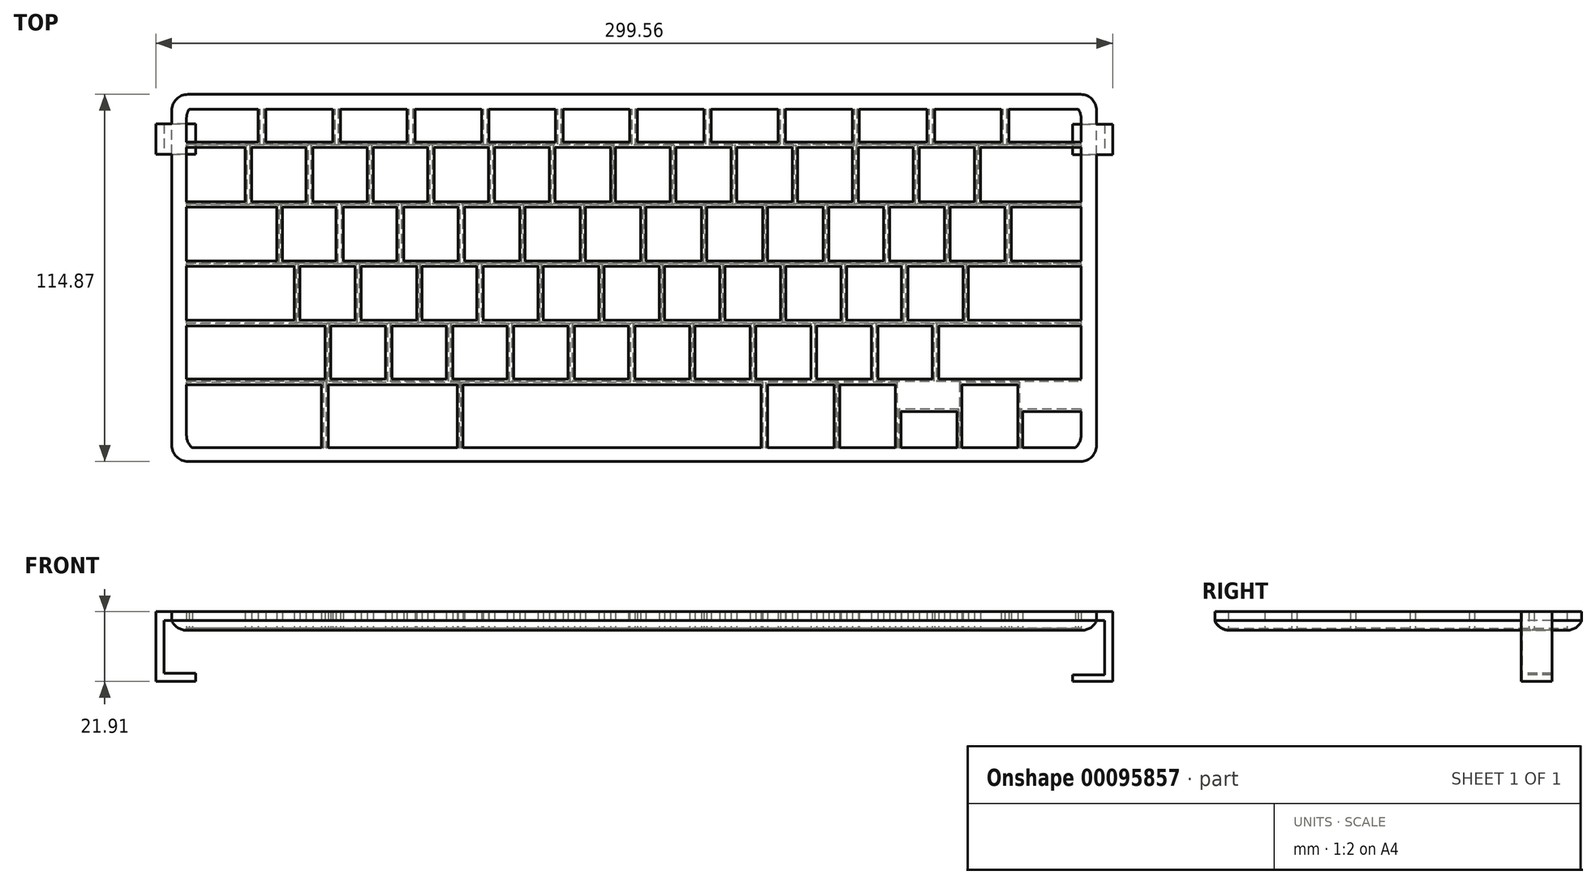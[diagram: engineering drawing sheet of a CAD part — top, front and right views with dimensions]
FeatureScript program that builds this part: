
annotation { "Feature Type Name" : "Feature", "Feature Type Description" : "" }
export const myFeature = defineFeature(function(context is Context, id is Id, definition is map)
    precondition{}
    {
        {
            var Q0;
            Q0=qCreatedBy(makeId("Top.planeOp"),FACE);
            var sketch = newSketch(context, id + "F0", { "sketchPlane" : qUnion([Q0])});
            skLineSegment(sketch, "E0", {"start": v(-1288.18, -372.7) * mm, "end": v(-998.62, -372.7) * mm});
            skSolve(sketch);
        }
        {
            var Q0;
            Q0=qCreatedBy(makeId("Top.planeOp"),FACE);
            var sketch = newSketch(context, id + "F1", { "sketchPlane" : qUnion([Q0])});
            skLineSegment(sketch, "E1.0", {"start": v(-1283.18, -372.7) * mm, "end": v(-1003.62, -372.7) * mm});
            skLineSegment(sketch, "E2", {"start": v(-1288.18, -367.7) * mm, "end": v(-1288.18, -262.82) * mm});
            skLineSegment(sketch, "E3", {"start": v(-998.62, -367.7) * mm, "end": v(-998.62, -262.82) * mm});
            skLineSegment(sketch, "E4", {"start": v(-1283.18, -257.82) * mm, "end": v(-1003.62, -257.82) * mm});
            skLineSegment(sketch, "E5.bottom", {"start": v(-1278.58, -260.22) * mm, "end": v(-1008.5, -260.22) * mm});
            skLineSegment(sketch, "E5.left", {"start": v(-1283.58, -265.22) * mm, "end": v(-1283.58, -272.7) * mm});
            skLineSegment(sketch, "E5.right", {"start": v(-1003.5, -265.22) * mm, "end": v(-1003.5, -272.7) * mm});
            skLineSegment(sketch, "E6.bottom", {"start": v(-1283.58, -272.7) * mm, "end": v(-1261.2, -272.7) * mm});
            skLineSegment(sketch, "E6.top", {"start": v(-1283.58, -274.39) * mm, "end": v(-1265.23, -274.39) * mm});
            skLineSegment(sketch, "E7.bottom", {"start": v(-1003.5, -291.4) * mm, "end": v(-1035.02, -291.4) * mm});
            skLineSegment(sketch, "E7.top", {"start": v(-1003.5, -293.02) * mm, "end": v(-1025.33, -293.02) * mm});
            skLineSegment(sketch, "E8.bottom", {"start": v(-1283.58, -309.96) * mm, "end": v(-1255.31, -309.96) * mm});
            skLineSegment(sketch, "E8.top", {"start": v(-1283.58, -311.57) * mm, "end": v(-1249.8, -311.57) * mm});
            skLineSegment(sketch, "E9.bottom", {"start": v(-1003.5, -328.56) * mm, "end": v(-1038.78, -328.56) * mm});
            skLineSegment(sketch, "E9.top", {"start": v(-1003.5, -330.23) * mm, "end": v(-1048.09, -330.23) * mm});
            skLineSegment(sketch, "E10.bottom", {"start": v(-1283.58, -346.92) * mm, "end": v(-1240.17, -346.92) * mm});
            skLineSegment(sketch, "E10.top", {"start": v(-1283.58, -348.68) * mm, "end": v(-1241.32, -348.68) * mm});
            skLineSegment(sketch, "E11.left", {"start": v(-1023.3, -348.68) * mm, "end": v(-1023.3, -368.4) * mm});
            skLineSegment(sketch, "E11.right", {"start": v(-1021.81, -357.03) * mm, "end": v(-1021.81, -368.4) * mm});
            skLineSegment(sketch, "E12.left", {"start": v(-1040.83, -368.4) * mm, "end": v(-1040.83, -348.68) * mm});
            skLineSegment(sketch, "E12.right", {"start": v(-1042.36, -368.4) * mm, "end": v(-1042.36, -357.03) * mm});
            skLineSegment(sketch, "E13.left", {"start": v(-1059.9, -368.4) * mm, "end": v(-1059.9, -357.03) * mm});
            skLineSegment(sketch, "E13.right", {"start": v(-1061.66, -368.4) * mm, "end": v(-1061.66, -348.68) * mm});
            skLineSegment(sketch, "E14.left", {"start": v(-1079.03, -368.4) * mm, "end": v(-1079.03, -348.68) * mm});
            skLineSegment(sketch, "E14.right", {"start": v(-1080.8, -368.4) * mm, "end": v(-1080.8, -348.68) * mm});
            skLineSegment(sketch, "E15.top", {"start": v(-1282.73, -262.43) * mm, "end": v(-1261.2, -262.43) * mm});
            skLineSegment(sketch, "E16.top", {"start": v(-1021.81, -357.03) * mm, "end": v(-1003.5, -357.03) * mm});
            skLineSegment(sketch, "E17.top", {"start": v(-1059.9, -357.03) * mm, "end": v(-1042.36, -357.03) * mm});
            skLineSegment(sketch, "E18.left", {"start": v(-1241.32, -348.68) * mm, "end": v(-1241.32, -368.4) * mm});
            skLineSegment(sketch, "E18.right", {"start": v(-1239.21, -348.68) * mm, "end": v(-1239.21, -368.4) * mm});
            skLineSegment(sketch, "E19.left", {"start": v(-1198.75, -348.68) * mm, "end": v(-1198.75, -368.4) * mm});
            skLineSegment(sketch, "E19.right", {"start": v(-1197.07, -348.68) * mm, "end": v(-1197.07, -368.4) * mm});
            skLineSegment(sketch, "E20.left", {"start": v(-1103.7, -348.68) * mm, "end": v(-1103.7, -368.4) * mm});
            skLineSegment(sketch, "E20.right", {"start": v(-1101.6, -348.68) * mm, "end": v(-1101.6, -368.4) * mm});
            skLineSegment(sketch, "E21.left", {"start": v(-1240.17, -330.23) * mm, "end": v(-1240.17, -346.92) * mm});
            skLineSegment(sketch, "E21.right", {"start": v(-1238.38, -330.23) * mm, "end": v(-1238.38, -346.92) * mm});
            skLineSegment(sketch, "E22.left", {"start": v(-1221.22, -330.23) * mm, "end": v(-1221.22, -346.92) * mm});
            skLineSegment(sketch, "E22.right", {"start": v(-1219.2, -330.23) * mm, "end": v(-1219.2, -346.92) * mm});
            skLineSegment(sketch, "E23.left", {"start": v(-1202.19, -330.23) * mm, "end": v(-1202.19, -346.92) * mm});
            skLineSegment(sketch, "E23.right", {"start": v(-1200.22, -330.23) * mm, "end": v(-1200.22, -346.92) * mm});
            skLineSegment(sketch, "E24.left", {"start": v(-1183.14, -330.23) * mm, "end": v(-1183.14, -346.92) * mm});
            skLineSegment(sketch, "E24.right", {"start": v(-1181.13, -330.23) * mm, "end": v(-1181.13, -346.92) * mm});
            skLineSegment(sketch, "E25.left", {"start": v(-1164.12, -330.23) * mm, "end": v(-1164.12, -346.92) * mm});
            skLineSegment(sketch, "E25.right", {"start": v(-1162.15, -330.23) * mm, "end": v(-1162.15, -346.92) * mm});
            skLineSegment(sketch, "E26.left", {"start": v(-1145.17, -330.23) * mm, "end": v(-1145.17, -346.92) * mm});
            skLineSegment(sketch, "E26.right", {"start": v(-1143.13, -330.23) * mm, "end": v(-1143.13, -346.92) * mm});
            skLineSegment(sketch, "E27.left", {"start": v(-1126.04, -330.23) * mm, "end": v(-1126.04, -346.92) * mm});
            skLineSegment(sketch, "E27.right", {"start": v(-1124.36, -330.23) * mm, "end": v(-1124.36, -346.92) * mm});
            skLineSegment(sketch, "E28.left", {"start": v(-1107.12, -330.23) * mm, "end": v(-1107.12, -346.92) * mm});
            skLineSegment(sketch, "E28.right", {"start": v(-1105.3, -330.23) * mm, "end": v(-1105.3, -346.92) * mm});
            skLineSegment(sketch, "E29.left", {"start": v(-1088.03, -330.23) * mm, "end": v(-1088.03, -346.92) * mm});
            skLineSegment(sketch, "E29.right", {"start": v(-1086.26, -330.23) * mm, "end": v(-1086.26, -346.92) * mm});
            skLineSegment(sketch, "E30.left", {"start": v(-1069.15, -330.23) * mm, "end": v(-1069.15, -346.92) * mm});
            skLineSegment(sketch, "E30.right", {"start": v(-1067.09, -330.23) * mm, "end": v(-1067.09, -346.92) * mm});
            skLineSegment(sketch, "E31.left", {"start": v(-1050.1, -330.23) * mm, "end": v(-1050.1, -346.92) * mm});
            skLineSegment(sketch, "E31.right", {"start": v(-1048.09, -330.23) * mm, "end": v(-1048.09, -346.92) * mm});
            skLineSegment(sketch, "E32.left", {"start": v(-1249.8, -311.57) * mm, "end": v(-1249.8, -328.56) * mm});
            skLineSegment(sketch, "E32.right", {"start": v(-1248.02, -311.57) * mm, "end": v(-1248.02, -328.56) * mm});
            skLineSegment(sketch, "E33.left", {"start": v(-1230.78, -311.57) * mm, "end": v(-1230.78, -328.56) * mm});
            skLineSegment(sketch, "E33.right", {"start": v(-1228.88, -311.57) * mm, "end": v(-1228.88, -328.56) * mm});
            skLineSegment(sketch, "E34.left", {"start": v(-1211.54, -311.57) * mm, "end": v(-1211.54, -328.56) * mm});
            skLineSegment(sketch, "E34.right", {"start": v(-1209.87, -311.57) * mm, "end": v(-1209.87, -328.56) * mm});
            skLineSegment(sketch, "E35.left", {"start": v(-1192.67, -311.57) * mm, "end": v(-1192.67, -328.56) * mm});
            skLineSegment(sketch, "E35.right", {"start": v(-1190.64, -311.57) * mm, "end": v(-1190.64, -328.56) * mm});
            skLineSegment(sketch, "E36.left", {"start": v(-1173.55, -311.57) * mm, "end": v(-1173.55, -328.56) * mm});
            skLineSegment(sketch, "E36.right", {"start": v(-1171.87, -311.57) * mm, "end": v(-1171.87, -328.56) * mm});
            skLineSegment(sketch, "E37.left", {"start": v(-1154.53, -311.57) * mm, "end": v(-1154.53, -328.56) * mm});
            skLineSegment(sketch, "E37.right", {"start": v(-1152.87, -311.57) * mm, "end": v(-1152.87, -328.56) * mm});
            skLineSegment(sketch, "E38.left", {"start": v(-1135.55, -311.57) * mm, "end": v(-1135.55, -328.56) * mm});
            skLineSegment(sketch, "E38.right", {"start": v(-1133.9, -311.57) * mm, "end": v(-1133.9, -328.56) * mm});
            skLineSegment(sketch, "E39.left", {"start": v(-1116.65, -311.57) * mm, "end": v(-1116.65, -328.56) * mm});
            skLineSegment(sketch, "E39.right", {"start": v(-1115, -311.57) * mm, "end": v(-1115, -328.56) * mm});
            skLineSegment(sketch, "E40.left", {"start": v(-1097.53, -311.57) * mm, "end": v(-1097.53, -328.56) * mm});
            skLineSegment(sketch, "E40.right", {"start": v(-1096, -311.57) * mm, "end": v(-1096, -328.56) * mm});
            skLineSegment(sketch, "E41.left", {"start": v(-1078.67, -311.57) * mm, "end": v(-1078.67, -328.56) * mm});
            skLineSegment(sketch, "E41.right", {"start": v(-1076.87, -311.57) * mm, "end": v(-1076.87, -328.56) * mm});
            skLineSegment(sketch, "E42.left", {"start": v(-1059.7, -311.57) * mm, "end": v(-1059.7, -328.56) * mm});
            skLineSegment(sketch, "E42.right", {"start": v(-1057.73, -311.57) * mm, "end": v(-1057.73, -328.56) * mm});
            skLineSegment(sketch, "E43.left", {"start": v(-1040.48, -311.57) * mm, "end": v(-1040.48, -328.56) * mm});
            skLineSegment(sketch, "E43.right", {"start": v(-1038.78, -311.57) * mm, "end": v(-1038.78, -328.56) * mm});
            skLineSegment(sketch, "E44.left", {"start": v(-1027.3, -293.02) * mm, "end": v(-1027.3, -309.96) * mm});
            skLineSegment(sketch, "E44.right", {"start": v(-1025.33, -293.02) * mm, "end": v(-1025.33, -309.96) * mm});
            skLineSegment(sketch, "E45.left", {"start": v(-1046.22, -293.02) * mm, "end": v(-1046.22, -309.96) * mm});
            skLineSegment(sketch, "E45.right", {"start": v(-1044.44, -293.02) * mm, "end": v(-1044.44, -309.96) * mm});
            skLineSegment(sketch, "E46.left", {"start": v(-1065.37, -293.02) * mm, "end": v(-1065.37, -309.96) * mm});
            skLineSegment(sketch, "E46.right", {"start": v(-1063.36, -293.02) * mm, "end": v(-1063.36, -309.96) * mm});
            skLineSegment(sketch, "E47.left", {"start": v(-1084.25, -293.02) * mm, "end": v(-1084.25, -309.96) * mm});
            skLineSegment(sketch, "E47.right", {"start": v(-1082.42, -293.02) * mm, "end": v(-1082.42, -309.96) * mm});
            skLineSegment(sketch, "E48.left", {"start": v(-1103.17, -293.02) * mm, "end": v(-1103.17, -309.96) * mm});
            skLineSegment(sketch, "E48.right", {"start": v(-1101.62, -293.02) * mm, "end": v(-1101.62, -309.96) * mm});
            skLineSegment(sketch, "E49.left", {"start": v(-1122.33, -293.02) * mm, "end": v(-1122.33, -309.96) * mm});
            skLineSegment(sketch, "E49.right", {"start": v(-1120.67, -293.02) * mm, "end": v(-1120.67, -309.96) * mm});
            skLineSegment(sketch, "E50.bottom", {"start": v(-1143.54, -293.02) * mm, "end": v(-1141.36, -293.02) * mm});
            skLineSegment(sketch, "E50.top", {"start": v(-1143.47, -309.96) * mm, "end": v(-1141.36, -309.96) * mm});
            skLineSegment(sketch, "E50.right", {"start": v(-1139.74, -293.02) * mm, "end": v(-1139.74, -309.96) * mm});
            skLineSegment(sketch, "E51.left", {"start": v(-1160.37, -293.02) * mm, "end": v(-1160.37, -309.96) * mm});
            skLineSegment(sketch, "E51.right", {"start": v(-1158.61, -293.02) * mm, "end": v(-1158.61, -309.96) * mm});
            skLineSegment(sketch, "E52.left", {"start": v(-1179.26, -293.02) * mm, "end": v(-1179.26, -309.96) * mm});
            skLineSegment(sketch, "E52.right", {"start": v(-1177.57, -293.02) * mm, "end": v(-1177.57, -309.96) * mm});
            skLineSegment(sketch, "E53.left", {"start": v(-1198.57, -293.02) * mm, "end": v(-1198.57, -309.96) * mm});
            skLineSegment(sketch, "E53.right", {"start": v(-1196.47, -293.02) * mm, "end": v(-1196.47, -309.96) * mm});
            skLineSegment(sketch, "E54.left", {"start": v(-1217.7, -293.02) * mm, "end": v(-1217.7, -309.96) * mm});
            skLineSegment(sketch, "E54.right", {"start": v(-1215.6, -293.02) * mm, "end": v(-1215.6, -309.96) * mm});
            skLineSegment(sketch, "E55.left", {"start": v(-1236.78, -293.02) * mm, "end": v(-1236.78, -309.96) * mm});
            skLineSegment(sketch, "E55.right", {"start": v(-1234.44, -293.02) * mm, "end": v(-1234.44, -309.96) * mm});
            skLineSegment(sketch, "E56.left", {"start": v(-1253.5, -293.02) * mm, "end": v(-1253.5, -309.96) * mm});
            skLineSegment(sketch, "E56.right", {"start": v(-1255.31, -293.02) * mm, "end": v(-1255.31, -309.96) * mm});
            skLineSegment(sketch, "E57.left", {"start": v(-1265.23, -274.39) * mm, "end": v(-1265.23, -291.4) * mm});
            skLineSegment(sketch, "E57.right", {"start": v(-1263.13, -274.39) * mm, "end": v(-1263.13, -291.4) * mm});
            skLineSegment(sketch, "E58.left", {"start": v(-1246.16, -274.39) * mm, "end": v(-1246.16, -291.4) * mm});
            skLineSegment(sketch, "E58.right", {"start": v(-1243.97, -274.39) * mm, "end": v(-1243.97, -291.4) * mm});
            skLineSegment(sketch, "E59.left", {"start": v(-1226.95, -274.39) * mm, "end": v(-1226.95, -291.4) * mm});
            skLineSegment(sketch, "E59.right", {"start": v(-1225.03, -274.39) * mm, "end": v(-1225.03, -291.4) * mm});
            skLineSegment(sketch, "E60.left", {"start": v(-1208.07, -274.39) * mm, "end": v(-1208.07, -291.4) * mm});
            skLineSegment(sketch, "E60.right", {"start": v(-1206, -274.39) * mm, "end": v(-1206, -291.4) * mm});
            skLineSegment(sketch, "E61.left", {"start": v(-1189.03, -274.39) * mm, "end": v(-1189.03, -291.4) * mm});
            skLineSegment(sketch, "E61.right", {"start": v(-1187.09, -274.39) * mm, "end": v(-1187.09, -291.4) * mm});
            skLineSegment(sketch, "E62.left", {"start": v(-1170.02, -274.39) * mm, "end": v(-1170.02, -291.4) * mm});
            skLineSegment(sketch, "E62.right", {"start": v(-1168.2, -274.39) * mm, "end": v(-1168.2, -291.4) * mm});
            skLineSegment(sketch, "E63.left", {"start": v(-1150.85, -274.39) * mm, "end": v(-1150.85, -291.4) * mm});
            skLineSegment(sketch, "E63.right", {"start": v(-1149.3, -274.39) * mm, "end": v(-1149.3, -291.4) * mm});
            skLineSegment(sketch, "E64.left", {"start": v(-1132.1, -274.39) * mm, "end": v(-1132.1, -291.4) * mm});
            skLineSegment(sketch, "E64.right", {"start": v(-1130.32, -274.39) * mm, "end": v(-1130.32, -291.4) * mm});
            skLineSegment(sketch, "E65.left", {"start": v(-1113.1, -274.39) * mm, "end": v(-1113.1, -291.4) * mm});
            skLineSegment(sketch, "E65.right", {"start": v(-1111.29, -274.39) * mm, "end": v(-1111.29, -291.4) * mm});
            skLineSegment(sketch, "E66.left", {"start": v(-1093.95, -274.39) * mm, "end": v(-1093.95, -291.4) * mm});
            skLineSegment(sketch, "E66.right", {"start": v(-1092.22, -274.39) * mm, "end": v(-1092.22, -291.4) * mm});
            skLineSegment(sketch, "E67.left", {"start": v(-1075.1, -274.39) * mm, "end": v(-1075.1, -291.4) * mm});
            skLineSegment(sketch, "E67.right", {"start": v(-1073.22, -274.39) * mm, "end": v(-1073.22, -291.4) * mm});
            skLineSegment(sketch, "E68.left", {"start": v(-1056.04, -274.39) * mm, "end": v(-1056.04, -291.4) * mm});
            skLineSegment(sketch, "E68.right", {"start": v(-1054.15, -274.39) * mm, "end": v(-1054.15, -291.4) * mm});
            skLineSegment(sketch, "E69.left", {"start": v(-1036.83, -274.39) * mm, "end": v(-1036.83, -291.4) * mm});
            skLineSegment(sketch, "E69.right", {"start": v(-1035.02, -274.39) * mm, "end": v(-1035.02, -291.4) * mm});
            skLineSegment(sketch, "E70.left", {"start": v(-1051.72, -262.43) * mm, "end": v(-1051.72, -272.7) * mm});
            skLineSegment(sketch, "E70.right", {"start": v(-1049.35, -262.43) * mm, "end": v(-1049.35, -272.7) * mm});
            skLineSegment(sketch, "E71.left", {"start": v(-1075.08, -262.43) * mm, "end": v(-1075.08, -272.7) * mm});
            skLineSegment(sketch, "E71.right", {"start": v(-1072.96, -262.43) * mm, "end": v(-1072.96, -272.7) * mm});
            skLineSegment(sketch, "E72.left", {"start": v(-1098.33, -262.43) * mm, "end": v(-1098.33, -272.7) * mm});
            skLineSegment(sketch, "E72.right", {"start": v(-1096.04, -262.43) * mm, "end": v(-1096.04, -272.7) * mm});
            skLineSegment(sketch, "E73.left", {"start": v(-1121.6, -262.43) * mm, "end": v(-1121.6, -272.7) * mm});
            skLineSegment(sketch, "E73.right", {"start": v(-1119.29, -262.43) * mm, "end": v(-1119.29, -272.7) * mm});
            skLineSegment(sketch, "E74.left", {"start": v(-1144.78, -262.43) * mm, "end": v(-1144.78, -272.7) * mm});
            skLineSegment(sketch, "E74.right", {"start": v(-1142.44, -262.43) * mm, "end": v(-1142.44, -272.7) * mm});
            skLineSegment(sketch, "E75.left", {"start": v(-1168.04, -262.43) * mm, "end": v(-1168.04, -272.7) * mm});
            skLineSegment(sketch, "E75.right", {"start": v(-1165.67, -262.43) * mm, "end": v(-1165.67, -272.7) * mm});
            skLineSegment(sketch, "E76.left", {"start": v(-1191.2, -262.43) * mm, "end": v(-1191.2, -272.7) * mm});
            skLineSegment(sketch, "E76.right", {"start": v(-1188.87, -262.43) * mm, "end": v(-1188.87, -272.7) * mm});
            skLineSegment(sketch, "E77.left", {"start": v(-1214.59, -262.43) * mm, "end": v(-1214.59, -272.7) * mm});
            skLineSegment(sketch, "E77.right", {"start": v(-1212.05, -262.43) * mm, "end": v(-1212.05, -272.7) * mm});
            skLineSegment(sketch, "E78.left", {"start": v(-1237.77, -262.43) * mm, "end": v(-1237.77, -272.7) * mm});
            skLineSegment(sketch, "E78.right", {"start": v(-1235.41, -262.43) * mm, "end": v(-1235.41, -272.7) * mm});
            skLineSegment(sketch, "E79.left", {"start": v(-1261.2, -262.43) * mm, "end": v(-1261.2, -272.7) * mm});
            skLineSegment(sketch, "E79.right", {"start": v(-1258.8, -262.43) * mm, "end": v(-1258.8, -272.7) * mm});
            skPoint(sketch, "E80.visualSharp", {"position": v(-1003.5, -369.57) * mm});
            skArc(sketch, "E80.filletArc", {"start": v(-1005.3, -368.4) * mm, "mid": v(-1003.97, -366.69) * mm, "end": v(-1003.5, -364.57) * mm});
            skPoint(sketch, "E81.visualSharp", {"position": v(-1003.5, -260.22) * mm});
            skArc(sketch, "E81.filletArc", {"start": v(-1003.5, -265.22) * mm, "mid": v(-1004.97, -261.68) * mm, "end": v(-1008.5, -260.22) * mm});
            skPoint(sketch, "E82.visualSharp", {"position": v(-1283.58, -260.22) * mm});
            skArc(sketch, "E82.filletArc", {"start": v(-1278.58, -260.22) * mm, "mid": v(-1282.11, -261.68) * mm, "end": v(-1283.58, -265.22) * mm});
            skPoint(sketch, "E83.visualSharp", {"position": v(-1283.58, -369.57) * mm});
            skArc(sketch, "E83.filletArc", {"start": v(-1283.58, -364.57) * mm, "mid": v(-1283.1, -366.69) * mm, "end": v(-1281.78, -368.4) * mm});
            skPoint(sketch, "E84.visualSharp", {"position": v(-1288.18, -372.7) * mm});
            skArc(sketch, "E84.filletArc", {"start": v(-1288.18, -367.7) * mm, "mid": v(-1286.72, -371.23) * mm, "end": v(-1283.18, -372.7) * mm});
            skPoint(sketch, "E85.visualSharp", {"position": v(-998.62, -372.7) * mm});
            skArc(sketch, "E85.filletArc", {"start": v(-1003.62, -372.7) * mm, "mid": v(-1000.09, -371.23) * mm, "end": v(-998.62, -367.7) * mm});
            skPoint(sketch, "E86.visualSharp", {"position": v(-998.62, -257.82) * mm});
            skArc(sketch, "E86.filletArc", {"start": v(-998.62, -262.82) * mm, "mid": v(-1000.09, -259.29) * mm, "end": v(-1003.62, -257.82) * mm});
            skPoint(sketch, "E87.visualSharp", {"position": v(-1288.18, -257.82) * mm});
            skArc(sketch, "E87.filletArc", {"start": v(-1283.18, -257.82) * mm, "mid": v(-1286.72, -259.29) * mm, "end": v(-1288.18, -262.82) * mm});
            skLineSegment(sketch, "E88.left", {"start": v(-1028.53, -262.43) * mm, "end": v(-1028.53, -272.7) * mm});
            skLineSegment(sketch, "E88.right", {"start": v(-1026.1, -262.43) * mm, "end": v(-1026.1, -272.7) * mm});
            skLineSegment(sketch, "E89", {"start": v(-1141.36, -293.02) * mm, "end": v(-1141.36, -309.96) * mm});
            skLineSegment(sketch, "E90", {"start": v(-1281.78, -368.4) * mm, "end": v(-1241.32, -368.4) * mm});
            skLineSegment(sketch, "E91.trimOffspring", {"start": v(-1258.8, -272.7) * mm, "end": v(-1237.77, -272.7) * mm});
            skLineSegment(sketch, "E92.trimOffspring", {"start": v(-1235.41, -272.7) * mm, "end": v(-1214.59, -272.7) * mm});
            skLineSegment(sketch, "E93.trimOffspring", {"start": v(-1212.05, -272.7) * mm, "end": v(-1191.2, -272.7) * mm});
            skLineSegment(sketch, "E94.trimOffspring", {"start": v(-1188.87, -272.7) * mm, "end": v(-1168.04, -272.7) * mm});
            skLineSegment(sketch, "E95.trimOffspring", {"start": v(-1258.8, -262.43) * mm, "end": v(-1237.77, -262.43) * mm});
            skLineSegment(sketch, "E96.trimOffspring", {"start": v(-1235.41, -262.43) * mm, "end": v(-1214.59, -262.43) * mm});
            skLineSegment(sketch, "E97.trimOffspring", {"start": v(-1212.05, -262.43) * mm, "end": v(-1191.2, -262.43) * mm});
            skLineSegment(sketch, "E98.trimOffspring", {"start": v(-1188.87, -262.43) * mm, "end": v(-1168.04, -262.43) * mm});
            skLineSegment(sketch, "E99.trimOffspring", {"start": v(-1165.67, -262.43) * mm, "end": v(-1144.78, -262.43) * mm});
            skLineSegment(sketch, "E100.trimOffspring", {"start": v(-1165.67, -272.7) * mm, "end": v(-1144.78, -272.7) * mm});
            skLineSegment(sketch, "E101.trimOffspring", {"start": v(-1142.44, -272.7) * mm, "end": v(-1121.6, -272.7) * mm});
            skLineSegment(sketch, "E102.trimOffspring", {"start": v(-1142.44, -262.43) * mm, "end": v(-1121.6, -262.43) * mm});
            skLineSegment(sketch, "E103.trimOffspring", {"start": v(-1119.29, -262.43) * mm, "end": v(-1098.33, -262.43) * mm});
            skLineSegment(sketch, "E104.trimOffspring", {"start": v(-1119.29, -272.7) * mm, "end": v(-1098.33, -272.7) * mm});
            skLineSegment(sketch, "E105.trimOffspring", {"start": v(-1096.04, -262.43) * mm, "end": v(-1075.08, -262.43) * mm});
            skLineSegment(sketch, "E106.trimOffspring", {"start": v(-1096.04, -272.7) * mm, "end": v(-1075.08, -272.7) * mm});
            skLineSegment(sketch, "E107.trimOffspring", {"start": v(-1072.96, -262.43) * mm, "end": v(-1051.72, -262.43) * mm});
            skLineSegment(sketch, "E108.trimOffspring", {"start": v(-1072.96, -272.7) * mm, "end": v(-1051.72, -272.7) * mm});
            skLineSegment(sketch, "E109.trimOffspring", {"start": v(-1049.35, -262.43) * mm, "end": v(-1028.53, -262.43) * mm});
            skLineSegment(sketch, "E110.trimOffspring", {"start": v(-1049.35, -272.7) * mm, "end": v(-1028.53, -272.7) * mm});
            skLineSegment(sketch, "E111.trimOffspring", {"start": v(-1026.1, -262.43) * mm, "end": v(-1004.35, -262.43) * mm});
            skLineSegment(sketch, "E112.trimOffspring", {"start": v(-1026.1, -272.7) * mm, "end": v(-1003.5, -272.7) * mm});
            skLineSegment(sketch, "E113.trimOffspring", {"start": v(-1283.58, -274.39) * mm, "end": v(-1283.58, -291.4) * mm});
            skLineSegment(sketch, "E114.trimOffspring", {"start": v(-1283.58, -293.02) * mm, "end": v(-1283.58, -309.96) * mm});
            skLineSegment(sketch, "E115.trimOffspring", {"start": v(-1283.58, -311.57) * mm, "end": v(-1283.58, -328.56) * mm});
            skLineSegment(sketch, "E116.trimOffspring", {"start": v(-1283.58, -330.23) * mm, "end": v(-1283.58, -346.92) * mm});
            skLineSegment(sketch, "E117.trimOffspring", {"start": v(-1283.58, -348.68) * mm, "end": v(-1283.58, -364.57) * mm});
            skLineSegment(sketch, "E118.trimOffspring", {"start": v(-1003.5, -274.39) * mm, "end": v(-1003.5, -291.4) * mm});
            skLineSegment(sketch, "E119.trimOffspring", {"start": v(-1003.5, -293.02) * mm, "end": v(-1003.5, -309.96) * mm});
            skLineSegment(sketch, "E120.trimOffspring", {"start": v(-1003.5, -311.57) * mm, "end": v(-1003.5, -328.56) * mm});
            skLineSegment(sketch, "E121.trimOffspring", {"start": v(-1003.5, -330.23) * mm, "end": v(-1003.5, -346.92) * mm});
            skLineSegment(sketch, "E122.trimOffspring", {"start": v(-1003.5, -357.03) * mm, "end": v(-1003.5, -364.57) * mm});
            skLineSegment(sketch, "E123.trimOffspring", {"start": v(-1059.9, -368.4) * mm, "end": v(-1042.36, -368.4) * mm});
            skLineSegment(sketch, "E124.trimOffspring", {"start": v(-1040.83, -368.4) * mm, "end": v(-1023.3, -368.4) * mm});
            skLineSegment(sketch, "E125.trimOffspring", {"start": v(-1021.81, -368.4) * mm, "end": v(-1005.3, -368.4) * mm});
            skLineSegment(sketch, "E126.trimOffspring", {"start": v(-1040.83, -348.68) * mm, "end": v(-1023.3, -348.68) * mm});
            skLineSegment(sketch, "E127.trimOffspring", {"start": v(-1079.03, -368.4) * mm, "end": v(-1061.66, -368.4) * mm});
            skLineSegment(sketch, "E128.trimOffspring", {"start": v(-1101.6, -368.4) * mm, "end": v(-1080.8, -368.4) * mm});
            skLineSegment(sketch, "E129.trimOffspring", {"start": v(-1079.03, -348.68) * mm, "end": v(-1061.66, -348.68) * mm});
            skLineSegment(sketch, "E130.trimOffspring", {"start": v(-1101.6, -348.68) * mm, "end": v(-1080.8, -348.68) * mm});
            skLineSegment(sketch, "E131.trimOffspring", {"start": v(-1197.07, -368.4) * mm, "end": v(-1103.7, -368.4) * mm});
            skLineSegment(sketch, "E132.trimOffspring", {"start": v(-1239.21, -368.4) * mm, "end": v(-1198.75, -368.4) * mm});
            skLineSegment(sketch, "E133.trimOffspring", {"start": v(-1239.21, -348.68) * mm, "end": v(-1198.75, -348.68) * mm});
            skLineSegment(sketch, "E134.trimOffspring", {"start": v(-1197.07, -348.68) * mm, "end": v(-1103.7, -348.68) * mm});
            skLineSegment(sketch, "E135.trimOffspring", {"start": v(-1238.38, -346.92) * mm, "end": v(-1221.22, -346.92) * mm});
            skLineSegment(sketch, "E136.trimOffspring", {"start": v(-1219.2, -346.92) * mm, "end": v(-1202.19, -346.92) * mm});
            skLineSegment(sketch, "E137.trimOffspring", {"start": v(-1221.22, -330.23) * mm, "end": v(-1238.38, -330.23) * mm});
            skLineSegment(sketch, "E138.trimOffspring", {"start": v(-1211.54, -328.56) * mm, "end": v(-1228.88, -328.56) * mm});
            skLineSegment(sketch, "E139.trimOffspring", {"start": v(-1230.78, -328.56) * mm, "end": v(-1248.02, -328.56) * mm});
            skLineSegment(sketch, "E140.trimOffspring", {"start": v(-1249.8, -328.56) * mm, "end": v(-1283.58, -328.56) * mm});
            skLineSegment(sketch, "E141.trimOffspring", {"start": v(-1240.17, -330.23) * mm, "end": v(-1283.58, -330.23) * mm});
            skLineSegment(sketch, "E142.trimOffspring", {"start": v(-1192.67, -328.56) * mm, "end": v(-1209.87, -328.56) * mm});
            skLineSegment(sketch, "E143.trimOffspring", {"start": v(-1183.14, -330.23) * mm, "end": v(-1200.22, -330.23) * mm});
            skLineSegment(sketch, "E144.trimOffspring", {"start": v(-1164.12, -330.23) * mm, "end": v(-1181.13, -330.23) * mm});
            skLineSegment(sketch, "E145.trimOffspring", {"start": v(-1154.53, -328.56) * mm, "end": v(-1171.87, -328.56) * mm});
            skLineSegment(sketch, "E146.trimOffspring", {"start": v(-1145.17, -330.23) * mm, "end": v(-1162.15, -330.23) * mm});
            skLineSegment(sketch, "E147.trimOffspring", {"start": v(-1135.55, -328.56) * mm, "end": v(-1152.87, -328.56) * mm});
            skLineSegment(sketch, "E148.trimOffspring", {"start": v(-1116.65, -328.56) * mm, "end": v(-1133.9, -328.56) * mm});
            skLineSegment(sketch, "E149.trimOffspring", {"start": v(-1124.36, -346.92) * mm, "end": v(-1107.12, -346.92) * mm});
            skLineSegment(sketch, "E150.trimOffspring", {"start": v(-1143.13, -346.92) * mm, "end": v(-1126.04, -346.92) * mm});
            skLineSegment(sketch, "E151.trimOffspring", {"start": v(-1162.15, -346.92) * mm, "end": v(-1145.17, -346.92) * mm});
            skLineSegment(sketch, "E152.trimOffspring", {"start": v(-1181.13, -346.92) * mm, "end": v(-1164.12, -346.92) * mm});
            skLineSegment(sketch, "E153.trimOffspring", {"start": v(-1173.55, -328.56) * mm, "end": v(-1190.64, -328.56) * mm});
            skLineSegment(sketch, "E154.trimOffspring", {"start": v(-1126.04, -330.23) * mm, "end": v(-1143.13, -330.23) * mm});
            skLineSegment(sketch, "E155.trimOffspring", {"start": v(-1107.12, -330.23) * mm, "end": v(-1124.36, -330.23) * mm});
            skLineSegment(sketch, "E156.trimOffspring", {"start": v(-1105.3, -346.92) * mm, "end": v(-1088.03, -346.92) * mm});
            skLineSegment(sketch, "E157.trimOffspring", {"start": v(-1097.53, -328.56) * mm, "end": v(-1115, -328.56) * mm});
            skLineSegment(sketch, "E158.trimOffspring", {"start": v(-1088.03, -330.23) * mm, "end": v(-1105.3, -330.23) * mm});
            skLineSegment(sketch, "E159.trimOffspring", {"start": v(-1078.67, -328.56) * mm, "end": v(-1096, -328.56) * mm});
            skLineSegment(sketch, "E160.trimOffspring", {"start": v(-1059.7, -328.56) * mm, "end": v(-1076.87, -328.56) * mm});
            skLineSegment(sketch, "E161.trimOffspring", {"start": v(-1050.1, -330.23) * mm, "end": v(-1067.09, -330.23) * mm});
            skLineSegment(sketch, "E162.trimOffspring", {"start": v(-1048.09, -346.92) * mm, "end": v(-1003.5, -346.92) * mm});
            skLineSegment(sketch, "E163.trimOffspring", {"start": v(-1040.48, -328.56) * mm, "end": v(-1057.73, -328.56) * mm});
            skLineSegment(sketch, "E164.trimOffspring", {"start": v(-1069.15, -330.23) * mm, "end": v(-1086.26, -330.23) * mm});
            skLineSegment(sketch, "E165.trimOffspring", {"start": v(-1067.09, -346.92) * mm, "end": v(-1050.1, -346.92) * mm});
            skLineSegment(sketch, "E166.trimOffspring", {"start": v(-1086.26, -346.92) * mm, "end": v(-1069.15, -346.92) * mm});
            skLineSegment(sketch, "E167.trimOffspring", {"start": v(-1025.33, -309.96) * mm, "end": v(-1003.5, -309.96) * mm});
            skLineSegment(sketch, "E168.trimOffspring", {"start": v(-1038.78, -311.57) * mm, "end": v(-1003.5, -311.57) * mm});
            skLineSegment(sketch, "E169.trimOffspring", {"start": v(-1044.44, -309.96) * mm, "end": v(-1027.3, -309.96) * mm});
            skLineSegment(sketch, "E170.trimOffspring", {"start": v(-1063.36, -309.96) * mm, "end": v(-1046.22, -309.96) * mm});
            skLineSegment(sketch, "E171.trimOffspring", {"start": v(-1076.87, -311.57) * mm, "end": v(-1059.7, -311.57) * mm});
            skLineSegment(sketch, "E172.trimOffspring", {"start": v(-1082.42, -309.96) * mm, "end": v(-1065.37, -309.96) * mm});
            skLineSegment(sketch, "E173.trimOffspring", {"start": v(-1096, -311.57) * mm, "end": v(-1078.67, -311.57) * mm});
            skLineSegment(sketch, "E174.trimOffspring", {"start": v(-1057.73, -311.57) * mm, "end": v(-1040.48, -311.57) * mm});
            skLineSegment(sketch, "E175.trimOffspring", {"start": v(-1115, -311.57) * mm, "end": v(-1097.53, -311.57) * mm});
            skLineSegment(sketch, "E176.trimOffspring", {"start": v(-1133.9, -311.57) * mm, "end": v(-1116.65, -311.57) * mm});
            skLineSegment(sketch, "E177.trimOffspring", {"start": v(-1152.87, -311.57) * mm, "end": v(-1135.55, -311.57) * mm});
            skLineSegment(sketch, "E178.trimOffspring", {"start": v(-1171.87, -311.57) * mm, "end": v(-1154.53, -311.57) * mm});
            skLineSegment(sketch, "E179.trimOffspring", {"start": v(-1179.26, -293.02) * mm, "end": v(-1196.47, -293.02) * mm});
            skLineSegment(sketch, "E180.trimOffspring", {"start": v(-1170.02, -291.4) * mm, "end": v(-1187.09, -291.4) * mm});
            skLineSegment(sketch, "E181.trimOffspring", {"start": v(-1160.37, -293.02) * mm, "end": v(-1177.57, -293.02) * mm});
            skLineSegment(sketch, "E182.trimOffspring", {"start": v(-1158.61, -309.96) * mm, "end": v(-1141.36, -309.96) * mm});
            skLineSegment(sketch, "E183.trimOffspring", {"start": v(-1139.74, -309.96) * mm, "end": v(-1122.33, -309.96) * mm});
            skLineSegment(sketch, "E184.trimOffspring", {"start": v(-1141.36, -293.02) * mm, "end": v(-1158.61, -293.02) * mm});
            skLineSegment(sketch, "E185.trimOffspring", {"start": v(-1150.85, -291.4) * mm, "end": v(-1168.2, -291.4) * mm});
            skLineSegment(sketch, "E186.trimOffspring", {"start": v(-1132.1, -291.4) * mm, "end": v(-1149.3, -291.4) * mm});
            skLineSegment(sketch, "E187.trimOffspring", {"start": v(-1122.33, -293.02) * mm, "end": v(-1139.74, -293.02) * mm});
            skLineSegment(sketch, "E188.trimOffspring", {"start": v(-1120.67, -309.96) * mm, "end": v(-1103.17, -309.96) * mm});
            skLineSegment(sketch, "E189.trimOffspring", {"start": v(-1103.17, -293.02) * mm, "end": v(-1120.67, -293.02) * mm});
            skLineSegment(sketch, "E190.trimOffspring", {"start": v(-1101.62, -309.96) * mm, "end": v(-1084.25, -309.96) * mm});
            skLineSegment(sketch, "E191.trimOffspring", {"start": v(-1177.57, -309.96) * mm, "end": v(-1160.37, -309.96) * mm});
            skLineSegment(sketch, "E192.trimOffspring", {"start": v(-1113.1, -291.4) * mm, "end": v(-1130.32, -291.4) * mm});
            skLineSegment(sketch, "E193.trimOffspring", {"start": v(-1196.47, -309.96) * mm, "end": v(-1179.26, -309.96) * mm});
            skLineSegment(sketch, "E194.trimOffspring", {"start": v(-1215.6, -309.96) * mm, "end": v(-1198.57, -309.96) * mm});
            skLineSegment(sketch, "E195.trimOffspring", {"start": v(-1253.5, -309.96) * mm, "end": v(-1236.78, -309.96) * mm});
            skLineSegment(sketch, "E196.trimOffspring", {"start": v(-1217.7, -293.02) * mm, "end": v(-1234.44, -293.02) * mm});
            skLineSegment(sketch, "E197.trimOffspring", {"start": v(-1198.57, -293.02) * mm, "end": v(-1215.6, -293.02) * mm});
            skLineSegment(sketch, "E198.trimOffspring", {"start": v(-1189.03, -291.4) * mm, "end": v(-1206, -291.4) * mm});
            skLineSegment(sketch, "E199.trimOffspring", {"start": v(-1226.95, -291.4) * mm, "end": v(-1243.97, -291.4) * mm});
            skLineSegment(sketch, "E200.trimOffspring", {"start": v(-1246.16, -291.4) * mm, "end": v(-1263.13, -291.4) * mm});
            skLineSegment(sketch, "E201.trimOffspring", {"start": v(-1243.97, -274.39) * mm, "end": v(-1226.95, -274.39) * mm});
            skLineSegment(sketch, "E202.trimOffspring", {"start": v(-1225.03, -274.39) * mm, "end": v(-1208.07, -274.39) * mm});
            skLineSegment(sketch, "E203.trimOffspring", {"start": v(-1206, -274.39) * mm, "end": v(-1189.03, -274.39) * mm});
            skLineSegment(sketch, "E204.trimOffspring", {"start": v(-1187.09, -274.39) * mm, "end": v(-1170.02, -274.39) * mm});
            skLineSegment(sketch, "E205.trimOffspring", {"start": v(-1255.31, -293.02) * mm, "end": v(-1283.58, -293.02) * mm});
            skLineSegment(sketch, "E206.trimOffspring", {"start": v(-1234.44, -309.96) * mm, "end": v(-1217.7, -309.96) * mm});
            skLineSegment(sketch, "E207.trimOffspring", {"start": v(-1236.78, -293.02) * mm, "end": v(-1253.5, -293.02) * mm});
            skLineSegment(sketch, "E208.trimOffspring", {"start": v(-1208.07, -291.4) * mm, "end": v(-1225.03, -291.4) * mm});
            skLineSegment(sketch, "E209.trimOffspring", {"start": v(-1190.64, -311.57) * mm, "end": v(-1173.55, -311.57) * mm});
            skLineSegment(sketch, "E210.trimOffspring", {"start": v(-1209.87, -311.57) * mm, "end": v(-1192.67, -311.57) * mm});
            skLineSegment(sketch, "E211.trimOffspring", {"start": v(-1228.88, -311.57) * mm, "end": v(-1211.54, -311.57) * mm});
            skLineSegment(sketch, "E212.trimOffspring", {"start": v(-1248.02, -311.57) * mm, "end": v(-1230.78, -311.57) * mm});
            skLineSegment(sketch, "E213.trimOffspring", {"start": v(-1265.23, -291.4) * mm, "end": v(-1283.58, -291.4) * mm});
            skLineSegment(sketch, "E214.trimOffspring", {"start": v(-1263.13, -274.39) * mm, "end": v(-1246.16, -274.39) * mm});
            skLineSegment(sketch, "E215.trimOffspring", {"start": v(-1168.2, -274.39) * mm, "end": v(-1150.85, -274.39) * mm});
            skLineSegment(sketch, "E216.trimOffspring", {"start": v(-1149.3, -274.39) * mm, "end": v(-1132.1, -274.39) * mm});
            skLineSegment(sketch, "E217.trimOffspring", {"start": v(-1130.32, -274.39) * mm, "end": v(-1113.1, -274.39) * mm});
            skLineSegment(sketch, "E218.trimOffspring", {"start": v(-1111.29, -274.39) * mm, "end": v(-1093.95, -274.39) * mm});
            skLineSegment(sketch, "E219.trimOffspring", {"start": v(-1092.22, -274.39) * mm, "end": v(-1075.1, -274.39) * mm});
            skLineSegment(sketch, "E220.trimOffspring", {"start": v(-1093.95, -291.4) * mm, "end": v(-1111.29, -291.4) * mm});
            skLineSegment(sketch, "E221.trimOffspring", {"start": v(-1084.25, -293.02) * mm, "end": v(-1101.62, -293.02) * mm});
            skLineSegment(sketch, "E222.trimOffspring", {"start": v(-1046.22, -293.02) * mm, "end": v(-1063.36, -293.02) * mm});
            skLineSegment(sketch, "E223.trimOffspring", {"start": v(-1036.83, -291.4) * mm, "end": v(-1054.15, -291.4) * mm});
            skLineSegment(sketch, "E224.trimOffspring", {"start": v(-1027.3, -293.02) * mm, "end": v(-1044.44, -293.02) * mm});
            skLineSegment(sketch, "E225.trimOffspring", {"start": v(-1035.02, -274.39) * mm, "end": v(-1003.5, -274.39) * mm});
            skLineSegment(sketch, "E226.trimOffspring", {"start": v(-1054.15, -274.39) * mm, "end": v(-1036.83, -274.39) * mm});
            skLineSegment(sketch, "E227.trimOffspring", {"start": v(-1073.22, -274.39) * mm, "end": v(-1056.04, -274.39) * mm});
            skLineSegment(sketch, "E228.trimOffspring", {"start": v(-1075.1, -291.4) * mm, "end": v(-1092.22, -291.4) * mm});
            skLineSegment(sketch, "E229.trimOffspring", {"start": v(-1065.37, -293.02) * mm, "end": v(-1082.42, -293.02) * mm});
            skLineSegment(sketch, "E230.trimOffspring", {"start": v(-1202.19, -330.23) * mm, "end": v(-1219.2, -330.23) * mm});
            skLineSegment(sketch, "E231.trimOffspring", {"start": v(-1200.22, -346.92) * mm, "end": v(-1183.14, -346.92) * mm});
            skLineSegment(sketch, "E232.trimOffspring", {"start": v(-1056.04, -291.4) * mm, "end": v(-1073.22, -291.4) * mm});
            skSolve(sketch);
        }
        {
            var Q0;
            Q0=makeQuery(id+"F1.imprint","IMPRINT",FACE,{"disambiguationData":[TD([[makeQuery(id+"F1.imprint","IMPRINT",EDGE,{"derivedFrom":sQuery(id+"F1.wireOp",EDGE,"E1.0")}),1.0]])]});
            extrude(context, id + "F2", {"entities" : qUnion([Q0]), "depth" : 3 * mm});
        }
        {
            var Q0;
            Q0=makeQuery(id+"F2.opExtrude","CAP_EDGE",EDGE,{"disambiguationData":[OSD([sQuery(id+"F1.wireOp",EDGE,"E2")])],"isStart":true});
            var Q1;
            Q1=makeQuery(id+"F2.opExtrude","CAP_EDGE",EDGE,{"disambiguationData":[OSD([sQuery(id+"F1.wireOp",EDGE,"E1.0")])],"isStart":true});
            var Q2;
            Q2=makeQuery(id+"F2.opExtrude","CAP_EDGE",EDGE,{"disambiguationData":[OSD([sQuery(id+"F1.wireOp",EDGE,"E3")])],"isStart":true});
            var Q3;
            Q3=makeQuery(id+"F2.opExtrude","CAP_EDGE",EDGE,{"disambiguationData":[OSD([sQuery(id+"F1.wireOp",EDGE,"E4")])],"isStart":true});
            fillet(context, id + "F3", {"entities" : qUnion([Q0, Q1, Q2, Q3]), "radius" : 5 * mm, "tangentPropagation" : true, "allowEdgeOverflow" : false});
        }
        {
            var Q0;
            Q0=makeQuery(id+"F2.opExtrude","CAP_EDGE",EDGE,{"disambiguationData":[OSD([sQuery(id+"F1.wireOp",EDGE,"E18.right")])],"isStart":true});
            var Q1;
            Q1=makeQuery(id+"F2.opExtrude","CAP_EDGE",EDGE,{"disambiguationData":[OSD([sQuery(id+"F1.wireOp",EDGE,"E18.left")])],"isStart":true});
            var Q2;
            Q2=makeQuery(id+"F2.opExtrude","CAP_EDGE",EDGE,{"disambiguationData":[OSD([sQuery(id+"F1.wireOp",EDGE,"E19.left")])],"isStart":true});
            var Q3;
            Q3=makeQuery(id+"F2.opExtrude","CAP_EDGE",EDGE,{"disambiguationData":[OSD([sQuery(id+"F1.wireOp",EDGE,"E19.right")])],"isStart":true});
            var Q4;
            Q4=makeQuery(id+"F2.opExtrude","CAP_EDGE",EDGE,{"disambiguationData":[OSD([sQuery(id+"F1.wireOp",EDGE,"E20.left")])],"isStart":true});
            var Q5;
            Q5=makeQuery(id+"F2.opExtrude","CAP_EDGE",EDGE,{"disambiguationData":[OSD([sQuery(id+"F1.wireOp",EDGE,"E20.right")])],"isStart":true});
            var Q6;
            Q6=makeQuery(id+"F2.opExtrude","CAP_EDGE",EDGE,{"disambiguationData":[OSD([sQuery(id+"F1.wireOp",EDGE,"E14.right")])],"isStart":true});
            var Q7;
            Q7=makeQuery(id+"F2.opExtrude","CAP_EDGE",EDGE,{"disambiguationData":[OSD([sQuery(id+"F1.wireOp",EDGE,"E14.left")])],"isStart":true});
            var Q8;
            Q8=makeQuery(id+"F2.opExtrude","CAP_EDGE",EDGE,{"disambiguationData":[OSD([sQuery(id+"F1.wireOp",EDGE,"E13.right")])],"isStart":true});
            var Q9;
            Q9=makeQuery(id+"F2.opExtrude","CAP_EDGE",EDGE,{"disambiguationData":[OSD([sQuery(id+"F1.wireOp",EDGE,"E13.left")])],"isStart":true});
            var Q10;
            Q10=makeQuery(id+"F2.opExtrude","CAP_EDGE",EDGE,{"disambiguationData":[OSD([sQuery(id+"F1.wireOp",EDGE,"E12.right")])],"isStart":true});
            var Q11;
            Q11=makeQuery(id+"F2.opExtrude","CAP_EDGE",EDGE,{"disambiguationData":[OSD([sQuery(id+"F1.wireOp",EDGE,"E12.left")])],"isStart":true});
            var Q12;
            Q12=makeQuery(id+"F2.opExtrude","CAP_EDGE",EDGE,{"disambiguationData":[OSD([sQuery(id+"F1.wireOp",EDGE,"E17.top")])],"isStart":true});
            var Q13;
            Q13=makeQuery(id+"F2.opExtrude","CAP_EDGE",EDGE,{"disambiguationData":[OSD([sQuery(id+"F1.wireOp",EDGE,"E11.left")])],"isStart":true});
            var Q14;
            Q14=makeQuery(id+"F2.opExtrude","CAP_EDGE",EDGE,{"disambiguationData":[OSD([sQuery(id+"F1.wireOp",EDGE,"E126.trimOffspring")])],"isStart":true});
            var Q15;
            Q15=makeQuery(id+"F2.opExtrude","CAP_EDGE",EDGE,{"disambiguationData":[OSD([sQuery(id+"F1.wireOp",EDGE,"E16.top")])],"isStart":true});
            var Q16;
            Q16=makeQuery(id+"F2.opExtrude","CAP_EDGE",EDGE,{"disambiguationData":[OSD([sQuery(id+"F1.wireOp",EDGE,"E11.right")])],"isStart":true});
            var Q17;
            Q17=makeQuery(id+"F2.opExtrude","CAP_EDGE",EDGE,{"disambiguationData":[OSD([sQuery(id+"F1.wireOp",EDGE,"E134.trimOffspring")])],"isStart":true});
            var Q18;
            Q18=makeQuery(id+"F2.opExtrude","CAP_EDGE",EDGE,{"disambiguationData":[OSD([sQuery(id+"F1.wireOp",EDGE,"E133.trimOffspring")])],"isStart":true});
            var Q19;
            Q19=makeQuery(id+"F2.opExtrude","CAP_EDGE",EDGE,{"disambiguationData":[OSD([sQuery(id+"F1.wireOp",EDGE,"E10.top")])],"isStart":true});
            chamfer(context, id + "F4", {"entities" : qUnion([Q0, Q1, Q2, Q3, Q4, Q5, Q6, Q7, Q8, Q9, Q10, Q11, Q12, Q13, Q14, Q15, Q16, Q17, Q18, Q19]), "width" : .7 * mm, "tangentPropagation" : true});
        }
        {
            var Q0;
            Q0=makeQuery(id+"F2.opExtrude","CAP_EDGE",EDGE,{"disambiguationData":[OSD([sQuery(id+"F1.wireOp",EDGE,"E10.bottom")])],"isStart":true});
            var Q1;
            Q1=makeQuery(id+"F2.opExtrude","CAP_EDGE",EDGE,{"disambiguationData":[OSD([sQuery(id+"F1.wireOp",EDGE,"E141.trimOffspring")])],"isStart":true});
            var Q2;
            Q2=makeQuery(id+"F2.opExtrude","CAP_EDGE",EDGE,{"disambiguationData":[OSD([sQuery(id+"F1.wireOp",EDGE,"E21.left")])],"isStart":true});
            var Q3;
            Q3=makeQuery(id+"F2.opExtrude","CAP_EDGE",EDGE,{"disambiguationData":[OSD([sQuery(id+"F1.wireOp",EDGE,"E21.right")])],"isStart":true});
            var Q4;
            Q4=makeQuery(id+"F2.opExtrude","CAP_EDGE",EDGE,{"disambiguationData":[OSD([sQuery(id+"F1.wireOp",EDGE,"E135.trimOffspring")])],"isStart":true});
            var Q5;
            Q5=makeQuery(id+"F2.opExtrude","CAP_EDGE",EDGE,{"disambiguationData":[OSD([sQuery(id+"F1.wireOp",EDGE,"E137.trimOffspring")])],"isStart":true});
            var Q6;
            Q6=makeQuery(id+"F2.opExtrude","CAP_EDGE",EDGE,{"disambiguationData":[OSD([sQuery(id+"F1.wireOp",EDGE,"E22.left")])],"isStart":true});
            var Q7;
            Q7=makeQuery(id+"F2.opExtrude","CAP_EDGE",EDGE,{"disambiguationData":[OSD([sQuery(id+"F1.wireOp",EDGE,"E22.right")])],"isStart":true});
            var Q8;
            Q8=makeQuery(id+"F2.opExtrude","CAP_EDGE",EDGE,{"disambiguationData":[OSD([sQuery(id+"F1.wireOp",EDGE,"E136.trimOffspring")])],"isStart":true});
            var Q9;
            Q9=makeQuery(id+"F2.opExtrude","CAP_EDGE",EDGE,{"disambiguationData":[OSD([sQuery(id+"F1.wireOp",EDGE,"E230.trimOffspring")])],"isStart":true});
            var Q10;
            Q10=makeQuery(id+"F2.opExtrude","CAP_EDGE",EDGE,{"disambiguationData":[OSD([sQuery(id+"F1.wireOp",EDGE,"E23.left")])],"isStart":true});
            var Q11;
            Q11=makeQuery(id+"F2.opExtrude","CAP_EDGE",EDGE,{"disambiguationData":[OSD([sQuery(id+"F1.wireOp",EDGE,"E23.right")])],"isStart":true});
            var Q12;
            Q12=makeQuery(id+"F2.opExtrude","CAP_EDGE",EDGE,{"disambiguationData":[OSD([sQuery(id+"F1.wireOp",EDGE,"E231.trimOffspring")])],"isStart":true});
            var Q13;
            Q13=makeQuery(id+"F2.opExtrude","CAP_EDGE",EDGE,{"disambiguationData":[OSD([sQuery(id+"F1.wireOp",EDGE,"E143.trimOffspring")])],"isStart":true});
            var Q14;
            Q14=makeQuery(id+"F2.opExtrude","CAP_EDGE",EDGE,{"disambiguationData":[OSD([sQuery(id+"F1.wireOp",EDGE,"E24.left")])],"isStart":true});
            var Q15;
            Q15=makeQuery(id+"F2.opExtrude","CAP_EDGE",EDGE,{"disambiguationData":[OSD([sQuery(id+"F1.wireOp",EDGE,"E24.right")])],"isStart":true});
            var Q16;
            Q16=makeQuery(id+"F2.opExtrude","CAP_EDGE",EDGE,{"disambiguationData":[OSD([sQuery(id+"F1.wireOp",EDGE,"E152.trimOffspring")])],"isStart":true});
            var Q17;
            Q17=makeQuery(id+"F2.opExtrude","CAP_EDGE",EDGE,{"disambiguationData":[OSD([sQuery(id+"F1.wireOp",EDGE,"E144.trimOffspring")])],"isStart":true});
            var Q18;
            Q18=makeQuery(id+"F2.opExtrude","CAP_EDGE",EDGE,{"disambiguationData":[OSD([sQuery(id+"F1.wireOp",EDGE,"E25.left")])],"isStart":true});
            var Q19;
            Q19=makeQuery(id+"F2.opExtrude","CAP_EDGE",EDGE,{"disambiguationData":[OSD([sQuery(id+"F1.wireOp",EDGE,"E25.right")])],"isStart":true});
            var Q20;
            Q20=makeQuery(id+"F2.opExtrude","CAP_EDGE",EDGE,{"disambiguationData":[OSD([sQuery(id+"F1.wireOp",EDGE,"E151.trimOffspring")])],"isStart":true});
            var Q21;
            Q21=makeQuery(id+"F2.opExtrude","CAP_EDGE",EDGE,{"disambiguationData":[OSD([sQuery(id+"F1.wireOp",EDGE,"E146.trimOffspring")])],"isStart":true});
            var Q22;
            Q22=makeQuery(id+"F2.opExtrude","CAP_EDGE",EDGE,{"disambiguationData":[OSD([sQuery(id+"F1.wireOp",EDGE,"E26.left")])],"isStart":true});
            var Q23;
            Q23=makeQuery(id+"F2.opExtrude","CAP_EDGE",EDGE,{"disambiguationData":[OSD([sQuery(id+"F1.wireOp",EDGE,"E26.right")])],"isStart":true});
            var Q24;
            Q24=makeQuery(id+"F2.opExtrude","CAP_EDGE",EDGE,{"disambiguationData":[OSD([sQuery(id+"F1.wireOp",EDGE,"E150.trimOffspring")])],"isStart":true});
            var Q25;
            Q25=makeQuery(id+"F2.opExtrude","CAP_EDGE",EDGE,{"disambiguationData":[OSD([sQuery(id+"F1.wireOp",EDGE,"E154.trimOffspring")])],"isStart":true});
            var Q26;
            Q26=makeQuery(id+"F2.opExtrude","CAP_EDGE",EDGE,{"disambiguationData":[OSD([sQuery(id+"F1.wireOp",EDGE,"E27.left")])],"isStart":true});
            var Q27;
            Q27=makeQuery(id+"F2.opExtrude","CAP_EDGE",EDGE,{"disambiguationData":[OSD([sQuery(id+"F1.wireOp",EDGE,"E27.right")])],"isStart":true});
            var Q28;
            Q28=makeQuery(id+"F2.opExtrude","CAP_EDGE",EDGE,{"disambiguationData":[OSD([sQuery(id+"F1.wireOp",EDGE,"E149.trimOffspring")])],"isStart":true});
            var Q29;
            Q29=makeQuery(id+"F2.opExtrude","CAP_EDGE",EDGE,{"disambiguationData":[OSD([sQuery(id+"F1.wireOp",EDGE,"E155.trimOffspring")])],"isStart":true});
            var Q30;
            Q30=makeQuery(id+"F2.opExtrude","CAP_EDGE",EDGE,{"disambiguationData":[OSD([sQuery(id+"F1.wireOp",EDGE,"E28.left")])],"isStart":true});
            var Q31;
            Q31=makeQuery(id+"F2.opExtrude","CAP_EDGE",EDGE,{"disambiguationData":[OSD([sQuery(id+"F1.wireOp",EDGE,"E28.right")])],"isStart":true});
            var Q32;
            Q32=makeQuery(id+"F2.opExtrude","CAP_EDGE",EDGE,{"disambiguationData":[OSD([sQuery(id+"F1.wireOp",EDGE,"E156.trimOffspring")])],"isStart":true});
            var Q33;
            Q33=makeQuery(id+"F2.opExtrude","CAP_EDGE",EDGE,{"disambiguationData":[OSD([sQuery(id+"F1.wireOp",EDGE,"E158.trimOffspring")])],"isStart":true});
            var Q34;
            Q34=makeQuery(id+"F2.opExtrude","CAP_EDGE",EDGE,{"disambiguationData":[OSD([sQuery(id+"F1.wireOp",EDGE,"E130.trimOffspring")])],"isStart":true});
            var Q35;
            Q35=makeQuery(id+"F2.opExtrude","CAP_EDGE",EDGE,{"disambiguationData":[OSD([sQuery(id+"F1.wireOp",EDGE,"E129.trimOffspring")])],"isStart":true});
            var Q36;
            Q36=makeQuery(id+"F2.opExtrude","CAP_EDGE",EDGE,{"disambiguationData":[OSD([sQuery(id+"F1.wireOp",EDGE,"E29.right")])],"isStart":true});
            var Q37;
            Q37=makeQuery(id+"F2.opExtrude","CAP_EDGE",EDGE,{"disambiguationData":[OSD([sQuery(id+"F1.wireOp",EDGE,"E166.trimOffspring")])],"isStart":true});
            var Q38;
            Q38=makeQuery(id+"F2.opExtrude","CAP_EDGE",EDGE,{"disambiguationData":[OSD([sQuery(id+"F1.wireOp",EDGE,"E30.left")])],"isStart":true});
            var Q39;
            Q39=makeQuery(id+"F2.opExtrude","CAP_EDGE",EDGE,{"disambiguationData":[OSD([sQuery(id+"F1.wireOp",EDGE,"E164.trimOffspring")])],"isStart":true});
            var Q40;
            Q40=makeQuery(id+"F2.opExtrude","CAP_EDGE",EDGE,{"disambiguationData":[OSD([sQuery(id+"F1.wireOp",EDGE,"E30.right")])],"isStart":true});
            var Q41;
            Q41=makeQuery(id+"F2.opExtrude","CAP_EDGE",EDGE,{"disambiguationData":[OSD([sQuery(id+"F1.wireOp",EDGE,"E165.trimOffspring")])],"isStart":true});
            var Q42;
            Q42=makeQuery(id+"F2.opExtrude","CAP_EDGE",EDGE,{"disambiguationData":[OSD([sQuery(id+"F1.wireOp",EDGE,"E161.trimOffspring")])],"isStart":true});
            var Q43;
            Q43=makeQuery(id+"F2.opExtrude","CAP_EDGE",EDGE,{"disambiguationData":[OSD([sQuery(id+"F1.wireOp",EDGE,"E31.left")])],"isStart":true});
            var Q44;
            Q44=makeQuery(id+"F2.opExtrude","CAP_EDGE",EDGE,{"disambiguationData":[OSD([sQuery(id+"F1.wireOp",EDGE,"E31.right")])],"isStart":true});
            var Q45;
            Q45=makeQuery(id+"F2.opExtrude","CAP_EDGE",EDGE,{"disambiguationData":[OSD([sQuery(id+"F1.wireOp",EDGE,"E162.trimOffspring")])],"isStart":true});
            var Q46;
            Q46=makeQuery(id+"F2.opExtrude","CAP_EDGE",EDGE,{"disambiguationData":[OSD([sQuery(id+"F1.wireOp",EDGE,"E9.top")])],"isStart":true});
            chamfer(context, id + "F5", {"entities" : qUnion([Q0, Q1, Q2, Q3, Q4, Q5, Q6, Q7, Q8, Q9, Q10, Q11, Q12, Q13, Q14, Q15, Q16, Q17, Q18, Q19, Q20, Q21, Q22, Q23, Q24, Q25, Q26, Q27, Q28, Q29, Q30, Q31, Q32, Q33, Q34, Q35, Q36, Q37, Q38, Q39, Q40, Q41, Q42, Q43, Q44, Q45, Q46]), "width" : .7 * mm, "tangentPropagation" : true});
        }
        {
            var Q0;
            Q0=makeQuery(id+"F2.opExtrude","CAP_EDGE",EDGE,{"disambiguationData":[OSD([sQuery(id+"F1.wireOp",EDGE,"E140.trimOffspring")])],"isStart":true});
            var Q1;
            Q1=makeQuery(id+"F2.opExtrude","CAP_EDGE",EDGE,{"disambiguationData":[OSD([sQuery(id+"F1.wireOp",EDGE,"E32.left")])],"isStart":true});
            var Q2;
            Q2=makeQuery(id+"F2.opExtrude","CAP_EDGE",EDGE,{"disambiguationData":[OSD([sQuery(id+"F1.wireOp",EDGE,"E8.top")])],"isStart":true});
            var Q3;
            Q3=makeQuery(id+"F2.opExtrude","CAP_EDGE",EDGE,{"disambiguationData":[OSD([sQuery(id+"F1.wireOp",EDGE,"E32.right")])],"isStart":true});
            var Q4;
            Q4=makeQuery(id+"F2.opExtrude","CAP_EDGE",EDGE,{"disambiguationData":[OSD([sQuery(id+"F1.wireOp",EDGE,"E139.trimOffspring")])],"isStart":true});
            var Q5;
            Q5=makeQuery(id+"F2.opExtrude","CAP_EDGE",EDGE,{"disambiguationData":[OSD([sQuery(id+"F1.wireOp",EDGE,"E212.trimOffspring")])],"isStart":true});
            var Q6;
            Q6=makeQuery(id+"F2.opExtrude","CAP_EDGE",EDGE,{"disambiguationData":[OSD([sQuery(id+"F1.wireOp",EDGE,"E33.left")])],"isStart":true});
            var Q7;
            Q7=makeQuery(id+"F2.opExtrude","CAP_EDGE",EDGE,{"disambiguationData":[OSD([sQuery(id+"F1.wireOp",EDGE,"E33.right")])],"isStart":true});
            var Q8;
            Q8=makeQuery(id+"F2.opExtrude","CAP_EDGE",EDGE,{"disambiguationData":[OSD([sQuery(id+"F1.wireOp",EDGE,"E138.trimOffspring")])],"isStart":true});
            var Q9;
            Q9=makeQuery(id+"F2.opExtrude","CAP_EDGE",EDGE,{"disambiguationData":[OSD([sQuery(id+"F1.wireOp",EDGE,"E211.trimOffspring")])],"isStart":true});
            var Q10;
            Q10=makeQuery(id+"F2.opExtrude","CAP_EDGE",EDGE,{"disambiguationData":[OSD([sQuery(id+"F1.wireOp",EDGE,"E34.left")])],"isStart":true});
            var Q11;
            Q11=makeQuery(id+"F2.opExtrude","CAP_EDGE",EDGE,{"disambiguationData":[OSD([sQuery(id+"F1.wireOp",EDGE,"E34.right")])],"isStart":true});
            var Q12;
            Q12=makeQuery(id+"F2.opExtrude","CAP_EDGE",EDGE,{"disambiguationData":[OSD([sQuery(id+"F1.wireOp",EDGE,"E142.trimOffspring")])],"isStart":true});
            var Q13;
            Q13=makeQuery(id+"F2.opExtrude","CAP_EDGE",EDGE,{"disambiguationData":[OSD([sQuery(id+"F1.wireOp",EDGE,"E210.trimOffspring")])],"isStart":true});
            var Q14;
            Q14=makeQuery(id+"F2.opExtrude","CAP_EDGE",EDGE,{"disambiguationData":[OSD([sQuery(id+"F1.wireOp",EDGE,"E35.left")])],"isStart":true});
            var Q15;
            Q15=makeQuery(id+"F2.opExtrude","CAP_EDGE",EDGE,{"disambiguationData":[OSD([sQuery(id+"F1.wireOp",EDGE,"E35.right")])],"isStart":true});
            var Q16;
            Q16=makeQuery(id+"F2.opExtrude","CAP_EDGE",EDGE,{"disambiguationData":[OSD([sQuery(id+"F1.wireOp",EDGE,"E153.trimOffspring")])],"isStart":true});
            var Q17;
            Q17=makeQuery(id+"F2.opExtrude","CAP_EDGE",EDGE,{"disambiguationData":[OSD([sQuery(id+"F1.wireOp",EDGE,"E209.trimOffspring")])],"isStart":true});
            var Q18;
            Q18=makeQuery(id+"F2.opExtrude","CAP_EDGE",EDGE,{"disambiguationData":[OSD([sQuery(id+"F1.wireOp",EDGE,"E36.left")])],"isStart":true});
            var Q19;
            Q19=makeQuery(id+"F2.opExtrude","CAP_EDGE",EDGE,{"disambiguationData":[OSD([sQuery(id+"F1.wireOp",EDGE,"E36.right")])],"isStart":true});
            var Q20;
            Q20=makeQuery(id+"F2.opExtrude","CAP_EDGE",EDGE,{"disambiguationData":[OSD([sQuery(id+"F1.wireOp",EDGE,"E145.trimOffspring")])],"isStart":true});
            var Q21;
            Q21=makeQuery(id+"F2.opExtrude","CAP_EDGE",EDGE,{"disambiguationData":[OSD([sQuery(id+"F1.wireOp",EDGE,"E178.trimOffspring")])],"isStart":true});
            var Q22;
            Q22=makeQuery(id+"F2.opExtrude","CAP_EDGE",EDGE,{"disambiguationData":[OSD([sQuery(id+"F1.wireOp",EDGE,"E37.left")])],"isStart":true});
            var Q23;
            Q23=makeQuery(id+"F2.opExtrude","CAP_EDGE",EDGE,{"disambiguationData":[OSD([sQuery(id+"F1.wireOp",EDGE,"E37.right")])],"isStart":true});
            var Q24;
            Q24=makeQuery(id+"F2.opExtrude","CAP_EDGE",EDGE,{"disambiguationData":[OSD([sQuery(id+"F1.wireOp",EDGE,"E147.trimOffspring")])],"isStart":true});
            var Q25;
            Q25=makeQuery(id+"F2.opExtrude","CAP_EDGE",EDGE,{"disambiguationData":[OSD([sQuery(id+"F1.wireOp",EDGE,"E177.trimOffspring")])],"isStart":true});
            var Q26;
            Q26=makeQuery(id+"F2.opExtrude","CAP_EDGE",EDGE,{"disambiguationData":[OSD([sQuery(id+"F1.wireOp",EDGE,"E38.left")])],"isStart":true});
            var Q27;
            Q27=makeQuery(id+"F2.opExtrude","CAP_EDGE",EDGE,{"disambiguationData":[OSD([sQuery(id+"F1.wireOp",EDGE,"E38.right")])],"isStart":true});
            var Q28;
            Q28=makeQuery(id+"F2.opExtrude","CAP_EDGE",EDGE,{"disambiguationData":[OSD([sQuery(id+"F1.wireOp",EDGE,"E148.trimOffspring")])],"isStart":true});
            var Q29;
            Q29=makeQuery(id+"F2.opExtrude","CAP_EDGE",EDGE,{"disambiguationData":[OSD([sQuery(id+"F1.wireOp",EDGE,"E176.trimOffspring")])],"isStart":true});
            var Q30;
            Q30=makeQuery(id+"F2.opExtrude","CAP_EDGE",EDGE,{"disambiguationData":[OSD([sQuery(id+"F1.wireOp",EDGE,"E39.left")])],"isStart":true});
            var Q31;
            Q31=makeQuery(id+"F2.opExtrude","CAP_EDGE",EDGE,{"disambiguationData":[OSD([sQuery(id+"F1.wireOp",EDGE,"E39.right")])],"isStart":true});
            var Q32;
            Q32=makeQuery(id+"F2.opExtrude","CAP_EDGE",EDGE,{"disambiguationData":[OSD([sQuery(id+"F1.wireOp",EDGE,"E157.trimOffspring")])],"isStart":true});
            var Q33;
            Q33=makeQuery(id+"F2.opExtrude","CAP_EDGE",EDGE,{"disambiguationData":[OSD([sQuery(id+"F1.wireOp",EDGE,"E40.left")])],"isStart":true});
            var Q34;
            Q34=makeQuery(id+"F2.opExtrude","CAP_EDGE",EDGE,{"disambiguationData":[OSD([sQuery(id+"F1.wireOp",EDGE,"E175.trimOffspring")])],"isStart":true});
            var Q35;
            Q35=makeQuery(id+"F2.opExtrude","CAP_EDGE",EDGE,{"disambiguationData":[OSD([sQuery(id+"F1.wireOp",EDGE,"E40.right")])],"isStart":true});
            var Q36;
            Q36=makeQuery(id+"F2.opExtrude","CAP_EDGE",EDGE,{"disambiguationData":[OSD([sQuery(id+"F1.wireOp",EDGE,"E159.trimOffspring")])],"isStart":true});
            var Q37;
            Q37=makeQuery(id+"F2.opExtrude","CAP_EDGE",EDGE,{"disambiguationData":[OSD([sQuery(id+"F1.wireOp",EDGE,"E41.left")])],"isStart":true});
            var Q38;
            Q38=makeQuery(id+"F2.opExtrude","CAP_EDGE",EDGE,{"disambiguationData":[OSD([sQuery(id+"F1.wireOp",EDGE,"E173.trimOffspring")])],"isStart":true});
            var Q39;
            Q39=makeQuery(id+"F2.opExtrude","CAP_EDGE",EDGE,{"disambiguationData":[OSD([sQuery(id+"F1.wireOp",EDGE,"E41.right")])],"isStart":true});
            var Q40;
            Q40=makeQuery(id+"F2.opExtrude","CAP_EDGE",EDGE,{"disambiguationData":[OSD([sQuery(id+"F1.wireOp",EDGE,"E160.trimOffspring")])],"isStart":true});
            var Q41;
            Q41=makeQuery(id+"F2.opExtrude","CAP_EDGE",EDGE,{"disambiguationData":[OSD([sQuery(id+"F1.wireOp",EDGE,"E42.left")])],"isStart":true});
            var Q42;
            Q42=makeQuery(id+"F2.opExtrude","CAP_EDGE",EDGE,{"disambiguationData":[OSD([sQuery(id+"F1.wireOp",EDGE,"E171.trimOffspring")])],"isStart":true});
            var Q43;
            Q43=makeQuery(id+"F2.opExtrude","CAP_EDGE",EDGE,{"disambiguationData":[OSD([sQuery(id+"F1.wireOp",EDGE,"E42.right")])],"isStart":true});
            var Q44;
            Q44=makeQuery(id+"F2.opExtrude","CAP_EDGE",EDGE,{"disambiguationData":[OSD([sQuery(id+"F1.wireOp",EDGE,"E163.trimOffspring")])],"isStart":true});
            var Q45;
            Q45=makeQuery(id+"F2.opExtrude","CAP_EDGE",EDGE,{"disambiguationData":[OSD([sQuery(id+"F1.wireOp",EDGE,"E43.left")])],"isStart":true});
            var Q46;
            Q46=makeQuery(id+"F2.opExtrude","CAP_EDGE",EDGE,{"disambiguationData":[OSD([sQuery(id+"F1.wireOp",EDGE,"E174.trimOffspring")])],"isStart":true});
            var Q47;
            Q47=makeQuery(id+"F2.opExtrude","CAP_EDGE",EDGE,{"disambiguationData":[OSD([sQuery(id+"F1.wireOp",EDGE,"E43.right")])],"isStart":true});
            var Q48;
            Q48=makeQuery(id+"F2.opExtrude","CAP_EDGE",EDGE,{"disambiguationData":[OSD([sQuery(id+"F1.wireOp",EDGE,"E9.bottom")])],"isStart":true});
            var Q49;
            Q49=makeQuery(id+"F2.opExtrude","CAP_EDGE",EDGE,{"disambiguationData":[OSD([sQuery(id+"F1.wireOp",EDGE,"E168.trimOffspring")])],"isStart":true});
            chamfer(context, id + "F6", {"entities" : qUnion([Q0, Q1, Q2, Q3, Q4, Q5, Q6, Q7, Q8, Q9, Q10, Q11, Q12, Q13, Q14, Q15, Q16, Q17, Q18, Q19, Q20, Q21, Q22, Q23, Q24, Q25, Q26, Q27, Q28, Q29, Q30, Q31, Q32, Q33, Q34, Q35, Q36, Q37, Q38, Q39, Q40, Q41, Q42, Q43, Q44, Q45, Q46, Q47, Q48, Q49]), "width" : .7 * mm, "tangentPropagation" : true});
        }
        {
            var Q0;
            Q0=makeQuery(id+"F2.opExtrude","CAP_EDGE",EDGE,{"disambiguationData":[OSD([sQuery(id+"F1.wireOp",EDGE,"E8.bottom")])],"isStart":true});
            var Q1;
            Q1=makeQuery(id+"F2.opExtrude","CAP_EDGE",EDGE,{"disambiguationData":[OSD([sQuery(id+"F1.wireOp",EDGE,"E205.trimOffspring")])],"isStart":true});
            var Q2;
            Q2=makeQuery(id+"F2.opExtrude","CAP_EDGE",EDGE,{"disambiguationData":[OSD([sQuery(id+"F1.wireOp",EDGE,"E56.right")])],"isStart":true});
            var Q3;
            Q3=makeQuery(id+"F2.opExtrude","CAP_EDGE",EDGE,{"disambiguationData":[OSD([sQuery(id+"F1.wireOp",EDGE,"E56.left")])],"isStart":true});
            var Q4;
            Q4=makeQuery(id+"F2.opExtrude","CAP_EDGE",EDGE,{"disambiguationData":[OSD([sQuery(id+"F1.wireOp",EDGE,"E195.trimOffspring")])],"isStart":true});
            var Q5;
            Q5=makeQuery(id+"F2.opExtrude","CAP_EDGE",EDGE,{"disambiguationData":[OSD([sQuery(id+"F1.wireOp",EDGE,"E207.trimOffspring")])],"isStart":true});
            var Q6;
            Q6=makeQuery(id+"F2.opExtrude","CAP_EDGE",EDGE,{"disambiguationData":[OSD([sQuery(id+"F1.wireOp",EDGE,"E55.left")])],"isStart":true});
            var Q7;
            Q7=makeQuery(id+"F2.opExtrude","CAP_EDGE",EDGE,{"disambiguationData":[OSD([sQuery(id+"F1.wireOp",EDGE,"E55.right")])],"isStart":true});
            var Q8;
            Q8=makeQuery(id+"F2.opExtrude","CAP_EDGE",EDGE,{"disambiguationData":[OSD([sQuery(id+"F1.wireOp",EDGE,"E206.trimOffspring")])],"isStart":true});
            var Q9;
            Q9=makeQuery(id+"F2.opExtrude","CAP_EDGE",EDGE,{"disambiguationData":[OSD([sQuery(id+"F1.wireOp",EDGE,"E54.left")])],"isStart":true});
            var Q10;
            Q10=makeQuery(id+"F2.opExtrude","CAP_EDGE",EDGE,{"disambiguationData":[OSD([sQuery(id+"F1.wireOp",EDGE,"E196.trimOffspring")])],"isStart":true});
            var Q11;
            Q11=makeQuery(id+"F2.opExtrude","CAP_EDGE",EDGE,{"disambiguationData":[OSD([sQuery(id+"F1.wireOp",EDGE,"E54.right")])],"isStart":true});
            var Q12;
            Q12=makeQuery(id+"F2.opExtrude","CAP_EDGE",EDGE,{"disambiguationData":[OSD([sQuery(id+"F1.wireOp",EDGE,"E194.trimOffspring")])],"isStart":true});
            var Q13;
            Q13=makeQuery(id+"F2.opExtrude","CAP_EDGE",EDGE,{"disambiguationData":[OSD([sQuery(id+"F1.wireOp",EDGE,"E53.left")])],"isStart":true});
            var Q14;
            Q14=makeQuery(id+"F2.opExtrude","CAP_EDGE",EDGE,{"disambiguationData":[OSD([sQuery(id+"F1.wireOp",EDGE,"E197.trimOffspring")])],"isStart":true});
            var Q15;
            Q15=makeQuery(id+"F2.opExtrude","CAP_EDGE",EDGE,{"disambiguationData":[OSD([sQuery(id+"F1.wireOp",EDGE,"E53.right")])],"isStart":true});
            var Q16;
            Q16=makeQuery(id+"F2.opExtrude","CAP_EDGE",EDGE,{"disambiguationData":[OSD([sQuery(id+"F1.wireOp",EDGE,"E193.trimOffspring")])],"isStart":true});
            var Q17;
            Q17=makeQuery(id+"F2.opExtrude","CAP_EDGE",EDGE,{"disambiguationData":[OSD([sQuery(id+"F1.wireOp",EDGE,"E52.left")])],"isStart":true});
            var Q18;
            Q18=makeQuery(id+"F2.opExtrude","CAP_EDGE",EDGE,{"disambiguationData":[OSD([sQuery(id+"F1.wireOp",EDGE,"E179.trimOffspring")])],"isStart":true});
            var Q19;
            Q19=makeQuery(id+"F2.opExtrude","CAP_EDGE",EDGE,{"disambiguationData":[OSD([sQuery(id+"F1.wireOp",EDGE,"E52.right")])],"isStart":true});
            var Q20;
            Q20=makeQuery(id+"F2.opExtrude","CAP_EDGE",EDGE,{"disambiguationData":[OSD([sQuery(id+"F1.wireOp",EDGE,"E191.trimOffspring")])],"isStart":true});
            var Q21;
            Q21=makeQuery(id+"F2.opExtrude","CAP_EDGE",EDGE,{"disambiguationData":[OSD([sQuery(id+"F1.wireOp",EDGE,"E51.left")])],"isStart":true});
            var Q22;
            Q22=makeQuery(id+"F2.opExtrude","CAP_EDGE",EDGE,{"disambiguationData":[OSD([sQuery(id+"F1.wireOp",EDGE,"E181.trimOffspring")])],"isStart":true});
            var Q23;
            Q23=makeQuery(id+"F2.opExtrude","CAP_EDGE",EDGE,{"disambiguationData":[OSD([sQuery(id+"F1.wireOp",EDGE,"E51.right")])],"isStart":true});
            var Q24;
            Q24=makeQuery(id+"F2.opExtrude","CAP_EDGE",EDGE,{"disambiguationData":[OSD([sQuery(id+"F1.wireOp",EDGE,"E182.trimOffspring")])],"isStart":true});
            var Q25;
            Q25=makeQuery(id+"F2.opExtrude","CAP_EDGE",EDGE,{"disambiguationData":[OSD([sQuery(id+"F1.wireOp",EDGE,"E89")])],"isStart":true});
            var Q26;
            Q26=makeQuery(id+"F2.opExtrude","CAP_EDGE",EDGE,{"disambiguationData":[OSD([sQuery(id+"F1.wireOp",EDGE,"E184.trimOffspring")])],"isStart":true});
            var Q27;
            Q27=makeQuery(id+"F2.opExtrude","CAP_EDGE",EDGE,{"disambiguationData":[OSD([sQuery(id+"F1.wireOp",EDGE,"E50.right")])],"isStart":true});
            var Q28;
            Q28=makeQuery(id+"F2.opExtrude","CAP_EDGE",EDGE,{"disambiguationData":[OSD([sQuery(id+"F1.wireOp",EDGE,"E183.trimOffspring")])],"isStart":true});
            var Q29;
            Q29=makeQuery(id+"F2.opExtrude","CAP_EDGE",EDGE,{"disambiguationData":[OSD([sQuery(id+"F1.wireOp",EDGE,"E49.left")])],"isStart":true});
            var Q30;
            Q30=makeQuery(id+"F2.opExtrude","CAP_EDGE",EDGE,{"disambiguationData":[OSD([sQuery(id+"F1.wireOp",EDGE,"E187.trimOffspring")])],"isStart":true});
            var Q31;
            Q31=makeQuery(id+"F2.opExtrude","CAP_EDGE",EDGE,{"disambiguationData":[OSD([sQuery(id+"F1.wireOp",EDGE,"E49.right")])],"isStart":true});
            var Q32;
            Q32=makeQuery(id+"F2.opExtrude","CAP_EDGE",EDGE,{"disambiguationData":[OSD([sQuery(id+"F1.wireOp",EDGE,"E188.trimOffspring")])],"isStart":true});
            var Q33;
            Q33=makeQuery(id+"F2.opExtrude","CAP_EDGE",EDGE,{"disambiguationData":[OSD([sQuery(id+"F1.wireOp",EDGE,"E48.left")])],"isStart":true});
            var Q34;
            Q34=makeQuery(id+"F2.opExtrude","CAP_EDGE",EDGE,{"disambiguationData":[OSD([sQuery(id+"F1.wireOp",EDGE,"E189.trimOffspring")])],"isStart":true});
            var Q35;
            Q35=makeQuery(id+"F2.opExtrude","CAP_EDGE",EDGE,{"disambiguationData":[OSD([sQuery(id+"F1.wireOp",EDGE,"E48.right")])],"isStart":true});
            var Q36;
            Q36=makeQuery(id+"F2.opExtrude","CAP_EDGE",EDGE,{"disambiguationData":[OSD([sQuery(id+"F1.wireOp",EDGE,"E190.trimOffspring")])],"isStart":true});
            var Q37;
            Q37=makeQuery(id+"F2.opExtrude","CAP_EDGE",EDGE,{"disambiguationData":[OSD([sQuery(id+"F1.wireOp",EDGE,"E47.left")])],"isStart":true});
            var Q38;
            Q38=makeQuery(id+"F2.opExtrude","CAP_EDGE",EDGE,{"disambiguationData":[OSD([sQuery(id+"F1.wireOp",EDGE,"E221.trimOffspring")])],"isStart":true});
            var Q39;
            Q39=makeQuery(id+"F2.opExtrude","CAP_EDGE",EDGE,{"disambiguationData":[OSD([sQuery(id+"F1.wireOp",EDGE,"E47.right")])],"isStart":true});
            var Q40;
            Q40=makeQuery(id+"F2.opExtrude","CAP_EDGE",EDGE,{"disambiguationData":[OSD([sQuery(id+"F1.wireOp",EDGE,"E172.trimOffspring")])],"isStart":true});
            var Q41;
            Q41=makeQuery(id+"F2.opExtrude","CAP_EDGE",EDGE,{"disambiguationData":[OSD([sQuery(id+"F1.wireOp",EDGE,"E46.left")])],"isStart":true});
            var Q42;
            Q42=makeQuery(id+"F2.opExtrude","CAP_EDGE",EDGE,{"disambiguationData":[OSD([sQuery(id+"F1.wireOp",EDGE,"E229.trimOffspring")])],"isStart":true});
            var Q43;
            Q43=makeQuery(id+"F2.opExtrude","CAP_EDGE",EDGE,{"disambiguationData":[OSD([sQuery(id+"F1.wireOp",EDGE,"E170.trimOffspring")])],"isStart":true});
            var Q44;
            Q44=makeQuery(id+"F2.opExtrude","CAP_EDGE",EDGE,{"disambiguationData":[OSD([sQuery(id+"F1.wireOp",EDGE,"E46.right")])],"isStart":true});
            var Q45;
            Q45=makeQuery(id+"F2.opExtrude","CAP_EDGE",EDGE,{"disambiguationData":[OSD([sQuery(id+"F1.wireOp",EDGE,"E222.trimOffspring")])],"isStart":true});
            var Q46;
            Q46=makeQuery(id+"F2.opExtrude","CAP_EDGE",EDGE,{"disambiguationData":[OSD([sQuery(id+"F1.wireOp",EDGE,"E45.left")])],"isStart":true});
            var Q47;
            Q47=makeQuery(id+"F2.opExtrude","CAP_EDGE",EDGE,{"disambiguationData":[OSD([sQuery(id+"F1.wireOp",EDGE,"E45.right")])],"isStart":true});
            var Q48;
            Q48=makeQuery(id+"F2.opExtrude","CAP_EDGE",EDGE,{"disambiguationData":[OSD([sQuery(id+"F1.wireOp",EDGE,"E169.trimOffspring")])],"isStart":true});
            var Q49;
            Q49=makeQuery(id+"F2.opExtrude","CAP_EDGE",EDGE,{"disambiguationData":[OSD([sQuery(id+"F1.wireOp",EDGE,"E44.left")])],"isStart":true});
            var Q50;
            Q50=makeQuery(id+"F2.opExtrude","CAP_EDGE",EDGE,{"disambiguationData":[OSD([sQuery(id+"F1.wireOp",EDGE,"E224.trimOffspring")])],"isStart":true});
            var Q51;
            Q51=makeQuery(id+"F2.opExtrude","CAP_EDGE",EDGE,{"disambiguationData":[OSD([sQuery(id+"F1.wireOp",EDGE,"E44.right")])],"isStart":true});
            var Q52;
            Q52=makeQuery(id+"F2.opExtrude","CAP_EDGE",EDGE,{"disambiguationData":[OSD([sQuery(id+"F1.wireOp",EDGE,"E167.trimOffspring")])],"isStart":true});
            var Q53;
            Q53=makeQuery(id+"F2.opExtrude","CAP_EDGE",EDGE,{"disambiguationData":[OSD([sQuery(id+"F1.wireOp",EDGE,"E7.top")])],"isStart":true});
            chamfer(context, id + "F7", {"entities" : qUnion([Q0, Q1, Q2, Q3, Q4, Q5, Q6, Q7, Q8, Q9, Q10, Q11, Q12, Q13, Q14, Q15, Q16, Q17, Q18, Q19, Q20, Q21, Q22, Q23, Q24, Q25, Q26, Q27, Q28, Q29, Q30, Q31, Q32, Q33, Q34, Q35, Q36, Q37, Q38, Q39, Q40, Q41, Q42, Q43, Q44, Q45, Q46, Q47, Q48, Q49, Q50, Q51, Q52, Q53]), "width" : .7 * mm, "tangentPropagation" : true});
        }
        {
            var Q0;
            Q0=makeQuery(id+"F2.opExtrude","CAP_EDGE",EDGE,{"disambiguationData":[OSD([sQuery(id+"F1.wireOp",EDGE,"E213.trimOffspring")])],"isStart":true});
            var Q1;
            Q1=makeQuery(id+"F2.opExtrude","CAP_EDGE",EDGE,{"disambiguationData":[OSD([sQuery(id+"F1.wireOp",EDGE,"E57.left")])],"isStart":true});
            var Q2;
            Q2=makeQuery(id+"F2.opExtrude","CAP_EDGE",EDGE,{"disambiguationData":[OSD([sQuery(id+"F1.wireOp",EDGE,"E6.top")])],"isStart":true});
            var Q3;
            Q3=makeQuery(id+"F2.opExtrude","CAP_EDGE",EDGE,{"disambiguationData":[OSD([sQuery(id+"F1.wireOp",EDGE,"E57.right")])],"isStart":true});
            var Q4;
            Q4=makeQuery(id+"F2.opExtrude","CAP_EDGE",EDGE,{"disambiguationData":[OSD([sQuery(id+"F1.wireOp",EDGE,"E200.trimOffspring")])],"isStart":true});
            var Q5;
            Q5=makeQuery(id+"F2.opExtrude","CAP_EDGE",EDGE,{"disambiguationData":[OSD([sQuery(id+"F1.wireOp",EDGE,"E58.left")])],"isStart":true});
            var Q6;
            Q6=makeQuery(id+"F2.opExtrude","CAP_EDGE",EDGE,{"disambiguationData":[OSD([sQuery(id+"F1.wireOp",EDGE,"E58.right")])],"isStart":true});
            var Q7;
            Q7=makeQuery(id+"F2.opExtrude","CAP_EDGE",EDGE,{"disambiguationData":[OSD([sQuery(id+"F1.wireOp",EDGE,"E199.trimOffspring")])],"isStart":true});
            var Q8;
            Q8=makeQuery(id+"F2.opExtrude","CAP_EDGE",EDGE,{"disambiguationData":[OSD([sQuery(id+"F1.wireOp",EDGE,"E59.left")])],"isStart":true});
            var Q9;
            Q9=makeQuery(id+"F2.opExtrude","CAP_EDGE",EDGE,{"disambiguationData":[OSD([sQuery(id+"F1.wireOp",EDGE,"E201.trimOffspring")])],"isStart":true});
            var Q10;
            Q10=makeQuery(id+"F2.opExtrude","CAP_EDGE",EDGE,{"disambiguationData":[OSD([sQuery(id+"F1.wireOp",EDGE,"E59.right")])],"isStart":true});
            var Q11;
            Q11=makeQuery(id+"F2.opExtrude","CAP_EDGE",EDGE,{"disambiguationData":[OSD([sQuery(id+"F1.wireOp",EDGE,"E214.trimOffspring")])],"isStart":true});
            var Q12;
            Q12=makeQuery(id+"F2.opExtrude","CAP_EDGE",EDGE,{"disambiguationData":[OSD([sQuery(id+"F1.wireOp",EDGE,"E208.trimOffspring")])],"isStart":true});
            var Q13;
            Q13=makeQuery(id+"F2.opExtrude","CAP_EDGE",EDGE,{"disambiguationData":[OSD([sQuery(id+"F1.wireOp",EDGE,"E60.left")])],"isStart":true});
            var Q14;
            Q14=makeQuery(id+"F2.opExtrude","CAP_EDGE",EDGE,{"disambiguationData":[OSD([sQuery(id+"F1.wireOp",EDGE,"E202.trimOffspring")])],"isStart":true});
            var Q15;
            Q15=makeQuery(id+"F2.opExtrude","CAP_EDGE",EDGE,{"disambiguationData":[OSD([sQuery(id+"F1.wireOp",EDGE,"E60.right")])],"isStart":true});
            var Q16;
            Q16=makeQuery(id+"F2.opExtrude","CAP_EDGE",EDGE,{"disambiguationData":[OSD([sQuery(id+"F1.wireOp",EDGE,"E198.trimOffspring")])],"isStart":true});
            var Q17;
            Q17=makeQuery(id+"F2.opExtrude","CAP_EDGE",EDGE,{"disambiguationData":[OSD([sQuery(id+"F1.wireOp",EDGE,"E61.left")])],"isStart":true});
            var Q18;
            Q18=makeQuery(id+"F2.opExtrude","CAP_EDGE",EDGE,{"disambiguationData":[OSD([sQuery(id+"F1.wireOp",EDGE,"E203.trimOffspring")])],"isStart":true});
            var Q19;
            Q19=makeQuery(id+"F2.opExtrude","CAP_EDGE",EDGE,{"disambiguationData":[OSD([sQuery(id+"F1.wireOp",EDGE,"E61.right")])],"isStart":true});
            var Q20;
            Q20=makeQuery(id+"F2.opExtrude","CAP_EDGE",EDGE,{"disambiguationData":[OSD([sQuery(id+"F1.wireOp",EDGE,"E180.trimOffspring")])],"isStart":true});
            var Q21;
            Q21=makeQuery(id+"F2.opExtrude","CAP_EDGE",EDGE,{"disambiguationData":[OSD([sQuery(id+"F1.wireOp",EDGE,"E62.left")])],"isStart":true});
            var Q22;
            Q22=makeQuery(id+"F2.opExtrude","CAP_EDGE",EDGE,{"disambiguationData":[OSD([sQuery(id+"F1.wireOp",EDGE,"E62.right")])],"isStart":true});
            var Q23;
            Q23=makeQuery(id+"F2.opExtrude","CAP_EDGE",EDGE,{"disambiguationData":[OSD([sQuery(id+"F1.wireOp",EDGE,"E185.trimOffspring")])],"isStart":true});
            var Q24;
            Q24=makeQuery(id+"F2.opExtrude","CAP_EDGE",EDGE,{"disambiguationData":[OSD([sQuery(id+"F1.wireOp",EDGE,"E215.trimOffspring")])],"isStart":true});
            var Q25;
            Q25=makeQuery(id+"F2.opExtrude","CAP_EDGE",EDGE,{"disambiguationData":[OSD([sQuery(id+"F1.wireOp",EDGE,"E204.trimOffspring")])],"isStart":true});
            var Q26;
            Q26=makeQuery(id+"F2.opExtrude","CAP_EDGE",EDGE,{"disambiguationData":[OSD([sQuery(id+"F1.wireOp",EDGE,"E63.left")])],"isStart":true});
            var Q27;
            Q27=makeQuery(id+"F2.opExtrude","CAP_EDGE",EDGE,{"disambiguationData":[OSD([sQuery(id+"F1.wireOp",EDGE,"E63.right")])],"isStart":true});
            var Q28;
            Q28=makeQuery(id+"F2.opExtrude","CAP_EDGE",EDGE,{"disambiguationData":[OSD([sQuery(id+"F1.wireOp",EDGE,"E186.trimOffspring")])],"isStart":true});
            var Q29;
            Q29=makeQuery(id+"F2.opExtrude","CAP_EDGE",EDGE,{"disambiguationData":[OSD([sQuery(id+"F1.wireOp",EDGE,"E64.left")])],"isStart":true});
            var Q30;
            Q30=makeQuery(id+"F2.opExtrude","CAP_EDGE",EDGE,{"disambiguationData":[OSD([sQuery(id+"F1.wireOp",EDGE,"E216.trimOffspring")])],"isStart":true});
            var Q31;
            Q31=makeQuery(id+"F2.opExtrude","CAP_EDGE",EDGE,{"disambiguationData":[OSD([sQuery(id+"F1.wireOp",EDGE,"E64.right")])],"isStart":true});
            var Q32;
            Q32=makeQuery(id+"F2.opExtrude","CAP_EDGE",EDGE,{"disambiguationData":[OSD([sQuery(id+"F1.wireOp",EDGE,"E192.trimOffspring")])],"isStart":true});
            var Q33;
            Q33=makeQuery(id+"F2.opExtrude","CAP_EDGE",EDGE,{"disambiguationData":[OSD([sQuery(id+"F1.wireOp",EDGE,"E65.left")])],"isStart":true});
            var Q34;
            Q34=makeQuery(id+"F2.opExtrude","CAP_EDGE",EDGE,{"disambiguationData":[OSD([sQuery(id+"F1.wireOp",EDGE,"E217.trimOffspring")])],"isStart":true});
            var Q35;
            Q35=makeQuery(id+"F2.opExtrude","CAP_EDGE",EDGE,{"disambiguationData":[OSD([sQuery(id+"F1.wireOp",EDGE,"E65.right")])],"isStart":true});
            var Q36;
            Q36=makeQuery(id+"F2.opExtrude","CAP_EDGE",EDGE,{"disambiguationData":[OSD([sQuery(id+"F1.wireOp",EDGE,"E220.trimOffspring")])],"isStart":true});
            var Q37;
            Q37=makeQuery(id+"F2.opExtrude","CAP_EDGE",EDGE,{"disambiguationData":[OSD([sQuery(id+"F1.wireOp",EDGE,"E66.left")])],"isStart":true});
            var Q38;
            Q38=makeQuery(id+"F2.opExtrude","CAP_EDGE",EDGE,{"disambiguationData":[OSD([sQuery(id+"F1.wireOp",EDGE,"E218.trimOffspring")])],"isStart":true});
            var Q39;
            Q39=makeQuery(id+"F2.opExtrude","CAP_EDGE",EDGE,{"disambiguationData":[OSD([sQuery(id+"F1.wireOp",EDGE,"E66.right")])],"isStart":true});
            var Q40;
            Q40=makeQuery(id+"F2.opExtrude","CAP_EDGE",EDGE,{"disambiguationData":[OSD([sQuery(id+"F1.wireOp",EDGE,"E228.trimOffspring")])],"isStart":true});
            var Q41;
            Q41=makeQuery(id+"F2.opExtrude","CAP_EDGE",EDGE,{"disambiguationData":[OSD([sQuery(id+"F1.wireOp",EDGE,"E67.left")])],"isStart":true});
            var Q42;
            Q42=makeQuery(id+"F2.opExtrude","CAP_EDGE",EDGE,{"disambiguationData":[OSD([sQuery(id+"F1.wireOp",EDGE,"E219.trimOffspring")])],"isStart":true});
            var Q43;
            Q43=makeQuery(id+"F2.opExtrude","CAP_EDGE",EDGE,{"disambiguationData":[OSD([sQuery(id+"F1.wireOp",EDGE,"E67.right")])],"isStart":true});
            var Q44;
            Q44=makeQuery(id+"F2.opExtrude","CAP_EDGE",EDGE,{"disambiguationData":[OSD([sQuery(id+"F1.wireOp",EDGE,"E232.trimOffspring")])],"isStart":true});
            var Q45;
            Q45=makeQuery(id+"F2.opExtrude","CAP_EDGE",EDGE,{"disambiguationData":[OSD([sQuery(id+"F1.wireOp",EDGE,"E68.left")])],"isStart":true});
            var Q46;
            Q46=makeQuery(id+"F2.opExtrude","CAP_EDGE",EDGE,{"disambiguationData":[OSD([sQuery(id+"F1.wireOp",EDGE,"E227.trimOffspring")])],"isStart":true});
            chamfer(context, id + "F8", {"entities" : qUnion([Q0, Q1, Q2, Q3, Q4, Q5, Q6, Q7, Q8, Q9, Q10, Q11, Q12, Q13, Q14, Q15, Q16, Q17, Q18, Q19, Q20, Q21, Q22, Q23, Q24, Q25, Q26, Q27, Q28, Q29, Q30, Q31, Q32, Q33, Q34, Q35, Q36, Q37, Q38, Q39, Q40, Q41, Q42, Q43, Q44, Q45, Q46]), "width" : .7 * mm, "tangentPropagation" : true});
        }
        {
            var Q0;
            Q0=makeQuery(id+"F2.opExtrude","CAP_EDGE",EDGE,{"disambiguationData":[OSD([sQuery(id+"F1.wireOp",EDGE,"E68.right")])],"isStart":true});
            var Q1;
            Q1=makeQuery(id+"F2.opExtrude","CAP_EDGE",EDGE,{"disambiguationData":[OSD([sQuery(id+"F1.wireOp",EDGE,"E223.trimOffspring")])],"isStart":true});
            var Q2;
            Q2=makeQuery(id+"F2.opExtrude","CAP_EDGE",EDGE,{"disambiguationData":[OSD([sQuery(id+"F1.wireOp",EDGE,"E69.left")])],"isStart":true});
            var Q3;
            Q3=makeQuery(id+"F2.opExtrude","CAP_EDGE",EDGE,{"disambiguationData":[OSD([sQuery(id+"F1.wireOp",EDGE,"E226.trimOffspring")])],"isStart":true});
            var Q4;
            Q4=makeQuery(id+"F2.opExtrude","CAP_EDGE",EDGE,{"disambiguationData":[OSD([sQuery(id+"F1.wireOp",EDGE,"E69.right")])],"isStart":true});
            var Q5;
            Q5=makeQuery(id+"F2.opExtrude","CAP_EDGE",EDGE,{"disambiguationData":[OSD([sQuery(id+"F1.wireOp",EDGE,"E7.bottom")])],"isStart":true});
            var Q6;
            Q6=makeQuery(id+"F2.opExtrude","CAP_EDGE",EDGE,{"disambiguationData":[OSD([sQuery(id+"F1.wireOp",EDGE,"E225.trimOffspring")])],"isStart":true});
            var Q7;
            Q7=makeQuery(id+"F2.opExtrude","CAP_EDGE",EDGE,{"disambiguationData":[OSD([sQuery(id+"F1.wireOp",EDGE,"E112.trimOffspring")])],"isStart":true});
            var Q8;
            Q8=makeQuery(id+"F2.opExtrude","CAP_EDGE",EDGE,{"disambiguationData":[OSD([sQuery(id+"F1.wireOp",EDGE,"E88.right")])],"isStart":true});
            var Q9;
            Q9=makeQuery(id+"F2.opExtrude","CAP_EDGE",EDGE,{"disambiguationData":[OSD([sQuery(id+"F1.wireOp",EDGE,"E88.left")])],"isStart":true});
            var Q10;
            Q10=makeQuery(id+"F2.opExtrude","CAP_EDGE",EDGE,{"disambiguationData":[OSD([sQuery(id+"F1.wireOp",EDGE,"E110.trimOffspring")])],"isStart":true});
            var Q11;
            Q11=makeQuery(id+"F2.opExtrude","CAP_EDGE",EDGE,{"disambiguationData":[OSD([sQuery(id+"F1.wireOp",EDGE,"E70.right")])],"isStart":true});
            var Q12;
            Q12=makeQuery(id+"F2.opExtrude","CAP_EDGE",EDGE,{"disambiguationData":[OSD([sQuery(id+"F1.wireOp",EDGE,"E70.left")])],"isStart":true});
            var Q13;
            Q13=makeQuery(id+"F2.opExtrude","CAP_EDGE",EDGE,{"disambiguationData":[OSD([sQuery(id+"F1.wireOp",EDGE,"E108.trimOffspring")])],"isStart":true});
            var Q14;
            Q14=makeQuery(id+"F2.opExtrude","CAP_EDGE",EDGE,{"disambiguationData":[OSD([sQuery(id+"F1.wireOp",EDGE,"E71.right")])],"isStart":true});
            var Q15;
            Q15=makeQuery(id+"F2.opExtrude","CAP_EDGE",EDGE,{"disambiguationData":[OSD([sQuery(id+"F1.wireOp",EDGE,"E71.left")])],"isStart":true});
            var Q16;
            Q16=makeQuery(id+"F2.opExtrude","CAP_EDGE",EDGE,{"disambiguationData":[OSD([sQuery(id+"F1.wireOp",EDGE,"E106.trimOffspring")])],"isStart":true});
            var Q17;
            Q17=makeQuery(id+"F2.opExtrude","CAP_EDGE",EDGE,{"disambiguationData":[OSD([sQuery(id+"F1.wireOp",EDGE,"E72.right")])],"isStart":true});
            var Q18;
            Q18=makeQuery(id+"F2.opExtrude","CAP_EDGE",EDGE,{"disambiguationData":[OSD([sQuery(id+"F1.wireOp",EDGE,"E72.left")])],"isStart":true});
            var Q19;
            Q19=makeQuery(id+"F2.opExtrude","CAP_EDGE",EDGE,{"disambiguationData":[OSD([sQuery(id+"F1.wireOp",EDGE,"E104.trimOffspring")])],"isStart":true});
            var Q20;
            Q20=makeQuery(id+"F2.opExtrude","CAP_EDGE",EDGE,{"disambiguationData":[OSD([sQuery(id+"F1.wireOp",EDGE,"E73.right")])],"isStart":true});
            var Q21;
            Q21=makeQuery(id+"F2.opExtrude","CAP_EDGE",EDGE,{"disambiguationData":[OSD([sQuery(id+"F1.wireOp",EDGE,"E73.left")])],"isStart":true});
            var Q22;
            Q22=makeQuery(id+"F2.opExtrude","CAP_EDGE",EDGE,{"disambiguationData":[OSD([sQuery(id+"F1.wireOp",EDGE,"E101.trimOffspring")])],"isStart":true});
            var Q23;
            Q23=makeQuery(id+"F2.opExtrude","CAP_EDGE",EDGE,{"disambiguationData":[OSD([sQuery(id+"F1.wireOp",EDGE,"E74.right")])],"isStart":true});
            var Q24;
            Q24=makeQuery(id+"F2.opExtrude","CAP_EDGE",EDGE,{"disambiguationData":[OSD([sQuery(id+"F1.wireOp",EDGE,"E74.left")])],"isStart":true});
            var Q25;
            Q25=makeQuery(id+"F2.opExtrude","CAP_EDGE",EDGE,{"disambiguationData":[OSD([sQuery(id+"F1.wireOp",EDGE,"E100.trimOffspring")])],"isStart":true});
            var Q26;
            Q26=makeQuery(id+"F2.opExtrude","CAP_EDGE",EDGE,{"disambiguationData":[OSD([sQuery(id+"F1.wireOp",EDGE,"E75.right")])],"isStart":true});
            var Q27;
            Q27=makeQuery(id+"F2.opExtrude","CAP_EDGE",EDGE,{"disambiguationData":[OSD([sQuery(id+"F1.wireOp",EDGE,"E75.left")])],"isStart":true});
            var Q28;
            Q28=makeQuery(id+"F2.opExtrude","CAP_EDGE",EDGE,{"disambiguationData":[OSD([sQuery(id+"F1.wireOp",EDGE,"E94.trimOffspring")])],"isStart":true});
            var Q29;
            Q29=makeQuery(id+"F2.opExtrude","CAP_EDGE",EDGE,{"disambiguationData":[OSD([sQuery(id+"F1.wireOp",EDGE,"E76.right")])],"isStart":true});
            chamfer(context, id + "F9", {"entities" : qUnion([Q0, Q1, Q2, Q3, Q4, Q5, Q6, Q7, Q8, Q9, Q10, Q11, Q12, Q13, Q14, Q15, Q16, Q17, Q18, Q19, Q20, Q21, Q22, Q23, Q24, Q25, Q26, Q27, Q28, Q29]), "width" : .7 * mm, "tangentPropagation" : true});
        }
        {
            var Q0;
            Q0=makeQuery(id+"F2.opExtrude","CAP_EDGE",EDGE,{"disambiguationData":[OSD([sQuery(id+"F1.wireOp",EDGE,"E76.left")])],"isStart":true});
            var Q1;
            Q1=makeQuery(id+"F2.opExtrude","CAP_EDGE",EDGE,{"disambiguationData":[OSD([sQuery(id+"F1.wireOp",EDGE,"E93.trimOffspring")])],"isStart":true});
            var Q2;
            Q2=makeQuery(id+"F2.opExtrude","CAP_EDGE",EDGE,{"disambiguationData":[OSD([sQuery(id+"F1.wireOp",EDGE,"E77.right")])],"isStart":true});
            var Q3;
            Q3=makeQuery(id+"F2.opExtrude","CAP_EDGE",EDGE,{"disambiguationData":[OSD([sQuery(id+"F1.wireOp",EDGE,"E77.left")])],"isStart":true});
            var Q4;
            Q4=makeQuery(id+"F2.opExtrude","CAP_EDGE",EDGE,{"disambiguationData":[OSD([sQuery(id+"F1.wireOp",EDGE,"E92.trimOffspring")])],"isStart":true});
            var Q5;
            Q5=makeQuery(id+"F2.opExtrude","CAP_EDGE",EDGE,{"disambiguationData":[OSD([sQuery(id+"F1.wireOp",EDGE,"E78.right")])],"isStart":true});
            var Q6;
            Q6=makeQuery(id+"F2.opExtrude","CAP_EDGE",EDGE,{"disambiguationData":[OSD([sQuery(id+"F1.wireOp",EDGE,"E78.left")])],"isStart":true});
            var Q7;
            Q7=makeQuery(id+"F2.opExtrude","CAP_EDGE",EDGE,{"disambiguationData":[OSD([sQuery(id+"F1.wireOp",EDGE,"E91.trimOffspring")])],"isStart":true});
            var Q8;
            Q8=makeQuery(id+"F2.opExtrude","CAP_EDGE",EDGE,{"disambiguationData":[OSD([sQuery(id+"F1.wireOp",EDGE,"E79.right")])],"isStart":true});
            var Q9;
            Q9=makeQuery(id+"F2.opExtrude","CAP_EDGE",EDGE,{"disambiguationData":[OSD([sQuery(id+"F1.wireOp",EDGE,"E79.left")])],"isStart":true});
            var Q10;
            Q10=makeQuery(id+"F2.opExtrude","CAP_EDGE",EDGE,{"disambiguationData":[OSD([sQuery(id+"F1.wireOp",EDGE,"E6.bottom")])],"isStart":true});
            chamfer(context, id + "F10", {"entities" : qUnion([Q0, Q1, Q2, Q3, Q4, Q5, Q6, Q7, Q8, Q9, Q10]), "width" : .7 * mm, "tangentPropagation" : true});
        }
        {
            var Q0;
            Q0=qCreatedBy(makeId("Top.planeOp"),FACE);
            var sketch = newSketch(context, id + "F11", { "sketchPlane" : qUnion([Q0])});
            skArc(sketch, "E233.0.0", {"start": v(-1288.18, -367.7) * mm, "mid": v(-1286.72, -371.23) * mm, "end": v(-1283.18, -372.7) * mm});
            skLineSegment(sketch, "E233.0.1", {"start": v(-1283.18, -372.7) * mm, "end": v(-1003.62, -372.7) * mm});
            skArc(sketch, "E233.0.2", {"start": v(-1003.62, -372.7) * mm, "mid": v(-1000.09, -371.23) * mm, "end": v(-998.62, -367.7) * mm});
            skLineSegment(sketch, "E233.0.3", {"start": v(-998.62, -367.7) * mm, "end": v(-998.62, -262.82) * mm});
            skArc(sketch, "E233.0.4", {"start": v(-998.62, -262.82) * mm, "mid": v(-1000.09, -259.29) * mm, "end": v(-1003.62, -257.82) * mm});
            skLineSegment(sketch, "E233.0.5", {"start": v(-1003.62, -257.82) * mm, "end": v(-1283.18, -257.82) * mm});
            skArc(sketch, "E233.0.6", {"start": v(-1283.18, -257.82) * mm, "mid": v(-1286.72, -259.29) * mm, "end": v(-1288.18, -262.82) * mm});
            skLineSegment(sketch, "E233.0.7", {"start": v(-1288.18, -262.82) * mm, "end": v(-1288.18, -367.7) * mm});
            skLineSegment(sketch, "E234", {"start": v(-1285.22, -258.25) * mm, "end": v(-1285.22, -372.26) * mm});
            skLineSegment(sketch, "E235", {"start": v(-1001.67, -258.22) * mm, "end": v(-1001.67, -372.3) * mm});
            skSolve(sketch);
        }
        {
            var Q0;
            {var subQ0=sQuery(id+"F11.wireOp",EDGE,"E233.0.7");Q0=makeQuery(id+"F11.imprint","IMPRINT",FACE,{"disambiguationData":[TD([[makeQuery(id+"F11.imprint","IMPRINT",EDGE,{"derivedFrom":subQ0}),1.0]])]});}
            var Q1;
            {var subQ0=sQuery(id+"F11.wireOp",EDGE,"E233.0.3");Q1=makeQuery(id+"F11.imprint","IMPRINT",FACE,{"disambiguationData":[TD([[makeQuery(id+"F11.imprint","IMPRINT",EDGE,{"derivedFrom":subQ0}),1.0]])]});}
            extrude(context, id + "F12", {"entities" : qUnion([Q0, Q1]), "depth" : 5 * mm});
        }
        {
            var Q0;
            Q0=makeQuery(id+"F12.opExtrude","SWEPT_BODY",BODY,{"disambiguationData":[OSD([sQuery(id+"F11.wireOp",EDGE,"E233.0.0"),sQuery(id+"F11.wireOp",EDGE,"E233.0.6"),sQuery(id+"F11.wireOp",EDGE,"E233.0.7"),sQuery(id+"F11.wireOp",EDGE,"E234")])]});
            var Q1;
            Q1=makeQuery(id+"F12.opExtrude","SWEPT_BODY",BODY,{"disambiguationData":[OSD([sQuery(id+"F11.wireOp",EDGE,"E233.0.2"),sQuery(id+"F11.wireOp",EDGE,"E233.0.3"),sQuery(id+"F11.wireOp",EDGE,"E233.0.4"),sQuery(id+"F11.wireOp",EDGE,"E235")])]});
            deleteBodies(context, id + "F13", {"entities" : qUnion([Q0, Q1])});
        }
        {
            var Q0;
            Q0=makeQuery(id+"F2.opExtrude","CAP_FACE",FACE,{"disambiguationData":[OSD([sQuery(id+"F1.wireOp",EDGE,"E1.0"),sQuery(id+"F1.wireOp",EDGE,"E2"),sQuery(id+"F1.wireOp",EDGE,"E3"),sQuery(id+"F1.wireOp",EDGE,"E4"),sQuery(id+"F1.wireOp",EDGE,"E5.left"),sQuery(id+"F1.wireOp",EDGE,"E5.right"),sQuery(id+"F1.wireOp",EDGE,"E6.bottom"),sQuery(id+"F1.wireOp",EDGE,"E6.top"),sQuery(id+"F1.wireOp",EDGE,"E7.bottom"),sQuery(id+"F1.wireOp",EDGE,"E7.top"),sQuery(id+"F1.wireOp",EDGE,"E8.bottom"),sQuery(id+"F1.wireOp",EDGE,"E8.top"),sQuery(id+"F1.wireOp",EDGE,"E9.bottom"),sQuery(id+"F1.wireOp",EDGE,"E9.top"),sQuery(id+"F1.wireOp",EDGE,"E10.bottom"),sQuery(id+"F1.wireOp",EDGE,"E10.top"),sQuery(id+"F1.wireOp",EDGE,"E11.left"),sQuery(id+"F1.wireOp",EDGE,"E11.right"),sQuery(id+"F1.wireOp",EDGE,"E12.left"),sQuery(id+"F1.wireOp",EDGE,"E12.right"),sQuery(id+"F1.wireOp",EDGE,"E13.left"),sQuery(id+"F1.wireOp",EDGE,"E13.right"),sQuery(id+"F1.wireOp",EDGE,"E14.left"),sQuery(id+"F1.wireOp",EDGE,"E14.right"),sQuery(id+"F1.wireOp",EDGE,"E15.top"),sQuery(id+"F1.wireOp",EDGE,"E16.top"),sQuery(id+"F1.wireOp",EDGE,"E17.top"),sQuery(id+"F1.wireOp",EDGE,"E18.left"),sQuery(id+"F1.wireOp",EDGE,"E18.right"),sQuery(id+"F1.wireOp",EDGE,"E19.left"),sQuery(id+"F1.wireOp",EDGE,"E19.right"),sQuery(id+"F1.wireOp",EDGE,"E20.left"),sQuery(id+"F1.wireOp",EDGE,"E20.right"),sQuery(id+"F1.wireOp",EDGE,"E21.left"),sQuery(id+"F1.wireOp",EDGE,"E21.right"),sQuery(id+"F1.wireOp",EDGE,"E22.left"),sQuery(id+"F1.wireOp",EDGE,"E22.right"),sQuery(id+"F1.wireOp",EDGE,"E23.left"),sQuery(id+"F1.wireOp",EDGE,"E23.right"),sQuery(id+"F1.wireOp",EDGE,"E24.left"),sQuery(id+"F1.wireOp",EDGE,"E24.right"),sQuery(id+"F1.wireOp",EDGE,"E25.left"),sQuery(id+"F1.wireOp",EDGE,"E25.right"),sQuery(id+"F1.wireOp",EDGE,"E26.left"),sQuery(id+"F1.wireOp",EDGE,"E26.right"),sQuery(id+"F1.wireOp",EDGE,"E27.left"),sQuery(id+"F1.wireOp",EDGE,"E27.right"),sQuery(id+"F1.wireOp",EDGE,"E28.left"),sQuery(id+"F1.wireOp",EDGE,"E28.right"),sQuery(id+"F1.wireOp",EDGE,"E29.left"),sQuery(id+"F1.wireOp",EDGE,"E29.right"),sQuery(id+"F1.wireOp",EDGE,"E30.left"),sQuery(id+"F1.wireOp",EDGE,"E30.right"),sQuery(id+"F1.wireOp",EDGE,"E31.left"),sQuery(id+"F1.wireOp",EDGE,"E31.right"),sQuery(id+"F1.wireOp",EDGE,"E32.left"),sQuery(id+"F1.wireOp",EDGE,"E32.right"),sQuery(id+"F1.wireOp",EDGE,"E33.left"),sQuery(id+"F1.wireOp",EDGE,"E33.right"),sQuery(id+"F1.wireOp",EDGE,"E34.left"),sQuery(id+"F1.wireOp",EDGE,"E34.right"),sQuery(id+"F1.wireOp",EDGE,"E35.left"),sQuery(id+"F1.wireOp",EDGE,"E35.right"),sQuery(id+"F1.wireOp",EDGE,"E36.left"),sQuery(id+"F1.wireOp",EDGE,"E36.right"),sQuery(id+"F1.wireOp",EDGE,"E37.left"),sQuery(id+"F1.wireOp",EDGE,"E37.right"),sQuery(id+"F1.wireOp",EDGE,"E38.left"),sQuery(id+"F1.wireOp",EDGE,"E38.right"),sQuery(id+"F1.wireOp",EDGE,"E39.left"),sQuery(id+"F1.wireOp",EDGE,"E39.right"),sQuery(id+"F1.wireOp",EDGE,"E40.left"),sQuery(id+"F1.wireOp",EDGE,"E40.right"),sQuery(id+"F1.wireOp",EDGE,"E41.left"),sQuery(id+"F1.wireOp",EDGE,"E41.right"),sQuery(id+"F1.wireOp",EDGE,"E42.left"),sQuery(id+"F1.wireOp",EDGE,"E42.right"),sQuery(id+"F1.wireOp",EDGE,"E43.left"),sQuery(id+"F1.wireOp",EDGE,"E43.right"),sQuery(id+"F1.wireOp",EDGE,"E44.left"),sQuery(id+"F1.wireOp",EDGE,"E44.right"),sQuery(id+"F1.wireOp",EDGE,"E45.left"),sQuery(id+"F1.wireOp",EDGE,"E45.right"),sQuery(id+"F1.wireOp",EDGE,"E46.left"),sQuery(id+"F1.wireOp",EDGE,"E46.right"),sQuery(id+"F1.wireOp",EDGE,"E47.left"),sQuery(id+"F1.wireOp",EDGE,"E47.right"),sQuery(id+"F1.wireOp",EDGE,"E48.left"),sQuery(id+"F1.wireOp",EDGE,"E48.right"),sQuery(id+"F1.wireOp",EDGE,"E49.left"),sQuery(id+"F1.wireOp",EDGE,"E49.right"),sQuery(id+"F1.wireOp",EDGE,"E50.right"),sQuery(id+"F1.wireOp",EDGE,"E51.left"),sQuery(id+"F1.wireOp",EDGE,"E51.right"),sQuery(id+"F1.wireOp",EDGE,"E52.left"),sQuery(id+"F1.wireOp",EDGE,"E52.right"),sQuery(id+"F1.wireOp",EDGE,"E53.left"),sQuery(id+"F1.wireOp",EDGE,"E53.right"),sQuery(id+"F1.wireOp",EDGE,"E54.left"),sQuery(id+"F1.wireOp",EDGE,"E54.right"),sQuery(id+"F1.wireOp",EDGE,"E55.left"),sQuery(id+"F1.wireOp",EDGE,"E55.right"),sQuery(id+"F1.wireOp",EDGE,"E56.left"),sQuery(id+"F1.wireOp",EDGE,"E56.right"),sQuery(id+"F1.wireOp",EDGE,"E57.left"),sQuery(id+"F1.wireOp",EDGE,"E57.right"),sQuery(id+"F1.wireOp",EDGE,"E58.left"),sQuery(id+"F1.wireOp",EDGE,"E58.right"),sQuery(id+"F1.wireOp",EDGE,"E59.left"),sQuery(id+"F1.wireOp",EDGE,"E59.right"),sQuery(id+"F1.wireOp",EDGE,"E60.left"),sQuery(id+"F1.wireOp",EDGE,"E60.right"),sQuery(id+"F1.wireOp",EDGE,"E61.left"),sQuery(id+"F1.wireOp",EDGE,"E61.right"),sQuery(id+"F1.wireOp",EDGE,"E62.left"),sQuery(id+"F1.wireOp",EDGE,"E62.right"),sQuery(id+"F1.wireOp",EDGE,"E63.left"),sQuery(id+"F1.wireOp",EDGE,"E63.right"),sQuery(id+"F1.wireOp",EDGE,"E64.left"),sQuery(id+"F1.wireOp",EDGE,"E64.right"),sQuery(id+"F1.wireOp",EDGE,"E65.left"),sQuery(id+"F1.wireOp",EDGE,"E65.right"),sQuery(id+"F1.wireOp",EDGE,"E66.left"),sQuery(id+"F1.wireOp",EDGE,"E66.right"),sQuery(id+"F1.wireOp",EDGE,"E67.left"),sQuery(id+"F1.wireOp",EDGE,"E67.right"),sQuery(id+"F1.wireOp",EDGE,"E68.left"),sQuery(id+"F1.wireOp",EDGE,"E68.right"),sQuery(id+"F1.wireOp",EDGE,"E69.left"),sQuery(id+"F1.wireOp",EDGE,"E69.right"),sQuery(id+"F1.wireOp",EDGE,"E70.left"),sQuery(id+"F1.wireOp",EDGE,"E70.right"),sQuery(id+"F1.wireOp",EDGE,"E71.left"),sQuery(id+"F1.wireOp",EDGE,"E71.right"),sQuery(id+"F1.wireOp",EDGE,"E72.left"),sQuery(id+"F1.wireOp",EDGE,"E72.right"),sQuery(id+"F1.wireOp",EDGE,"E73.left"),sQuery(id+"F1.wireOp",EDGE,"E73.right"),sQuery(id+"F1.wireOp",EDGE,"E74.left"),sQuery(id+"F1.wireOp",EDGE,"E74.right"),sQuery(id+"F1.wireOp",EDGE,"E75.left"),sQuery(id+"F1.wireOp",EDGE,"E75.right"),sQuery(id+"F1.wireOp",EDGE,"E76.left"),sQuery(id+"F1.wireOp",EDGE,"E76.right"),sQuery(id+"F1.wireOp",EDGE,"E77.left"),sQuery(id+"F1.wireOp",EDGE,"E77.right"),sQuery(id+"F1.wireOp",EDGE,"E78.left"),sQuery(id+"F1.wireOp",EDGE,"E78.right"),sQuery(id+"F1.wireOp",EDGE,"E79.left"),sQuery(id+"F1.wireOp",EDGE,"E79.right"),sQuery(id+"F1.wireOp",EDGE,"E80.filletArc"),sQuery(id+"F1.wireOp",EDGE,"E81.filletArc"),sQuery(id+"F1.wireOp",EDGE,"E82.filletArc"),sQuery(id+"F1.wireOp",EDGE,"E83.filletArc"),sQuery(id+"F1.wireOp",EDGE,"E84.filletArc"),sQuery(id+"F1.wireOp",EDGE,"E85.filletArc"),sQuery(id+"F1.wireOp",EDGE,"E86.filletArc"),sQuery(id+"F1.wireOp",EDGE,"E87.filletArc"),sQuery(id+"F1.wireOp",EDGE,"E88.left"),sQuery(id+"F1.wireOp",EDGE,"E88.right"),sQuery(id+"F1.wireOp",EDGE,"E89"),sQuery(id+"F1.wireOp",EDGE,"E90"),sQuery(id+"F1.wireOp",EDGE,"E91.trimOffspring"),sQuery(id+"F1.wireOp",EDGE,"E92.trimOffspring"),sQuery(id+"F1.wireOp",EDGE,"E93.trimOffspring"),sQuery(id+"F1.wireOp",EDGE,"E94.trimOffspring"),sQuery(id+"F1.wireOp",EDGE,"E95.trimOffspring"),sQuery(id+"F1.wireOp",EDGE,"E96.trimOffspring"),sQuery(id+"F1.wireOp",EDGE,"E97.trimOffspring"),sQuery(id+"F1.wireOp",EDGE,"E98.trimOffspring"),sQuery(id+"F1.wireOp",EDGE,"E99.trimOffspring"),sQuery(id+"F1.wireOp",EDGE,"E100.trimOffspring"),sQuery(id+"F1.wireOp",EDGE,"E101.trimOffspring"),sQuery(id+"F1.wireOp",EDGE,"E102.trimOffspring"),sQuery(id+"F1.wireOp",EDGE,"E103.trimOffspring"),sQuery(id+"F1.wireOp",EDGE,"E104.trimOffspring"),sQuery(id+"F1.wireOp",EDGE,"E105.trimOffspring"),sQuery(id+"F1.wireOp",EDGE,"E106.trimOffspring"),sQuery(id+"F1.wireOp",EDGE,"E107.trimOffspring"),sQuery(id+"F1.wireOp",EDGE,"E108.trimOffspring"),sQuery(id+"F1.wireOp",EDGE,"E109.trimOffspring"),sQuery(id+"F1.wireOp",EDGE,"E110.trimOffspring"),sQuery(id+"F1.wireOp",EDGE,"E111.trimOffspring"),sQuery(id+"F1.wireOp",EDGE,"E112.trimOffspring"),sQuery(id+"F1.wireOp",EDGE,"E113.trimOffspring"),sQuery(id+"F1.wireOp",EDGE,"E114.trimOffspring"),sQuery(id+"F1.wireOp",EDGE,"E115.trimOffspring"),sQuery(id+"F1.wireOp",EDGE,"E116.trimOffspring"),sQuery(id+"F1.wireOp",EDGE,"E117.trimOffspring"),sQuery(id+"F1.wireOp",EDGE,"E118.trimOffspring"),sQuery(id+"F1.wireOp",EDGE,"E119.trimOffspring"),sQuery(id+"F1.wireOp",EDGE,"E120.trimOffspring"),sQuery(id+"F1.wireOp",EDGE,"E121.trimOffspring"),sQuery(id+"F1.wireOp",EDGE,"E122.trimOffspring"),sQuery(id+"F1.wireOp",EDGE,"E123.trimOffspring"),sQuery(id+"F1.wireOp",EDGE,"E124.trimOffspring"),sQuery(id+"F1.wireOp",EDGE,"E125.trimOffspring"),sQuery(id+"F1.wireOp",EDGE,"E126.trimOffspring"),sQuery(id+"F1.wireOp",EDGE,"E127.trimOffspring"),sQuery(id+"F1.wireOp",EDGE,"E128.trimOffspring"),sQuery(id+"F1.wireOp",EDGE,"E129.trimOffspring"),sQuery(id+"F1.wireOp",EDGE,"E130.trimOffspring"),sQuery(id+"F1.wireOp",EDGE,"E131.trimOffspring"),sQuery(id+"F1.wireOp",EDGE,"E132.trimOffspring"),sQuery(id+"F1.wireOp",EDGE,"E133.trimOffspring"),sQuery(id+"F1.wireOp",EDGE,"E134.trimOffspring"),sQuery(id+"F1.wireOp",EDGE,"E135.trimOffspring"),sQuery(id+"F1.wireOp",EDGE,"E136.trimOffspring"),sQuery(id+"F1.wireOp",EDGE,"E137.trimOffspring"),sQuery(id+"F1.wireOp",EDGE,"E138.trimOffspring"),sQuery(id+"F1.wireOp",EDGE,"E139.trimOffspring"),sQuery(id+"F1.wireOp",EDGE,"E140.trimOffspring"),sQuery(id+"F1.wireOp",EDGE,"E141.trimOffspring"),sQuery(id+"F1.wireOp",EDGE,"E142.trimOffspring"),sQuery(id+"F1.wireOp",EDGE,"E143.trimOffspring"),sQuery(id+"F1.wireOp",EDGE,"E144.trimOffspring"),sQuery(id+"F1.wireOp",EDGE,"E145.trimOffspring"),sQuery(id+"F1.wireOp",EDGE,"E146.trimOffspring"),sQuery(id+"F1.wireOp",EDGE,"E147.trimOffspring"),sQuery(id+"F1.wireOp",EDGE,"E148.trimOffspring"),sQuery(id+"F1.wireOp",EDGE,"E149.trimOffspring"),sQuery(id+"F1.wireOp",EDGE,"E150.trimOffspring"),sQuery(id+"F1.wireOp",EDGE,"E151.trimOffspring"),sQuery(id+"F1.wireOp",EDGE,"E152.trimOffspring"),sQuery(id+"F1.wireOp",EDGE,"E153.trimOffspring"),sQuery(id+"F1.wireOp",EDGE,"E154.trimOffspring"),sQuery(id+"F1.wireOp",EDGE,"E155.trimOffspring"),sQuery(id+"F1.wireOp",EDGE,"E156.trimOffspring"),sQuery(id+"F1.wireOp",EDGE,"E157.trimOffspring"),sQuery(id+"F1.wireOp",EDGE,"E158.trimOffspring"),sQuery(id+"F1.wireOp",EDGE,"E159.trimOffspring"),sQuery(id+"F1.wireOp",EDGE,"E160.trimOffspring"),sQuery(id+"F1.wireOp",EDGE,"E161.trimOffspring"),sQuery(id+"F1.wireOp",EDGE,"E162.trimOffspring"),sQuery(id+"F1.wireOp",EDGE,"E163.trimOffspring"),sQuery(id+"F1.wireOp",EDGE,"E164.trimOffspring"),sQuery(id+"F1.wireOp",EDGE,"E165.trimOffspring"),sQuery(id+"F1.wireOp",EDGE,"E166.trimOffspring"),sQuery(id+"F1.wireOp",EDGE,"E167.trimOffspring"),sQuery(id+"F1.wireOp",EDGE,"E168.trimOffspring"),sQuery(id+"F1.wireOp",EDGE,"E169.trimOffspring"),sQuery(id+"F1.wireOp",EDGE,"E170.trimOffspring"),sQuery(id+"F1.wireOp",EDGE,"E171.trimOffspring"),sQuery(id+"F1.wireOp",EDGE,"E172.trimOffspring"),sQuery(id+"F1.wireOp",EDGE,"E173.trimOffspring"),sQuery(id+"F1.wireOp",EDGE,"E174.trimOffspring"),sQuery(id+"F1.wireOp",EDGE,"E175.trimOffspring"),sQuery(id+"F1.wireOp",EDGE,"E176.trimOffspring"),sQuery(id+"F1.wireOp",EDGE,"E177.trimOffspring"),sQuery(id+"F1.wireOp",EDGE,"E178.trimOffspring"),sQuery(id+"F1.wireOp",EDGE,"E179.trimOffspring"),sQuery(id+"F1.wireOp",EDGE,"E180.trimOffspring"),sQuery(id+"F1.wireOp",EDGE,"E181.trimOffspring"),sQuery(id+"F1.wireOp",EDGE,"E182.trimOffspring"),sQuery(id+"F1.wireOp",EDGE,"E183.trimOffspring"),sQuery(id+"F1.wireOp",EDGE,"E184.trimOffspring"),sQuery(id+"F1.wireOp",EDGE,"E185.trimOffspring"),sQuery(id+"F1.wireOp",EDGE,"E186.trimOffspring"),sQuery(id+"F1.wireOp",EDGE,"E187.trimOffspring"),sQuery(id+"F1.wireOp",EDGE,"E188.trimOffspring"),sQuery(id+"F1.wireOp",EDGE,"E189.trimOffspring"),sQuery(id+"F1.wireOp",EDGE,"E190.trimOffspring"),sQuery(id+"F1.wireOp",EDGE,"E191.trimOffspring"),sQuery(id+"F1.wireOp",EDGE,"E192.trimOffspring"),sQuery(id+"F1.wireOp",EDGE,"E193.trimOffspring"),sQuery(id+"F1.wireOp",EDGE,"E194.trimOffspring"),sQuery(id+"F1.wireOp",EDGE,"E195.trimOffspring"),sQuery(id+"F1.wireOp",EDGE,"E196.trimOffspring"),sQuery(id+"F1.wireOp",EDGE,"E197.trimOffspring"),sQuery(id+"F1.wireOp",EDGE,"E198.trimOffspring"),sQuery(id+"F1.wireOp",EDGE,"E199.trimOffspring"),sQuery(id+"F1.wireOp",EDGE,"E200.trimOffspring"),sQuery(id+"F1.wireOp",EDGE,"E201.trimOffspring"),sQuery(id+"F1.wireOp",EDGE,"E202.trimOffspring"),sQuery(id+"F1.wireOp",EDGE,"E203.trimOffspring"),sQuery(id+"F1.wireOp",EDGE,"E204.trimOffspring"),sQuery(id+"F1.wireOp",EDGE,"E205.trimOffspring"),sQuery(id+"F1.wireOp",EDGE,"E206.trimOffspring"),sQuery(id+"F1.wireOp",EDGE,"E207.trimOffspring"),sQuery(id+"F1.wireOp",EDGE,"E208.trimOffspring"),sQuery(id+"F1.wireOp",EDGE,"E209.trimOffspring"),sQuery(id+"F1.wireOp",EDGE,"E210.trimOffspring"),sQuery(id+"F1.wireOp",EDGE,"E211.trimOffspring"),sQuery(id+"F1.wireOp",EDGE,"E212.trimOffspring"),sQuery(id+"F1.wireOp",EDGE,"E213.trimOffspring"),sQuery(id+"F1.wireOp",EDGE,"E214.trimOffspring"),sQuery(id+"F1.wireOp",EDGE,"E215.trimOffspring"),sQuery(id+"F1.wireOp",EDGE,"E216.trimOffspring"),sQuery(id+"F1.wireOp",EDGE,"E217.trimOffspring"),sQuery(id+"F1.wireOp",EDGE,"E218.trimOffspring"),sQuery(id+"F1.wireOp",EDGE,"E219.trimOffspring"),sQuery(id+"F1.wireOp",EDGE,"E220.trimOffspring"),sQuery(id+"F1.wireOp",EDGE,"E221.trimOffspring"),sQuery(id+"F1.wireOp",EDGE,"E222.trimOffspring"),sQuery(id+"F1.wireOp",EDGE,"E223.trimOffspring"),sQuery(id+"F1.wireOp",EDGE,"E224.trimOffspring"),sQuery(id+"F1.wireOp",EDGE,"E225.trimOffspring"),sQuery(id+"F1.wireOp",EDGE,"E226.trimOffspring"),sQuery(id+"F1.wireOp",EDGE,"E227.trimOffspring"),sQuery(id+"F1.wireOp",EDGE,"E228.trimOffspring"),sQuery(id+"F1.wireOp",EDGE,"E229.trimOffspring"),sQuery(id+"F1.wireOp",EDGE,"E230.trimOffspring"),sQuery(id+"F1.wireOp",EDGE,"E231.trimOffspring"),sQuery(id+"F1.wireOp",EDGE,"E232.trimOffspring")])],"isStart":false});
            extrude(context, id + "F14", {"entities" : qUnion([Q0]), "operationType" : NewBodyOperationType.ADD, "depth" : 2.86 * mm});
        }
        {
            var Q0;
            {var subQ0=sQuery(id+"F1.wireOp",EDGE,"E232.trimOffspring");var subQ1=sQuery(id+"F1.wireOp",EDGE,"E231.trimOffspring");var subQ2=sQuery(id+"F1.wireOp",EDGE,"E230.trimOffspring");var subQ3=sQuery(id+"F1.wireOp",EDGE,"E229.trimOffspring");var subQ4=sQuery(id+"F1.wireOp",EDGE,"E228.trimOffspring");var subQ5=sQuery(id+"F1.wireOp",EDGE,"E227.trimOffspring");var subQ6=sQuery(id+"F1.wireOp",EDGE,"E226.trimOffspring");var subQ7=sQuery(id+"F1.wireOp",EDGE,"E225.trimOffspring");var subQ8=sQuery(id+"F1.wireOp",EDGE,"E224.trimOffspring");var subQ9=sQuery(id+"F1.wireOp",EDGE,"E223.trimOffspring");var subQ10=sQuery(id+"F1.wireOp",EDGE,"E222.trimOffspring");var subQ11=sQuery(id+"F1.wireOp",EDGE,"E221.trimOffspring");var subQ12=sQuery(id+"F1.wireOp",EDGE,"E220.trimOffspring");var subQ13=sQuery(id+"F1.wireOp",EDGE,"E219.trimOffspring");var subQ14=sQuery(id+"F1.wireOp",EDGE,"E218.trimOffspring");var subQ15=sQuery(id+"F1.wireOp",EDGE,"E217.trimOffspring");var subQ16=sQuery(id+"F1.wireOp",EDGE,"E216.trimOffspring");var subQ17=sQuery(id+"F1.wireOp",EDGE,"E215.trimOffspring");var subQ18=sQuery(id+"F1.wireOp",EDGE,"E214.trimOffspring");var subQ19=sQuery(id+"F1.wireOp",EDGE,"E213.trimOffspring");var subQ20=sQuery(id+"F1.wireOp",EDGE,"E212.trimOffspring");var subQ21=sQuery(id+"F1.wireOp",EDGE,"E211.trimOffspring");var subQ22=sQuery(id+"F1.wireOp",EDGE,"E210.trimOffspring");var subQ23=sQuery(id+"F1.wireOp",EDGE,"E209.trimOffspring");var subQ24=sQuery(id+"F1.wireOp",EDGE,"E208.trimOffspring");var subQ25=sQuery(id+"F1.wireOp",EDGE,"E207.trimOffspring");var subQ26=sQuery(id+"F1.wireOp",EDGE,"E206.trimOffspring");var subQ27=sQuery(id+"F1.wireOp",EDGE,"E205.trimOffspring");var subQ28=sQuery(id+"F1.wireOp",EDGE,"E204.trimOffspring");var subQ29=sQuery(id+"F1.wireOp",EDGE,"E203.trimOffspring");var subQ30=sQuery(id+"F1.wireOp",EDGE,"E202.trimOffspring");var subQ31=sQuery(id+"F1.wireOp",EDGE,"E201.trimOffspring");var subQ32=sQuery(id+"F1.wireOp",EDGE,"E200.trimOffspring");var subQ33=sQuery(id+"F1.wireOp",EDGE,"E199.trimOffspring");var subQ34=sQuery(id+"F1.wireOp",EDGE,"E198.trimOffspring");var subQ35=sQuery(id+"F1.wireOp",EDGE,"E197.trimOffspring");var subQ36=sQuery(id+"F1.wireOp",EDGE,"E196.trimOffspring");var subQ37=sQuery(id+"F1.wireOp",EDGE,"E195.trimOffspring");var subQ38=sQuery(id+"F1.wireOp",EDGE,"E194.trimOffspring");var subQ39=sQuery(id+"F1.wireOp",EDGE,"E193.trimOffspring");var subQ40=sQuery(id+"F1.wireOp",EDGE,"E192.trimOffspring");var subQ41=sQuery(id+"F1.wireOp",EDGE,"E191.trimOffspring");var subQ42=sQuery(id+"F1.wireOp",EDGE,"E190.trimOffspring");var subQ43=sQuery(id+"F1.wireOp",EDGE,"E189.trimOffspring");var subQ44=sQuery(id+"F1.wireOp",EDGE,"E188.trimOffspring");var subQ45=sQuery(id+"F1.wireOp",EDGE,"E187.trimOffspring");var subQ46=sQuery(id+"F1.wireOp",EDGE,"E186.trimOffspring");var subQ47=sQuery(id+"F1.wireOp",EDGE,"E185.trimOffspring");var subQ48=sQuery(id+"F1.wireOp",EDGE,"E184.trimOffspring");var subQ49=sQuery(id+"F1.wireOp",EDGE,"E183.trimOffspring");var subQ50=sQuery(id+"F1.wireOp",EDGE,"E182.trimOffspring");var subQ51=sQuery(id+"F1.wireOp",EDGE,"E181.trimOffspring");var subQ52=sQuery(id+"F1.wireOp",EDGE,"E180.trimOffspring");var subQ53=sQuery(id+"F1.wireOp",EDGE,"E179.trimOffspring");var subQ54=sQuery(id+"F1.wireOp",EDGE,"E178.trimOffspring");var subQ55=sQuery(id+"F1.wireOp",EDGE,"E177.trimOffspring");var subQ56=sQuery(id+"F1.wireOp",EDGE,"E176.trimOffspring");var subQ57=sQuery(id+"F1.wireOp",EDGE,"E175.trimOffspring");var subQ58=sQuery(id+"F1.wireOp",EDGE,"E174.trimOffspring");var subQ59=sQuery(id+"F1.wireOp",EDGE,"E173.trimOffspring");var subQ60=sQuery(id+"F1.wireOp",EDGE,"E172.trimOffspring");var subQ61=sQuery(id+"F1.wireOp",EDGE,"E171.trimOffspring");var subQ62=sQuery(id+"F1.wireOp",EDGE,"E170.trimOffspring");var subQ63=sQuery(id+"F1.wireOp",EDGE,"E169.trimOffspring");var subQ64=sQuery(id+"F1.wireOp",EDGE,"E168.trimOffspring");var subQ65=sQuery(id+"F1.wireOp",EDGE,"E167.trimOffspring");var subQ66=sQuery(id+"F1.wireOp",EDGE,"E166.trimOffspring");var subQ67=sQuery(id+"F1.wireOp",EDGE,"E165.trimOffspring");var subQ68=sQuery(id+"F1.wireOp",EDGE,"E164.trimOffspring");var subQ69=sQuery(id+"F1.wireOp",EDGE,"E163.trimOffspring");var subQ70=sQuery(id+"F1.wireOp",EDGE,"E162.trimOffspring");var subQ71=sQuery(id+"F1.wireOp",EDGE,"E161.trimOffspring");var subQ72=sQuery(id+"F1.wireOp",EDGE,"E160.trimOffspring");var subQ73=sQuery(id+"F1.wireOp",EDGE,"E159.trimOffspring");var subQ74=sQuery(id+"F1.wireOp",EDGE,"E158.trimOffspring");var subQ75=sQuery(id+"F1.wireOp",EDGE,"E157.trimOffspring");var subQ76=sQuery(id+"F1.wireOp",EDGE,"E156.trimOffspring");var subQ77=sQuery(id+"F1.wireOp",EDGE,"E155.trimOffspring");var subQ78=sQuery(id+"F1.wireOp",EDGE,"E154.trimOffspring");var subQ79=sQuery(id+"F1.wireOp",EDGE,"E153.trimOffspring");var subQ80=sQuery(id+"F1.wireOp",EDGE,"E152.trimOffspring");var subQ81=sQuery(id+"F1.wireOp",EDGE,"E151.trimOffspring");var subQ82=sQuery(id+"F1.wireOp",EDGE,"E150.trimOffspring");var subQ83=sQuery(id+"F1.wireOp",EDGE,"E149.trimOffspring");var subQ84=sQuery(id+"F1.wireOp",EDGE,"E148.trimOffspring");var subQ85=sQuery(id+"F1.wireOp",EDGE,"E147.trimOffspring");var subQ86=sQuery(id+"F1.wireOp",EDGE,"E146.trimOffspring");var subQ87=sQuery(id+"F1.wireOp",EDGE,"E145.trimOffspring");var subQ88=sQuery(id+"F1.wireOp",EDGE,"E144.trimOffspring");var subQ89=sQuery(id+"F1.wireOp",EDGE,"E143.trimOffspring");var subQ90=sQuery(id+"F1.wireOp",EDGE,"E142.trimOffspring");var subQ91=sQuery(id+"F1.wireOp",EDGE,"E141.trimOffspring");var subQ92=sQuery(id+"F1.wireOp",EDGE,"E140.trimOffspring");var subQ93=sQuery(id+"F1.wireOp",EDGE,"E139.trimOffspring");var subQ94=sQuery(id+"F1.wireOp",EDGE,"E138.trimOffspring");var subQ95=sQuery(id+"F1.wireOp",EDGE,"E137.trimOffspring");var subQ96=sQuery(id+"F1.wireOp",EDGE,"E136.trimOffspring");var subQ97=sQuery(id+"F1.wireOp",EDGE,"E135.trimOffspring");var subQ98=sQuery(id+"F1.wireOp",EDGE,"E134.trimOffspring");var subQ99=sQuery(id+"F1.wireOp",EDGE,"E133.trimOffspring");var subQ100=sQuery(id+"F1.wireOp",EDGE,"E132.trimOffspring");var subQ101=sQuery(id+"F1.wireOp",EDGE,"E131.trimOffspring");var subQ102=sQuery(id+"F1.wireOp",EDGE,"E130.trimOffspring");var subQ103=sQuery(id+"F1.wireOp",EDGE,"E129.trimOffspring");var subQ104=sQuery(id+"F1.wireOp",EDGE,"E128.trimOffspring");var subQ105=sQuery(id+"F1.wireOp",EDGE,"E127.trimOffspring");var subQ106=sQuery(id+"F1.wireOp",EDGE,"E126.trimOffspring");var subQ107=sQuery(id+"F1.wireOp",EDGE,"E125.trimOffspring");var subQ108=sQuery(id+"F1.wireOp",EDGE,"E124.trimOffspring");var subQ109=sQuery(id+"F1.wireOp",EDGE,"E123.trimOffspring");var subQ110=sQuery(id+"F1.wireOp",EDGE,"E122.trimOffspring");var subQ111=sQuery(id+"F1.wireOp",EDGE,"E121.trimOffspring");var subQ112=sQuery(id+"F1.wireOp",EDGE,"E120.trimOffspring");var subQ113=sQuery(id+"F1.wireOp",EDGE,"E119.trimOffspring");var subQ114=sQuery(id+"F1.wireOp",EDGE,"E118.trimOffspring");var subQ115=sQuery(id+"F1.wireOp",EDGE,"E117.trimOffspring");var subQ116=sQuery(id+"F1.wireOp",EDGE,"E116.trimOffspring");var subQ117=sQuery(id+"F1.wireOp",EDGE,"E115.trimOffspring");var subQ118=sQuery(id+"F1.wireOp",EDGE,"E114.trimOffspring");var subQ119=sQuery(id+"F1.wireOp",EDGE,"E113.trimOffspring");var subQ120=sQuery(id+"F1.wireOp",EDGE,"E112.trimOffspring");var subQ121=sQuery(id+"F1.wireOp",EDGE,"E111.trimOffspring");var subQ122=sQuery(id+"F1.wireOp",EDGE,"E110.trimOffspring");var subQ123=sQuery(id+"F1.wireOp",EDGE,"E109.trimOffspring");var subQ124=sQuery(id+"F1.wireOp",EDGE,"E108.trimOffspring");var subQ125=sQuery(id+"F1.wireOp",EDGE,"E107.trimOffspring");var subQ126=sQuery(id+"F1.wireOp",EDGE,"E106.trimOffspring");var subQ127=sQuery(id+"F1.wireOp",EDGE,"E105.trimOffspring");var subQ128=sQuery(id+"F1.wireOp",EDGE,"E104.trimOffspring");var subQ129=sQuery(id+"F1.wireOp",EDGE,"E103.trimOffspring");var subQ130=sQuery(id+"F1.wireOp",EDGE,"E102.trimOffspring");var subQ131=sQuery(id+"F1.wireOp",EDGE,"E101.trimOffspring");var subQ132=sQuery(id+"F1.wireOp",EDGE,"E100.trimOffspring");var subQ133=sQuery(id+"F1.wireOp",EDGE,"E99.trimOffspring");var subQ134=sQuery(id+"F1.wireOp",EDGE,"E98.trimOffspring");var subQ135=sQuery(id+"F1.wireOp",EDGE,"E97.trimOffspring");var subQ136=sQuery(id+"F1.wireOp",EDGE,"E96.trimOffspring");var subQ137=sQuery(id+"F1.wireOp",EDGE,"E95.trimOffspring");var subQ138=sQuery(id+"F1.wireOp",EDGE,"E94.trimOffspring");var subQ139=sQuery(id+"F1.wireOp",EDGE,"E93.trimOffspring");var subQ140=sQuery(id+"F1.wireOp",EDGE,"E92.trimOffspring");var subQ141=sQuery(id+"F1.wireOp",EDGE,"E91.trimOffspring");var subQ142=sQuery(id+"F1.wireOp",EDGE,"E90");var subQ143=sQuery(id+"F1.wireOp",EDGE,"E89");var subQ144=sQuery(id+"F1.wireOp",EDGE,"E88.right");var subQ145=sQuery(id+"F1.wireOp",EDGE,"E88.left");var subQ146=sQuery(id+"F1.wireOp",EDGE,"E87.filletArc");var subQ147=sQuery(id+"F1.wireOp",EDGE,"E86.filletArc");var subQ148=sQuery(id+"F1.wireOp",EDGE,"E85.filletArc");var subQ149=sQuery(id+"F1.wireOp",EDGE,"E84.filletArc");var subQ150=sQuery(id+"F1.wireOp",EDGE,"E83.filletArc");var subQ151=sQuery(id+"F1.wireOp",EDGE,"E82.filletArc");var subQ152=sQuery(id+"F1.wireOp",EDGE,"E81.filletArc");var subQ153=sQuery(id+"F1.wireOp",EDGE,"E80.filletArc");var subQ154=sQuery(id+"F1.wireOp",EDGE,"E79.right");var subQ155=sQuery(id+"F1.wireOp",EDGE,"E79.left");var subQ156=sQuery(id+"F1.wireOp",EDGE,"E78.right");var subQ157=sQuery(id+"F1.wireOp",EDGE,"E78.left");var subQ158=sQuery(id+"F1.wireOp",EDGE,"E77.right");var subQ159=sQuery(id+"F1.wireOp",EDGE,"E77.left");var subQ160=sQuery(id+"F1.wireOp",EDGE,"E76.right");var subQ161=sQuery(id+"F1.wireOp",EDGE,"E76.left");var subQ162=sQuery(id+"F1.wireOp",EDGE,"E75.right");var subQ163=sQuery(id+"F1.wireOp",EDGE,"E75.left");var subQ164=sQuery(id+"F1.wireOp",EDGE,"E74.right");var subQ165=sQuery(id+"F1.wireOp",EDGE,"E74.left");var subQ166=sQuery(id+"F1.wireOp",EDGE,"E73.right");var subQ167=sQuery(id+"F1.wireOp",EDGE,"E73.left");var subQ168=sQuery(id+"F1.wireOp",EDGE,"E72.right");var subQ169=sQuery(id+"F1.wireOp",EDGE,"E72.left");var subQ170=sQuery(id+"F1.wireOp",EDGE,"E71.right");var subQ171=sQuery(id+"F1.wireOp",EDGE,"E71.left");var subQ172=sQuery(id+"F1.wireOp",EDGE,"E70.right");var subQ173=sQuery(id+"F1.wireOp",EDGE,"E70.left");var subQ174=sQuery(id+"F1.wireOp",EDGE,"E69.right");var subQ175=sQuery(id+"F1.wireOp",EDGE,"E69.left");var subQ176=sQuery(id+"F1.wireOp",EDGE,"E68.right");var subQ177=sQuery(id+"F1.wireOp",EDGE,"E68.left");var subQ178=sQuery(id+"F1.wireOp",EDGE,"E67.right");var subQ179=sQuery(id+"F1.wireOp",EDGE,"E67.left");var subQ180=sQuery(id+"F1.wireOp",EDGE,"E66.right");var subQ181=sQuery(id+"F1.wireOp",EDGE,"E66.left");var subQ182=sQuery(id+"F1.wireOp",EDGE,"E65.right");var subQ183=sQuery(id+"F1.wireOp",EDGE,"E65.left");var subQ184=sQuery(id+"F1.wireOp",EDGE,"E64.right");var subQ185=sQuery(id+"F1.wireOp",EDGE,"E64.left");var subQ186=sQuery(id+"F1.wireOp",EDGE,"E63.right");var subQ187=sQuery(id+"F1.wireOp",EDGE,"E63.left");var subQ188=sQuery(id+"F1.wireOp",EDGE,"E62.right");var subQ189=sQuery(id+"F1.wireOp",EDGE,"E62.left");var subQ190=sQuery(id+"F1.wireOp",EDGE,"E61.right");var subQ191=sQuery(id+"F1.wireOp",EDGE,"E61.left");var subQ192=sQuery(id+"F1.wireOp",EDGE,"E60.right");var subQ193=sQuery(id+"F1.wireOp",EDGE,"E60.left");var subQ194=sQuery(id+"F1.wireOp",EDGE,"E59.right");var subQ195=sQuery(id+"F1.wireOp",EDGE,"E59.left");var subQ196=sQuery(id+"F1.wireOp",EDGE,"E58.right");var subQ197=sQuery(id+"F1.wireOp",EDGE,"E58.left");var subQ198=sQuery(id+"F1.wireOp",EDGE,"E57.right");var subQ199=sQuery(id+"F1.wireOp",EDGE,"E57.left");var subQ200=sQuery(id+"F1.wireOp",EDGE,"E56.right");var subQ201=sQuery(id+"F1.wireOp",EDGE,"E56.left");var subQ202=sQuery(id+"F1.wireOp",EDGE,"E55.right");var subQ203=sQuery(id+"F1.wireOp",EDGE,"E55.left");var subQ204=sQuery(id+"F1.wireOp",EDGE,"E54.right");var subQ205=sQuery(id+"F1.wireOp",EDGE,"E54.left");var subQ206=sQuery(id+"F1.wireOp",EDGE,"E53.right");var subQ207=sQuery(id+"F1.wireOp",EDGE,"E53.left");var subQ208=sQuery(id+"F1.wireOp",EDGE,"E52.right");var subQ209=sQuery(id+"F1.wireOp",EDGE,"E52.left");var subQ210=sQuery(id+"F1.wireOp",EDGE,"E51.right");var subQ211=sQuery(id+"F1.wireOp",EDGE,"E51.left");var subQ212=sQuery(id+"F1.wireOp",EDGE,"E50.right");var subQ213=sQuery(id+"F1.wireOp",EDGE,"E49.right");var subQ214=sQuery(id+"F1.wireOp",EDGE,"E49.left");var subQ215=sQuery(id+"F1.wireOp",EDGE,"E48.right");var subQ216=sQuery(id+"F1.wireOp",EDGE,"E48.left");var subQ217=sQuery(id+"F1.wireOp",EDGE,"E47.right");var subQ218=sQuery(id+"F1.wireOp",EDGE,"E47.left");var subQ219=sQuery(id+"F1.wireOp",EDGE,"E46.right");var subQ220=sQuery(id+"F1.wireOp",EDGE,"E46.left");var subQ221=sQuery(id+"F1.wireOp",EDGE,"E45.right");var subQ222=sQuery(id+"F1.wireOp",EDGE,"E45.left");var subQ223=sQuery(id+"F1.wireOp",EDGE,"E44.right");var subQ224=sQuery(id+"F1.wireOp",EDGE,"E44.left");var subQ225=sQuery(id+"F1.wireOp",EDGE,"E43.right");var subQ226=sQuery(id+"F1.wireOp",EDGE,"E43.left");var subQ227=sQuery(id+"F1.wireOp",EDGE,"E42.right");var subQ228=sQuery(id+"F1.wireOp",EDGE,"E42.left");var subQ229=sQuery(id+"F1.wireOp",EDGE,"E41.right");var subQ230=sQuery(id+"F1.wireOp",EDGE,"E41.left");var subQ231=sQuery(id+"F1.wireOp",EDGE,"E40.right");var subQ232=sQuery(id+"F1.wireOp",EDGE,"E40.left");var subQ233=sQuery(id+"F1.wireOp",EDGE,"E39.right");var subQ234=sQuery(id+"F1.wireOp",EDGE,"E39.left");var subQ235=sQuery(id+"F1.wireOp",EDGE,"E38.right");var subQ236=sQuery(id+"F1.wireOp",EDGE,"E38.left");var subQ237=sQuery(id+"F1.wireOp",EDGE,"E37.right");var subQ238=sQuery(id+"F1.wireOp",EDGE,"E37.left");var subQ239=sQuery(id+"F1.wireOp",EDGE,"E36.right");var subQ240=sQuery(id+"F1.wireOp",EDGE,"E36.left");var subQ241=sQuery(id+"F1.wireOp",EDGE,"E35.right");var subQ242=sQuery(id+"F1.wireOp",EDGE,"E35.left");var subQ243=sQuery(id+"F1.wireOp",EDGE,"E34.right");var subQ244=sQuery(id+"F1.wireOp",EDGE,"E34.left");var subQ245=sQuery(id+"F1.wireOp",EDGE,"E33.right");var subQ246=sQuery(id+"F1.wireOp",EDGE,"E33.left");var subQ247=sQuery(id+"F1.wireOp",EDGE,"E32.right");var subQ248=sQuery(id+"F1.wireOp",EDGE,"E32.left");var subQ249=sQuery(id+"F1.wireOp",EDGE,"E31.right");var subQ250=sQuery(id+"F1.wireOp",EDGE,"E31.left");var subQ251=sQuery(id+"F1.wireOp",EDGE,"E30.right");var subQ252=sQuery(id+"F1.wireOp",EDGE,"E30.left");var subQ253=sQuery(id+"F1.wireOp",EDGE,"E29.right");var subQ254=sQuery(id+"F1.wireOp",EDGE,"E29.left");var subQ255=sQuery(id+"F1.wireOp",EDGE,"E28.right");var subQ256=sQuery(id+"F1.wireOp",EDGE,"E28.left");var subQ257=sQuery(id+"F1.wireOp",EDGE,"E27.right");var subQ258=sQuery(id+"F1.wireOp",EDGE,"E27.left");var subQ259=sQuery(id+"F1.wireOp",EDGE,"E26.right");var subQ260=sQuery(id+"F1.wireOp",EDGE,"E26.left");var subQ261=sQuery(id+"F1.wireOp",EDGE,"E25.right");var subQ262=sQuery(id+"F1.wireOp",EDGE,"E25.left");var subQ263=sQuery(id+"F1.wireOp",EDGE,"E24.right");var subQ264=sQuery(id+"F1.wireOp",EDGE,"E24.left");var subQ265=sQuery(id+"F1.wireOp",EDGE,"E23.right");var subQ266=sQuery(id+"F1.wireOp",EDGE,"E23.left");var subQ267=sQuery(id+"F1.wireOp",EDGE,"E22.right");var subQ268=sQuery(id+"F1.wireOp",EDGE,"E22.left");var subQ269=sQuery(id+"F1.wireOp",EDGE,"E21.right");var subQ270=sQuery(id+"F1.wireOp",EDGE,"E21.left");var subQ271=sQuery(id+"F1.wireOp",EDGE,"E20.right");var subQ272=sQuery(id+"F1.wireOp",EDGE,"E20.left");var subQ273=sQuery(id+"F1.wireOp",EDGE,"E19.right");var subQ274=sQuery(id+"F1.wireOp",EDGE,"E19.left");var subQ275=sQuery(id+"F1.wireOp",EDGE,"E18.right");var subQ276=sQuery(id+"F1.wireOp",EDGE,"E18.left");var subQ277=sQuery(id+"F1.wireOp",EDGE,"E17.top");var subQ278=sQuery(id+"F1.wireOp",EDGE,"E16.top");var subQ279=sQuery(id+"F1.wireOp",EDGE,"E15.top");var subQ280=sQuery(id+"F1.wireOp",EDGE,"E14.right");var subQ281=sQuery(id+"F1.wireOp",EDGE,"E14.left");var subQ282=sQuery(id+"F1.wireOp",EDGE,"E13.right");var subQ283=sQuery(id+"F1.wireOp",EDGE,"E13.left");var subQ284=sQuery(id+"F1.wireOp",EDGE,"E12.right");var subQ285=sQuery(id+"F1.wireOp",EDGE,"E12.left");var subQ286=sQuery(id+"F1.wireOp",EDGE,"E11.right");var subQ287=sQuery(id+"F1.wireOp",EDGE,"E11.left");var subQ288=sQuery(id+"F1.wireOp",EDGE,"E10.top");var subQ289=sQuery(id+"F1.wireOp",EDGE,"E10.bottom");var subQ290=sQuery(id+"F1.wireOp",EDGE,"E9.top");var subQ291=sQuery(id+"F1.wireOp",EDGE,"E9.bottom");var subQ292=sQuery(id+"F1.wireOp",EDGE,"E8.top");var subQ293=sQuery(id+"F1.wireOp",EDGE,"E8.bottom");var subQ294=sQuery(id+"F1.wireOp",EDGE,"E7.top");var subQ295=sQuery(id+"F1.wireOp",EDGE,"E7.bottom");var subQ296=sQuery(id+"F1.wireOp",EDGE,"E6.top");var subQ297=sQuery(id+"F1.wireOp",EDGE,"E6.bottom");var subQ298=sQuery(id+"F1.wireOp",EDGE,"E5.right");var subQ299=sQuery(id+"F1.wireOp",EDGE,"E5.left");var subQ300=sQuery(id+"F1.wireOp",EDGE,"E4");var subQ301=sQuery(id+"F1.wireOp",EDGE,"E3");var subQ302=sQuery(id+"F1.wireOp",EDGE,"E2");var subQ303=sQuery(id+"F1.wireOp",EDGE,"E1.0");Q0=makeQuery(id+"F14.opExtrude","SWEPT_FACE",FACE,{"disambiguationData":[OSD([subQ303,subQ302,subQ301,subQ300,subQ299,subQ298,subQ297,subQ296,subQ295,subQ294,subQ293,subQ292,subQ291,subQ290,subQ289,subQ288,subQ287,subQ286,subQ285,subQ284,subQ283,subQ282,subQ281,subQ280,subQ279,subQ278,subQ277,subQ276,subQ275,subQ274,subQ273,subQ272,subQ271,subQ270,subQ269,subQ268,subQ267,subQ266,subQ265,subQ264,subQ263,subQ262,subQ261,subQ260,subQ259,subQ258,subQ257,subQ256,subQ255,subQ254,subQ253,subQ252,subQ251,subQ250,subQ249,subQ248,subQ247,subQ246,subQ245,subQ244,subQ243,subQ242,subQ241,subQ240,subQ239,subQ238,subQ237,subQ236,subQ235,subQ234,subQ233,subQ232,subQ231,subQ230,subQ229,subQ228,subQ227,subQ226,subQ225,subQ224,subQ223,subQ222,subQ221,subQ220,subQ219,subQ218,subQ217,subQ216,subQ215,subQ214,subQ213,subQ212,subQ211,subQ210,subQ209,subQ208,subQ207,subQ206,subQ205,subQ204,subQ203,subQ202,subQ201,subQ200,subQ199,subQ198,subQ197,subQ196,subQ195,subQ194,subQ193,subQ192,subQ191,subQ190,subQ189,subQ188,subQ187,subQ186,subQ185,subQ184,subQ183,subQ182,subQ181,subQ180,subQ179,subQ178,subQ177,subQ176,subQ175,subQ174,subQ173,subQ172,subQ171,subQ170,subQ169,subQ168,subQ167,subQ166,subQ165,subQ164,subQ163,subQ162,subQ161,subQ160,subQ159,subQ158,subQ157,subQ156,subQ155,subQ154,subQ153,subQ152,subQ151,subQ150,subQ149,subQ148,subQ147,subQ146,subQ145,subQ144,subQ143,subQ142,subQ141,subQ140,subQ139,subQ138,subQ137,subQ136,subQ135,subQ134,subQ133,subQ132,subQ131,subQ130,subQ129,subQ128,subQ127,subQ126,subQ125,subQ124,subQ123,subQ122,subQ121,subQ120,subQ119,subQ118,subQ117,subQ116,subQ115,subQ114,subQ113,subQ112,subQ111,subQ110,subQ109,subQ108,subQ107,subQ106,subQ105,subQ104,subQ103,subQ102,subQ101,subQ100,subQ99,subQ98,subQ97,subQ96,subQ95,subQ94,subQ93,subQ92,subQ91,subQ90,subQ89,subQ88,subQ87,subQ86,subQ85,subQ84,subQ83,subQ82,subQ81,subQ80,subQ79,subQ78,subQ77,subQ76,subQ75,subQ74,subQ73,subQ72,subQ71,subQ70,subQ69,subQ68,subQ67,subQ66,subQ65,subQ64,subQ63,subQ62,subQ61,subQ60,subQ59,subQ58,subQ57,subQ56,subQ55,subQ54,subQ53,subQ52,subQ51,subQ50,subQ49,subQ48,subQ47,subQ46,subQ45,subQ44,subQ43,subQ42,subQ41,subQ40,subQ39,subQ38,subQ37,subQ36,subQ35,subQ34,subQ33,subQ32,subQ31,subQ30,subQ29,subQ28,subQ27,subQ26,subQ25,subQ24,subQ23,subQ22,subQ21,subQ20,subQ19,subQ18,subQ17,subQ16,subQ15,subQ14,subQ13,subQ12,subQ11,subQ10,subQ9,subQ8,subQ7,subQ6,subQ5,subQ4,subQ3,subQ2,subQ1,subQ0]),TDD([makeQuery(id+"F3.opFillet","BLEND_EDGE",EDGE,{"blendedFrom":[makeQuery(id+"F2.opExtrude","CAP_EDGE",EDGE,{"disambiguationData":[OSD([subQ302])],"isStart":true}),makeQuery(id+"F2.opExtrude","CAP_FACE",FACE,{"disambiguationData":[OSD([subQ303,subQ302,subQ301,subQ300,subQ299,subQ298,subQ297,subQ296,subQ295,subQ294,subQ293,subQ292,subQ291,subQ290,subQ289,subQ288,subQ287,subQ286,subQ285,subQ284,subQ283,subQ282,subQ281,subQ280,subQ279,subQ278,subQ277,subQ276,subQ275,subQ274,subQ273,subQ272,subQ271,subQ270,subQ269,subQ268,subQ267,subQ266,subQ265,subQ264,subQ263,subQ262,subQ261,subQ260,subQ259,subQ258,subQ257,subQ256,subQ255,subQ254,subQ253,subQ252,subQ251,subQ250,subQ249,subQ248,subQ247,subQ246,subQ245,subQ244,subQ243,subQ242,subQ241,subQ240,subQ239,subQ238,subQ237,subQ236,subQ235,subQ234,subQ233,subQ232,subQ231,subQ230,subQ229,subQ228,subQ227,subQ226,subQ225,subQ224,subQ223,subQ222,subQ221,subQ220,subQ219,subQ218,subQ217,subQ216,subQ215,subQ214,subQ213,subQ212,subQ211,subQ210,subQ209,subQ208,subQ207,subQ206,subQ205,subQ204,subQ203,subQ202,subQ201,subQ200,subQ199,subQ198,subQ197,subQ196,subQ195,subQ194,subQ193,subQ192,subQ191,subQ190,subQ189,subQ188,subQ187,subQ186,subQ185,subQ184,subQ183,subQ182,subQ181,subQ180,subQ179,subQ178,subQ177,subQ176,subQ175,subQ174,subQ173,subQ172,subQ171,subQ170,subQ169,subQ168,subQ167,subQ166,subQ165,subQ164,subQ163,subQ162,subQ161,subQ160,subQ159,subQ158,subQ157,subQ156,subQ155,subQ154,subQ153,subQ152,subQ151,subQ150,subQ149,subQ148,subQ147,subQ146,subQ145,subQ144,subQ143,subQ142,subQ141,subQ140,subQ139,subQ138,subQ137,subQ136,subQ135,subQ134,subQ133,subQ132,subQ131,subQ130,subQ129,subQ128,subQ127,subQ126,subQ125,subQ124,subQ123,subQ122,subQ121,subQ120,subQ119,subQ118,subQ117,subQ116,subQ115,subQ114,subQ113,subQ112,subQ111,subQ110,subQ109,subQ108,subQ107,subQ106,subQ105,subQ104,subQ103,subQ102,subQ101,subQ100,subQ99,subQ98,subQ97,subQ96,subQ95,subQ94,subQ93,subQ92,subQ91,subQ90,subQ89,subQ88,subQ87,subQ86,subQ85,subQ84,subQ83,subQ82,subQ81,subQ80,subQ79,subQ78,subQ77,subQ76,subQ75,subQ74,subQ73,subQ72,subQ71,subQ70,subQ69,subQ68,subQ67,subQ66,subQ65,subQ64,subQ63,subQ62,subQ61,subQ60,subQ59,subQ58,subQ57,subQ56,subQ55,subQ54,subQ53,subQ52,subQ51,subQ50,subQ49,subQ48,subQ47,subQ46,subQ45,subQ44,subQ43,subQ42,subQ41,subQ40,subQ39,subQ38,subQ37,subQ36,subQ35,subQ34,subQ33,subQ32,subQ31,subQ30,subQ29,subQ28,subQ27,subQ26,subQ25,subQ24,subQ23,subQ22,subQ21,subQ20,subQ19,subQ18,subQ17,subQ16,subQ15,subQ14,subQ13,subQ12,subQ11,subQ10,subQ9,subQ8,subQ7,subQ6,subQ5,subQ4,subQ3,subQ2,subQ1,subQ0])],"isStart":false})],"blendedInto":[makeQuery(id+"F2.opExtrude","CAP_FACE",FACE,{"disambiguationData":[OSD([subQ303,subQ302,subQ301,subQ300,subQ299,subQ298,subQ297,subQ296,subQ295,subQ294,subQ293,subQ292,subQ291,subQ290,subQ289,subQ288,subQ287,subQ286,subQ285,subQ284,subQ283,subQ282,subQ281,subQ280,subQ279,subQ278,subQ277,subQ276,subQ275,subQ274,subQ273,subQ272,subQ271,subQ270,subQ269,subQ268,subQ267,subQ266,subQ265,subQ264,subQ263,subQ262,subQ261,subQ260,subQ259,subQ258,subQ257,subQ256,subQ255,subQ254,subQ253,subQ252,subQ251,subQ250,subQ249,subQ248,subQ247,subQ246,subQ245,subQ244,subQ243,subQ242,subQ241,subQ240,subQ239,subQ238,subQ237,subQ236,subQ235,subQ234,subQ233,subQ232,subQ231,subQ230,subQ229,subQ228,subQ227,subQ226,subQ225,subQ224,subQ223,subQ222,subQ221,subQ220,subQ219,subQ218,subQ217,subQ216,subQ215,subQ214,subQ213,subQ212,subQ211,subQ210,subQ209,subQ208,subQ207,subQ206,subQ205,subQ204,subQ203,subQ202,subQ201,subQ200,subQ199,subQ198,subQ197,subQ196,subQ195,subQ194,subQ193,subQ192,subQ191,subQ190,subQ189,subQ188,subQ187,subQ186,subQ185,subQ184,subQ183,subQ182,subQ181,subQ180,subQ179,subQ178,subQ177,subQ176,subQ175,subQ174,subQ173,subQ172,subQ171,subQ170,subQ169,subQ168,subQ167,subQ166,subQ165,subQ164,subQ163,subQ162,subQ161,subQ160,subQ159,subQ158,subQ157,subQ156,subQ155,subQ154,subQ153,subQ152,subQ151,subQ150,subQ149,subQ148,subQ147,subQ146,subQ145,subQ144,subQ143,subQ142,subQ141,subQ140,subQ139,subQ138,subQ137,subQ136,subQ135,subQ134,subQ133,subQ132,subQ131,subQ130,subQ129,subQ128,subQ127,subQ126,subQ125,subQ124,subQ123,subQ122,subQ121,subQ120,subQ119,subQ118,subQ117,subQ116,subQ115,subQ114,subQ113,subQ112,subQ111,subQ110,subQ109,subQ108,subQ107,subQ106,subQ105,subQ104,subQ103,subQ102,subQ101,subQ100,subQ99,subQ98,subQ97,subQ96,subQ95,subQ94,subQ93,subQ92,subQ91,subQ90,subQ89,subQ88,subQ87,subQ86,subQ85,subQ84,subQ83,subQ82,subQ81,subQ80,subQ79,subQ78,subQ77,subQ76,subQ75,subQ74,subQ73,subQ72,subQ71,subQ70,subQ69,subQ68,subQ67,subQ66,subQ65,subQ64,subQ63,subQ62,subQ61,subQ60,subQ59,subQ58,subQ57,subQ56,subQ55,subQ54,subQ53,subQ52,subQ51,subQ50,subQ49,subQ48,subQ47,subQ46,subQ45,subQ44,subQ43,subQ42,subQ41,subQ40,subQ39,subQ38,subQ37,subQ36,subQ35,subQ34,subQ33,subQ32,subQ31,subQ30,subQ29,subQ28,subQ27,subQ26,subQ25,subQ24,subQ23,subQ22,subQ21,subQ20,subQ19,subQ18,subQ17,subQ16,subQ15,subQ14,subQ13,subQ12,subQ11,subQ10,subQ9,subQ8,subQ7,subQ6,subQ5,subQ4,subQ3,subQ2,subQ1,subQ0])],"isStart":false})]})])]});}
            var sketch = newSketch(context, id + "F15", { "sketchPlane" : qUnion([Q0])});
            skLineSegment(sketch, "E236.bottom", {"start": v(267.08, 5.86) * mm, "end": v(276.54, 5.86) * mm});
            skLineSegment(sketch, "E236.top", {"start": v(267.08, 3) * mm, "end": v(276.54, 3) * mm});
            skLineSegment(sketch, "E236.left", {"start": v(267.08, 5.86) * mm, "end": v(267.08, 3) * mm});
            skLineSegment(sketch, "E236.right", {"start": v(276.54, 5.86) * mm, "end": v(276.54, 3) * mm});
            skSolve(sketch);
        }
        {
            var Q0;
            Q0=makeQuery(id+"F15.imprint","IMPRINT",FACE,{"disambiguationData":[TD([[makeQuery(id+"F15.imprint","IMPRINT",EDGE,{"derivedFrom":sQuery(id+"F15.wireOp",EDGE,"E236.bottom")}),1.0]])]});
            extrude(context, id + "F16", {"entities" : qUnion([Q0]), "operationType" : NewBodyOperationType.ADD, "depth" : 5 * mm});
        }
        {
            var Q0;
            Q0=makeQuery(id+"F16.opExtrude","SWEPT_FACE",FACE,{"disambiguationData":[OSD([sQuery(id+"F15.wireOp",EDGE,"E236.top")])]});
            var sketch = newSketch(context, id + "F17", { "sketchPlane" : qUnion([Q0])});
            skLineSegment(sketch, "E237.bottom", {"start": v(-1293.18, 267.08) * mm, "end": v(-1290.68, 267.08) * mm});
            skLineSegment(sketch, "E237.top", {"start": v(-1293.18, 276.54) * mm, "end": v(-1290.68, 276.54) * mm});
            skLineSegment(sketch, "E237.left", {"start": v(-1293.18, 267.08) * mm, "end": v(-1293.18, 276.54) * mm});
            skLineSegment(sketch, "E237.right", {"start": v(-1290.68, 267.08) * mm, "end": v(-1290.68, 276.54) * mm});
            skSolve(sketch);
        }
        {
            var Q0;
            Q0=makeQuery(id+"F17.imprint","IMPRINT",FACE,{"disambiguationData":[TD([[makeQuery(id+"F17.imprint","IMPRINT",EDGE,{"derivedFrom":sQuery(id+"F17.wireOp",EDGE,"E237.bottom")}),1.0]])]});
            extrude(context, id + "F18", {"entities" : qUnion([Q0]), "operationType" : NewBodyOperationType.ADD, "depth" : 19.05 * mm});
        }
        {
            var Q0;
            Q0=makeQuery(id+"F18.opExtrude","SWEPT_FACE",FACE,{"disambiguationData":[OSD([sQuery(id+"F17.wireOp",EDGE,"E237.right")])]});
            var sketch = newSketch(context, id + "F19", { "sketchPlane" : qUnion([Q0])});
            skLineSegment(sketch, "E238.bottom", {"start": v(-267.08, -16.05) * mm, "end": v(-276.54, -16.05) * mm});
            skLineSegment(sketch, "E238.top", {"start": v(-267.08, -13.46) * mm, "end": v(-276.54, -13.46) * mm});
            skLineSegment(sketch, "E238.left", {"start": v(-267.08, -16.05) * mm, "end": v(-267.08, -13.46) * mm});
            skLineSegment(sketch, "E238.right", {"start": v(-276.54, -16.05) * mm, "end": v(-276.54, -13.46) * mm});
            skSolve(sketch);
        }
        {
            var Q0;
            Q0=makeQuery(id+"F19.imprint","IMPRINT",FACE,{"disambiguationData":[TD([[makeQuery(id+"F19.imprint","IMPRINT",EDGE,{"derivedFrom":sQuery(id+"F19.wireOp",EDGE,"E238.bottom")}),-1.0]])]});
            extrude(context, id + "F20", {"entities" : qUnion([Q0]), "operationType" : NewBodyOperationType.ADD, "depth" : 10 * mm});
        }
        {
            var Q0;
            {var subQ0=sQuery(id+"F1.wireOp",EDGE,"E232.trimOffspring");var subQ1=sQuery(id+"F1.wireOp",EDGE,"E231.trimOffspring");var subQ2=sQuery(id+"F1.wireOp",EDGE,"E230.trimOffspring");var subQ3=sQuery(id+"F1.wireOp",EDGE,"E229.trimOffspring");var subQ4=sQuery(id+"F1.wireOp",EDGE,"E228.trimOffspring");var subQ5=sQuery(id+"F1.wireOp",EDGE,"E227.trimOffspring");var subQ6=sQuery(id+"F1.wireOp",EDGE,"E226.trimOffspring");var subQ7=sQuery(id+"F1.wireOp",EDGE,"E225.trimOffspring");var subQ8=sQuery(id+"F1.wireOp",EDGE,"E224.trimOffspring");var subQ9=sQuery(id+"F1.wireOp",EDGE,"E223.trimOffspring");var subQ10=sQuery(id+"F1.wireOp",EDGE,"E222.trimOffspring");var subQ11=sQuery(id+"F1.wireOp",EDGE,"E221.trimOffspring");var subQ12=sQuery(id+"F1.wireOp",EDGE,"E220.trimOffspring");var subQ13=sQuery(id+"F1.wireOp",EDGE,"E219.trimOffspring");var subQ14=sQuery(id+"F1.wireOp",EDGE,"E218.trimOffspring");var subQ15=sQuery(id+"F1.wireOp",EDGE,"E217.trimOffspring");var subQ16=sQuery(id+"F1.wireOp",EDGE,"E216.trimOffspring");var subQ17=sQuery(id+"F1.wireOp",EDGE,"E215.trimOffspring");var subQ18=sQuery(id+"F1.wireOp",EDGE,"E214.trimOffspring");var subQ19=sQuery(id+"F1.wireOp",EDGE,"E213.trimOffspring");var subQ20=sQuery(id+"F1.wireOp",EDGE,"E212.trimOffspring");var subQ21=sQuery(id+"F1.wireOp",EDGE,"E211.trimOffspring");var subQ22=sQuery(id+"F1.wireOp",EDGE,"E210.trimOffspring");var subQ23=sQuery(id+"F1.wireOp",EDGE,"E209.trimOffspring");var subQ24=sQuery(id+"F1.wireOp",EDGE,"E208.trimOffspring");var subQ25=sQuery(id+"F1.wireOp",EDGE,"E207.trimOffspring");var subQ26=sQuery(id+"F1.wireOp",EDGE,"E206.trimOffspring");var subQ27=sQuery(id+"F1.wireOp",EDGE,"E205.trimOffspring");var subQ28=sQuery(id+"F1.wireOp",EDGE,"E204.trimOffspring");var subQ29=sQuery(id+"F1.wireOp",EDGE,"E203.trimOffspring");var subQ30=sQuery(id+"F1.wireOp",EDGE,"E202.trimOffspring");var subQ31=sQuery(id+"F1.wireOp",EDGE,"E201.trimOffspring");var subQ32=sQuery(id+"F1.wireOp",EDGE,"E200.trimOffspring");var subQ33=sQuery(id+"F1.wireOp",EDGE,"E199.trimOffspring");var subQ34=sQuery(id+"F1.wireOp",EDGE,"E198.trimOffspring");var subQ35=sQuery(id+"F1.wireOp",EDGE,"E197.trimOffspring");var subQ36=sQuery(id+"F1.wireOp",EDGE,"E196.trimOffspring");var subQ37=sQuery(id+"F1.wireOp",EDGE,"E195.trimOffspring");var subQ38=sQuery(id+"F1.wireOp",EDGE,"E194.trimOffspring");var subQ39=sQuery(id+"F1.wireOp",EDGE,"E193.trimOffspring");var subQ40=sQuery(id+"F1.wireOp",EDGE,"E192.trimOffspring");var subQ41=sQuery(id+"F1.wireOp",EDGE,"E191.trimOffspring");var subQ42=sQuery(id+"F1.wireOp",EDGE,"E190.trimOffspring");var subQ43=sQuery(id+"F1.wireOp",EDGE,"E189.trimOffspring");var subQ44=sQuery(id+"F1.wireOp",EDGE,"E188.trimOffspring");var subQ45=sQuery(id+"F1.wireOp",EDGE,"E187.trimOffspring");var subQ46=sQuery(id+"F1.wireOp",EDGE,"E186.trimOffspring");var subQ47=sQuery(id+"F1.wireOp",EDGE,"E185.trimOffspring");var subQ48=sQuery(id+"F1.wireOp",EDGE,"E184.trimOffspring");var subQ49=sQuery(id+"F1.wireOp",EDGE,"E183.trimOffspring");var subQ50=sQuery(id+"F1.wireOp",EDGE,"E182.trimOffspring");var subQ51=sQuery(id+"F1.wireOp",EDGE,"E181.trimOffspring");var subQ52=sQuery(id+"F1.wireOp",EDGE,"E180.trimOffspring");var subQ53=sQuery(id+"F1.wireOp",EDGE,"E179.trimOffspring");var subQ54=sQuery(id+"F1.wireOp",EDGE,"E178.trimOffspring");var subQ55=sQuery(id+"F1.wireOp",EDGE,"E177.trimOffspring");var subQ56=sQuery(id+"F1.wireOp",EDGE,"E176.trimOffspring");var subQ57=sQuery(id+"F1.wireOp",EDGE,"E175.trimOffspring");var subQ58=sQuery(id+"F1.wireOp",EDGE,"E174.trimOffspring");var subQ59=sQuery(id+"F1.wireOp",EDGE,"E173.trimOffspring");var subQ60=sQuery(id+"F1.wireOp",EDGE,"E172.trimOffspring");var subQ61=sQuery(id+"F1.wireOp",EDGE,"E171.trimOffspring");var subQ62=sQuery(id+"F1.wireOp",EDGE,"E170.trimOffspring");var subQ63=sQuery(id+"F1.wireOp",EDGE,"E169.trimOffspring");var subQ64=sQuery(id+"F1.wireOp",EDGE,"E168.trimOffspring");var subQ65=sQuery(id+"F1.wireOp",EDGE,"E167.trimOffspring");var subQ66=sQuery(id+"F1.wireOp",EDGE,"E166.trimOffspring");var subQ67=sQuery(id+"F1.wireOp",EDGE,"E165.trimOffspring");var subQ68=sQuery(id+"F1.wireOp",EDGE,"E164.trimOffspring");var subQ69=sQuery(id+"F1.wireOp",EDGE,"E163.trimOffspring");var subQ70=sQuery(id+"F1.wireOp",EDGE,"E162.trimOffspring");var subQ71=sQuery(id+"F1.wireOp",EDGE,"E161.trimOffspring");var subQ72=sQuery(id+"F1.wireOp",EDGE,"E160.trimOffspring");var subQ73=sQuery(id+"F1.wireOp",EDGE,"E159.trimOffspring");var subQ74=sQuery(id+"F1.wireOp",EDGE,"E158.trimOffspring");var subQ75=sQuery(id+"F1.wireOp",EDGE,"E157.trimOffspring");var subQ76=sQuery(id+"F1.wireOp",EDGE,"E156.trimOffspring");var subQ77=sQuery(id+"F1.wireOp",EDGE,"E155.trimOffspring");var subQ78=sQuery(id+"F1.wireOp",EDGE,"E154.trimOffspring");var subQ79=sQuery(id+"F1.wireOp",EDGE,"E153.trimOffspring");var subQ80=sQuery(id+"F1.wireOp",EDGE,"E152.trimOffspring");var subQ81=sQuery(id+"F1.wireOp",EDGE,"E151.trimOffspring");var subQ82=sQuery(id+"F1.wireOp",EDGE,"E150.trimOffspring");var subQ83=sQuery(id+"F1.wireOp",EDGE,"E149.trimOffspring");var subQ84=sQuery(id+"F1.wireOp",EDGE,"E148.trimOffspring");var subQ85=sQuery(id+"F1.wireOp",EDGE,"E147.trimOffspring");var subQ86=sQuery(id+"F1.wireOp",EDGE,"E146.trimOffspring");var subQ87=sQuery(id+"F1.wireOp",EDGE,"E145.trimOffspring");var subQ88=sQuery(id+"F1.wireOp",EDGE,"E144.trimOffspring");var subQ89=sQuery(id+"F1.wireOp",EDGE,"E143.trimOffspring");var subQ90=sQuery(id+"F1.wireOp",EDGE,"E142.trimOffspring");var subQ91=sQuery(id+"F1.wireOp",EDGE,"E141.trimOffspring");var subQ92=sQuery(id+"F1.wireOp",EDGE,"E140.trimOffspring");var subQ93=sQuery(id+"F1.wireOp",EDGE,"E139.trimOffspring");var subQ94=sQuery(id+"F1.wireOp",EDGE,"E138.trimOffspring");var subQ95=sQuery(id+"F1.wireOp",EDGE,"E137.trimOffspring");var subQ96=sQuery(id+"F1.wireOp",EDGE,"E136.trimOffspring");var subQ97=sQuery(id+"F1.wireOp",EDGE,"E135.trimOffspring");var subQ98=sQuery(id+"F1.wireOp",EDGE,"E134.trimOffspring");var subQ99=sQuery(id+"F1.wireOp",EDGE,"E133.trimOffspring");var subQ100=sQuery(id+"F1.wireOp",EDGE,"E132.trimOffspring");var subQ101=sQuery(id+"F1.wireOp",EDGE,"E131.trimOffspring");var subQ102=sQuery(id+"F1.wireOp",EDGE,"E130.trimOffspring");var subQ103=sQuery(id+"F1.wireOp",EDGE,"E129.trimOffspring");var subQ104=sQuery(id+"F1.wireOp",EDGE,"E128.trimOffspring");var subQ105=sQuery(id+"F1.wireOp",EDGE,"E127.trimOffspring");var subQ106=sQuery(id+"F1.wireOp",EDGE,"E126.trimOffspring");var subQ107=sQuery(id+"F1.wireOp",EDGE,"E125.trimOffspring");var subQ108=sQuery(id+"F1.wireOp",EDGE,"E124.trimOffspring");var subQ109=sQuery(id+"F1.wireOp",EDGE,"E123.trimOffspring");var subQ110=sQuery(id+"F1.wireOp",EDGE,"E122.trimOffspring");var subQ111=sQuery(id+"F1.wireOp",EDGE,"E121.trimOffspring");var subQ112=sQuery(id+"F1.wireOp",EDGE,"E120.trimOffspring");var subQ113=sQuery(id+"F1.wireOp",EDGE,"E119.trimOffspring");var subQ114=sQuery(id+"F1.wireOp",EDGE,"E118.trimOffspring");var subQ115=sQuery(id+"F1.wireOp",EDGE,"E117.trimOffspring");var subQ116=sQuery(id+"F1.wireOp",EDGE,"E116.trimOffspring");var subQ117=sQuery(id+"F1.wireOp",EDGE,"E115.trimOffspring");var subQ118=sQuery(id+"F1.wireOp",EDGE,"E114.trimOffspring");var subQ119=sQuery(id+"F1.wireOp",EDGE,"E113.trimOffspring");var subQ120=sQuery(id+"F1.wireOp",EDGE,"E112.trimOffspring");var subQ121=sQuery(id+"F1.wireOp",EDGE,"E111.trimOffspring");var subQ122=sQuery(id+"F1.wireOp",EDGE,"E110.trimOffspring");var subQ123=sQuery(id+"F1.wireOp",EDGE,"E109.trimOffspring");var subQ124=sQuery(id+"F1.wireOp",EDGE,"E108.trimOffspring");var subQ125=sQuery(id+"F1.wireOp",EDGE,"E107.trimOffspring");var subQ126=sQuery(id+"F1.wireOp",EDGE,"E106.trimOffspring");var subQ127=sQuery(id+"F1.wireOp",EDGE,"E105.trimOffspring");var subQ128=sQuery(id+"F1.wireOp",EDGE,"E104.trimOffspring");var subQ129=sQuery(id+"F1.wireOp",EDGE,"E103.trimOffspring");var subQ130=sQuery(id+"F1.wireOp",EDGE,"E102.trimOffspring");var subQ131=sQuery(id+"F1.wireOp",EDGE,"E101.trimOffspring");var subQ132=sQuery(id+"F1.wireOp",EDGE,"E100.trimOffspring");var subQ133=sQuery(id+"F1.wireOp",EDGE,"E99.trimOffspring");var subQ134=sQuery(id+"F1.wireOp",EDGE,"E98.trimOffspring");var subQ135=sQuery(id+"F1.wireOp",EDGE,"E97.trimOffspring");var subQ136=sQuery(id+"F1.wireOp",EDGE,"E96.trimOffspring");var subQ137=sQuery(id+"F1.wireOp",EDGE,"E95.trimOffspring");var subQ138=sQuery(id+"F1.wireOp",EDGE,"E94.trimOffspring");var subQ139=sQuery(id+"F1.wireOp",EDGE,"E93.trimOffspring");var subQ140=sQuery(id+"F1.wireOp",EDGE,"E92.trimOffspring");var subQ141=sQuery(id+"F1.wireOp",EDGE,"E91.trimOffspring");var subQ142=sQuery(id+"F1.wireOp",EDGE,"E90");var subQ143=sQuery(id+"F1.wireOp",EDGE,"E89");var subQ144=sQuery(id+"F1.wireOp",EDGE,"E88.right");var subQ145=sQuery(id+"F1.wireOp",EDGE,"E88.left");var subQ146=sQuery(id+"F1.wireOp",EDGE,"E87.filletArc");var subQ147=sQuery(id+"F1.wireOp",EDGE,"E86.filletArc");var subQ148=sQuery(id+"F1.wireOp",EDGE,"E85.filletArc");var subQ149=sQuery(id+"F1.wireOp",EDGE,"E84.filletArc");var subQ150=sQuery(id+"F1.wireOp",EDGE,"E83.filletArc");var subQ151=sQuery(id+"F1.wireOp",EDGE,"E82.filletArc");var subQ152=sQuery(id+"F1.wireOp",EDGE,"E81.filletArc");var subQ153=sQuery(id+"F1.wireOp",EDGE,"E80.filletArc");var subQ154=sQuery(id+"F1.wireOp",EDGE,"E79.right");var subQ155=sQuery(id+"F1.wireOp",EDGE,"E79.left");var subQ156=sQuery(id+"F1.wireOp",EDGE,"E78.right");var subQ157=sQuery(id+"F1.wireOp",EDGE,"E78.left");var subQ158=sQuery(id+"F1.wireOp",EDGE,"E77.right");var subQ159=sQuery(id+"F1.wireOp",EDGE,"E77.left");var subQ160=sQuery(id+"F1.wireOp",EDGE,"E76.right");var subQ161=sQuery(id+"F1.wireOp",EDGE,"E76.left");var subQ162=sQuery(id+"F1.wireOp",EDGE,"E75.right");var subQ163=sQuery(id+"F1.wireOp",EDGE,"E75.left");var subQ164=sQuery(id+"F1.wireOp",EDGE,"E74.right");var subQ165=sQuery(id+"F1.wireOp",EDGE,"E74.left");var subQ166=sQuery(id+"F1.wireOp",EDGE,"E73.right");var subQ167=sQuery(id+"F1.wireOp",EDGE,"E73.left");var subQ168=sQuery(id+"F1.wireOp",EDGE,"E72.right");var subQ169=sQuery(id+"F1.wireOp",EDGE,"E72.left");var subQ170=sQuery(id+"F1.wireOp",EDGE,"E71.right");var subQ171=sQuery(id+"F1.wireOp",EDGE,"E71.left");var subQ172=sQuery(id+"F1.wireOp",EDGE,"E70.right");var subQ173=sQuery(id+"F1.wireOp",EDGE,"E70.left");var subQ174=sQuery(id+"F1.wireOp",EDGE,"E69.right");var subQ175=sQuery(id+"F1.wireOp",EDGE,"E69.left");var subQ176=sQuery(id+"F1.wireOp",EDGE,"E68.right");var subQ177=sQuery(id+"F1.wireOp",EDGE,"E68.left");var subQ178=sQuery(id+"F1.wireOp",EDGE,"E67.right");var subQ179=sQuery(id+"F1.wireOp",EDGE,"E67.left");var subQ180=sQuery(id+"F1.wireOp",EDGE,"E66.right");var subQ181=sQuery(id+"F1.wireOp",EDGE,"E66.left");var subQ182=sQuery(id+"F1.wireOp",EDGE,"E65.right");var subQ183=sQuery(id+"F1.wireOp",EDGE,"E65.left");var subQ184=sQuery(id+"F1.wireOp",EDGE,"E64.right");var subQ185=sQuery(id+"F1.wireOp",EDGE,"E64.left");var subQ186=sQuery(id+"F1.wireOp",EDGE,"E63.right");var subQ187=sQuery(id+"F1.wireOp",EDGE,"E63.left");var subQ188=sQuery(id+"F1.wireOp",EDGE,"E62.right");var subQ189=sQuery(id+"F1.wireOp",EDGE,"E62.left");var subQ190=sQuery(id+"F1.wireOp",EDGE,"E61.right");var subQ191=sQuery(id+"F1.wireOp",EDGE,"E61.left");var subQ192=sQuery(id+"F1.wireOp",EDGE,"E60.right");var subQ193=sQuery(id+"F1.wireOp",EDGE,"E60.left");var subQ194=sQuery(id+"F1.wireOp",EDGE,"E59.right");var subQ195=sQuery(id+"F1.wireOp",EDGE,"E59.left");var subQ196=sQuery(id+"F1.wireOp",EDGE,"E58.right");var subQ197=sQuery(id+"F1.wireOp",EDGE,"E58.left");var subQ198=sQuery(id+"F1.wireOp",EDGE,"E57.right");var subQ199=sQuery(id+"F1.wireOp",EDGE,"E57.left");var subQ200=sQuery(id+"F1.wireOp",EDGE,"E56.right");var subQ201=sQuery(id+"F1.wireOp",EDGE,"E56.left");var subQ202=sQuery(id+"F1.wireOp",EDGE,"E55.right");var subQ203=sQuery(id+"F1.wireOp",EDGE,"E55.left");var subQ204=sQuery(id+"F1.wireOp",EDGE,"E54.right");var subQ205=sQuery(id+"F1.wireOp",EDGE,"E54.left");var subQ206=sQuery(id+"F1.wireOp",EDGE,"E53.right");var subQ207=sQuery(id+"F1.wireOp",EDGE,"E53.left");var subQ208=sQuery(id+"F1.wireOp",EDGE,"E52.right");var subQ209=sQuery(id+"F1.wireOp",EDGE,"E52.left");var subQ210=sQuery(id+"F1.wireOp",EDGE,"E51.right");var subQ211=sQuery(id+"F1.wireOp",EDGE,"E51.left");var subQ212=sQuery(id+"F1.wireOp",EDGE,"E50.right");var subQ213=sQuery(id+"F1.wireOp",EDGE,"E49.right");var subQ214=sQuery(id+"F1.wireOp",EDGE,"E49.left");var subQ215=sQuery(id+"F1.wireOp",EDGE,"E48.right");var subQ216=sQuery(id+"F1.wireOp",EDGE,"E48.left");var subQ217=sQuery(id+"F1.wireOp",EDGE,"E47.right");var subQ218=sQuery(id+"F1.wireOp",EDGE,"E47.left");var subQ219=sQuery(id+"F1.wireOp",EDGE,"E46.right");var subQ220=sQuery(id+"F1.wireOp",EDGE,"E46.left");var subQ221=sQuery(id+"F1.wireOp",EDGE,"E45.right");var subQ222=sQuery(id+"F1.wireOp",EDGE,"E45.left");var subQ223=sQuery(id+"F1.wireOp",EDGE,"E44.right");var subQ224=sQuery(id+"F1.wireOp",EDGE,"E44.left");var subQ225=sQuery(id+"F1.wireOp",EDGE,"E43.right");var subQ226=sQuery(id+"F1.wireOp",EDGE,"E43.left");var subQ227=sQuery(id+"F1.wireOp",EDGE,"E42.right");var subQ228=sQuery(id+"F1.wireOp",EDGE,"E42.left");var subQ229=sQuery(id+"F1.wireOp",EDGE,"E41.right");var subQ230=sQuery(id+"F1.wireOp",EDGE,"E41.left");var subQ231=sQuery(id+"F1.wireOp",EDGE,"E40.right");var subQ232=sQuery(id+"F1.wireOp",EDGE,"E40.left");var subQ233=sQuery(id+"F1.wireOp",EDGE,"E39.right");var subQ234=sQuery(id+"F1.wireOp",EDGE,"E39.left");var subQ235=sQuery(id+"F1.wireOp",EDGE,"E38.right");var subQ236=sQuery(id+"F1.wireOp",EDGE,"E38.left");var subQ237=sQuery(id+"F1.wireOp",EDGE,"E37.right");var subQ238=sQuery(id+"F1.wireOp",EDGE,"E37.left");var subQ239=sQuery(id+"F1.wireOp",EDGE,"E36.right");var subQ240=sQuery(id+"F1.wireOp",EDGE,"E36.left");var subQ241=sQuery(id+"F1.wireOp",EDGE,"E35.right");var subQ242=sQuery(id+"F1.wireOp",EDGE,"E35.left");var subQ243=sQuery(id+"F1.wireOp",EDGE,"E34.right");var subQ244=sQuery(id+"F1.wireOp",EDGE,"E34.left");var subQ245=sQuery(id+"F1.wireOp",EDGE,"E33.right");var subQ246=sQuery(id+"F1.wireOp",EDGE,"E33.left");var subQ247=sQuery(id+"F1.wireOp",EDGE,"E32.right");var subQ248=sQuery(id+"F1.wireOp",EDGE,"E32.left");var subQ249=sQuery(id+"F1.wireOp",EDGE,"E31.right");var subQ250=sQuery(id+"F1.wireOp",EDGE,"E31.left");var subQ251=sQuery(id+"F1.wireOp",EDGE,"E30.right");var subQ252=sQuery(id+"F1.wireOp",EDGE,"E30.left");var subQ253=sQuery(id+"F1.wireOp",EDGE,"E29.right");var subQ254=sQuery(id+"F1.wireOp",EDGE,"E29.left");var subQ255=sQuery(id+"F1.wireOp",EDGE,"E28.right");var subQ256=sQuery(id+"F1.wireOp",EDGE,"E28.left");var subQ257=sQuery(id+"F1.wireOp",EDGE,"E27.right");var subQ258=sQuery(id+"F1.wireOp",EDGE,"E27.left");var subQ259=sQuery(id+"F1.wireOp",EDGE,"E26.right");var subQ260=sQuery(id+"F1.wireOp",EDGE,"E26.left");var subQ261=sQuery(id+"F1.wireOp",EDGE,"E25.right");var subQ262=sQuery(id+"F1.wireOp",EDGE,"E25.left");var subQ263=sQuery(id+"F1.wireOp",EDGE,"E24.right");var subQ264=sQuery(id+"F1.wireOp",EDGE,"E24.left");var subQ265=sQuery(id+"F1.wireOp",EDGE,"E23.right");var subQ266=sQuery(id+"F1.wireOp",EDGE,"E23.left");var subQ267=sQuery(id+"F1.wireOp",EDGE,"E22.right");var subQ268=sQuery(id+"F1.wireOp",EDGE,"E22.left");var subQ269=sQuery(id+"F1.wireOp",EDGE,"E21.right");var subQ270=sQuery(id+"F1.wireOp",EDGE,"E21.left");var subQ271=sQuery(id+"F1.wireOp",EDGE,"E20.right");var subQ272=sQuery(id+"F1.wireOp",EDGE,"E20.left");var subQ273=sQuery(id+"F1.wireOp",EDGE,"E19.right");var subQ274=sQuery(id+"F1.wireOp",EDGE,"E19.left");var subQ275=sQuery(id+"F1.wireOp",EDGE,"E18.right");var subQ276=sQuery(id+"F1.wireOp",EDGE,"E18.left");var subQ277=sQuery(id+"F1.wireOp",EDGE,"E17.top");var subQ278=sQuery(id+"F1.wireOp",EDGE,"E16.top");var subQ279=sQuery(id+"F1.wireOp",EDGE,"E15.top");var subQ280=sQuery(id+"F1.wireOp",EDGE,"E14.right");var subQ281=sQuery(id+"F1.wireOp",EDGE,"E14.left");var subQ282=sQuery(id+"F1.wireOp",EDGE,"E13.right");var subQ283=sQuery(id+"F1.wireOp",EDGE,"E13.left");var subQ284=sQuery(id+"F1.wireOp",EDGE,"E12.right");var subQ285=sQuery(id+"F1.wireOp",EDGE,"E12.left");var subQ286=sQuery(id+"F1.wireOp",EDGE,"E11.right");var subQ287=sQuery(id+"F1.wireOp",EDGE,"E11.left");var subQ288=sQuery(id+"F1.wireOp",EDGE,"E10.top");var subQ289=sQuery(id+"F1.wireOp",EDGE,"E10.bottom");var subQ290=sQuery(id+"F1.wireOp",EDGE,"E9.top");var subQ291=sQuery(id+"F1.wireOp",EDGE,"E9.bottom");var subQ292=sQuery(id+"F1.wireOp",EDGE,"E8.top");var subQ293=sQuery(id+"F1.wireOp",EDGE,"E8.bottom");var subQ294=sQuery(id+"F1.wireOp",EDGE,"E7.top");var subQ295=sQuery(id+"F1.wireOp",EDGE,"E7.bottom");var subQ296=sQuery(id+"F1.wireOp",EDGE,"E6.top");var subQ297=sQuery(id+"F1.wireOp",EDGE,"E6.bottom");var subQ298=sQuery(id+"F1.wireOp",EDGE,"E5.right");var subQ299=sQuery(id+"F1.wireOp",EDGE,"E5.left");var subQ300=sQuery(id+"F1.wireOp",EDGE,"E4");var subQ301=sQuery(id+"F1.wireOp",EDGE,"E3");var subQ302=sQuery(id+"F1.wireOp",EDGE,"E2");var subQ303=sQuery(id+"F1.wireOp",EDGE,"E1.0");Q0=makeQuery(id+"F14.opExtrude","SWEPT_FACE",FACE,{"disambiguationData":[OSD([subQ303,subQ302,subQ301,subQ300,subQ299,subQ298,subQ297,subQ296,subQ295,subQ294,subQ293,subQ292,subQ291,subQ290,subQ289,subQ288,subQ287,subQ286,subQ285,subQ284,subQ283,subQ282,subQ281,subQ280,subQ279,subQ278,subQ277,subQ276,subQ275,subQ274,subQ273,subQ272,subQ271,subQ270,subQ269,subQ268,subQ267,subQ266,subQ265,subQ264,subQ263,subQ262,subQ261,subQ260,subQ259,subQ258,subQ257,subQ256,subQ255,subQ254,subQ253,subQ252,subQ251,subQ250,subQ249,subQ248,subQ247,subQ246,subQ245,subQ244,subQ243,subQ242,subQ241,subQ240,subQ239,subQ238,subQ237,subQ236,subQ235,subQ234,subQ233,subQ232,subQ231,subQ230,subQ229,subQ228,subQ227,subQ226,subQ225,subQ224,subQ223,subQ222,subQ221,subQ220,subQ219,subQ218,subQ217,subQ216,subQ215,subQ214,subQ213,subQ212,subQ211,subQ210,subQ209,subQ208,subQ207,subQ206,subQ205,subQ204,subQ203,subQ202,subQ201,subQ200,subQ199,subQ198,subQ197,subQ196,subQ195,subQ194,subQ193,subQ192,subQ191,subQ190,subQ189,subQ188,subQ187,subQ186,subQ185,subQ184,subQ183,subQ182,subQ181,subQ180,subQ179,subQ178,subQ177,subQ176,subQ175,subQ174,subQ173,subQ172,subQ171,subQ170,subQ169,subQ168,subQ167,subQ166,subQ165,subQ164,subQ163,subQ162,subQ161,subQ160,subQ159,subQ158,subQ157,subQ156,subQ155,subQ154,subQ153,subQ152,subQ151,subQ150,subQ149,subQ148,subQ147,subQ146,subQ145,subQ144,subQ143,subQ142,subQ141,subQ140,subQ139,subQ138,subQ137,subQ136,subQ135,subQ134,subQ133,subQ132,subQ131,subQ130,subQ129,subQ128,subQ127,subQ126,subQ125,subQ124,subQ123,subQ122,subQ121,subQ120,subQ119,subQ118,subQ117,subQ116,subQ115,subQ114,subQ113,subQ112,subQ111,subQ110,subQ109,subQ108,subQ107,subQ106,subQ105,subQ104,subQ103,subQ102,subQ101,subQ100,subQ99,subQ98,subQ97,subQ96,subQ95,subQ94,subQ93,subQ92,subQ91,subQ90,subQ89,subQ88,subQ87,subQ86,subQ85,subQ84,subQ83,subQ82,subQ81,subQ80,subQ79,subQ78,subQ77,subQ76,subQ75,subQ74,subQ73,subQ72,subQ71,subQ70,subQ69,subQ68,subQ67,subQ66,subQ65,subQ64,subQ63,subQ62,subQ61,subQ60,subQ59,subQ58,subQ57,subQ56,subQ55,subQ54,subQ53,subQ52,subQ51,subQ50,subQ49,subQ48,subQ47,subQ46,subQ45,subQ44,subQ43,subQ42,subQ41,subQ40,subQ39,subQ38,subQ37,subQ36,subQ35,subQ34,subQ33,subQ32,subQ31,subQ30,subQ29,subQ28,subQ27,subQ26,subQ25,subQ24,subQ23,subQ22,subQ21,subQ20,subQ19,subQ18,subQ17,subQ16,subQ15,subQ14,subQ13,subQ12,subQ11,subQ10,subQ9,subQ8,subQ7,subQ6,subQ5,subQ4,subQ3,subQ2,subQ1,subQ0]),TDD([makeQuery(id+"F3.opFillet","BLEND_EDGE",EDGE,{"blendedFrom":[makeQuery(id+"F2.opExtrude","CAP_EDGE",EDGE,{"disambiguationData":[OSD([subQ301])],"isStart":true}),makeQuery(id+"F2.opExtrude","CAP_FACE",FACE,{"disambiguationData":[OSD([subQ303,subQ302,subQ301,subQ300,subQ299,subQ298,subQ297,subQ296,subQ295,subQ294,subQ293,subQ292,subQ291,subQ290,subQ289,subQ288,subQ287,subQ286,subQ285,subQ284,subQ283,subQ282,subQ281,subQ280,subQ279,subQ278,subQ277,subQ276,subQ275,subQ274,subQ273,subQ272,subQ271,subQ270,subQ269,subQ268,subQ267,subQ266,subQ265,subQ264,subQ263,subQ262,subQ261,subQ260,subQ259,subQ258,subQ257,subQ256,subQ255,subQ254,subQ253,subQ252,subQ251,subQ250,subQ249,subQ248,subQ247,subQ246,subQ245,subQ244,subQ243,subQ242,subQ241,subQ240,subQ239,subQ238,subQ237,subQ236,subQ235,subQ234,subQ233,subQ232,subQ231,subQ230,subQ229,subQ228,subQ227,subQ226,subQ225,subQ224,subQ223,subQ222,subQ221,subQ220,subQ219,subQ218,subQ217,subQ216,subQ215,subQ214,subQ213,subQ212,subQ211,subQ210,subQ209,subQ208,subQ207,subQ206,subQ205,subQ204,subQ203,subQ202,subQ201,subQ200,subQ199,subQ198,subQ197,subQ196,subQ195,subQ194,subQ193,subQ192,subQ191,subQ190,subQ189,subQ188,subQ187,subQ186,subQ185,subQ184,subQ183,subQ182,subQ181,subQ180,subQ179,subQ178,subQ177,subQ176,subQ175,subQ174,subQ173,subQ172,subQ171,subQ170,subQ169,subQ168,subQ167,subQ166,subQ165,subQ164,subQ163,subQ162,subQ161,subQ160,subQ159,subQ158,subQ157,subQ156,subQ155,subQ154,subQ153,subQ152,subQ151,subQ150,subQ149,subQ148,subQ147,subQ146,subQ145,subQ144,subQ143,subQ142,subQ141,subQ140,subQ139,subQ138,subQ137,subQ136,subQ135,subQ134,subQ133,subQ132,subQ131,subQ130,subQ129,subQ128,subQ127,subQ126,subQ125,subQ124,subQ123,subQ122,subQ121,subQ120,subQ119,subQ118,subQ117,subQ116,subQ115,subQ114,subQ113,subQ112,subQ111,subQ110,subQ109,subQ108,subQ107,subQ106,subQ105,subQ104,subQ103,subQ102,subQ101,subQ100,subQ99,subQ98,subQ97,subQ96,subQ95,subQ94,subQ93,subQ92,subQ91,subQ90,subQ89,subQ88,subQ87,subQ86,subQ85,subQ84,subQ83,subQ82,subQ81,subQ80,subQ79,subQ78,subQ77,subQ76,subQ75,subQ74,subQ73,subQ72,subQ71,subQ70,subQ69,subQ68,subQ67,subQ66,subQ65,subQ64,subQ63,subQ62,subQ61,subQ60,subQ59,subQ58,subQ57,subQ56,subQ55,subQ54,subQ53,subQ52,subQ51,subQ50,subQ49,subQ48,subQ47,subQ46,subQ45,subQ44,subQ43,subQ42,subQ41,subQ40,subQ39,subQ38,subQ37,subQ36,subQ35,subQ34,subQ33,subQ32,subQ31,subQ30,subQ29,subQ28,subQ27,subQ26,subQ25,subQ24,subQ23,subQ22,subQ21,subQ20,subQ19,subQ18,subQ17,subQ16,subQ15,subQ14,subQ13,subQ12,subQ11,subQ10,subQ9,subQ8,subQ7,subQ6,subQ5,subQ4,subQ3,subQ2,subQ1,subQ0])],"isStart":false})],"blendedInto":[makeQuery(id+"F2.opExtrude","CAP_FACE",FACE,{"disambiguationData":[OSD([subQ303,subQ302,subQ301,subQ300,subQ299,subQ298,subQ297,subQ296,subQ295,subQ294,subQ293,subQ292,subQ291,subQ290,subQ289,subQ288,subQ287,subQ286,subQ285,subQ284,subQ283,subQ282,subQ281,subQ280,subQ279,subQ278,subQ277,subQ276,subQ275,subQ274,subQ273,subQ272,subQ271,subQ270,subQ269,subQ268,subQ267,subQ266,subQ265,subQ264,subQ263,subQ262,subQ261,subQ260,subQ259,subQ258,subQ257,subQ256,subQ255,subQ254,subQ253,subQ252,subQ251,subQ250,subQ249,subQ248,subQ247,subQ246,subQ245,subQ244,subQ243,subQ242,subQ241,subQ240,subQ239,subQ238,subQ237,subQ236,subQ235,subQ234,subQ233,subQ232,subQ231,subQ230,subQ229,subQ228,subQ227,subQ226,subQ225,subQ224,subQ223,subQ222,subQ221,subQ220,subQ219,subQ218,subQ217,subQ216,subQ215,subQ214,subQ213,subQ212,subQ211,subQ210,subQ209,subQ208,subQ207,subQ206,subQ205,subQ204,subQ203,subQ202,subQ201,subQ200,subQ199,subQ198,subQ197,subQ196,subQ195,subQ194,subQ193,subQ192,subQ191,subQ190,subQ189,subQ188,subQ187,subQ186,subQ185,subQ184,subQ183,subQ182,subQ181,subQ180,subQ179,subQ178,subQ177,subQ176,subQ175,subQ174,subQ173,subQ172,subQ171,subQ170,subQ169,subQ168,subQ167,subQ166,subQ165,subQ164,subQ163,subQ162,subQ161,subQ160,subQ159,subQ158,subQ157,subQ156,subQ155,subQ154,subQ153,subQ152,subQ151,subQ150,subQ149,subQ148,subQ147,subQ146,subQ145,subQ144,subQ143,subQ142,subQ141,subQ140,subQ139,subQ138,subQ137,subQ136,subQ135,subQ134,subQ133,subQ132,subQ131,subQ130,subQ129,subQ128,subQ127,subQ126,subQ125,subQ124,subQ123,subQ122,subQ121,subQ120,subQ119,subQ118,subQ117,subQ116,subQ115,subQ114,subQ113,subQ112,subQ111,subQ110,subQ109,subQ108,subQ107,subQ106,subQ105,subQ104,subQ103,subQ102,subQ101,subQ100,subQ99,subQ98,subQ97,subQ96,subQ95,subQ94,subQ93,subQ92,subQ91,subQ90,subQ89,subQ88,subQ87,subQ86,subQ85,subQ84,subQ83,subQ82,subQ81,subQ80,subQ79,subQ78,subQ77,subQ76,subQ75,subQ74,subQ73,subQ72,subQ71,subQ70,subQ69,subQ68,subQ67,subQ66,subQ65,subQ64,subQ63,subQ62,subQ61,subQ60,subQ59,subQ58,subQ57,subQ56,subQ55,subQ54,subQ53,subQ52,subQ51,subQ50,subQ49,subQ48,subQ47,subQ46,subQ45,subQ44,subQ43,subQ42,subQ41,subQ40,subQ39,subQ38,subQ37,subQ36,subQ35,subQ34,subQ33,subQ32,subQ31,subQ30,subQ29,subQ28,subQ27,subQ26,subQ25,subQ24,subQ23,subQ22,subQ21,subQ20,subQ19,subQ18,subQ17,subQ16,subQ15,subQ14,subQ13,subQ12,subQ11,subQ10,subQ9,subQ8,subQ7,subQ6,subQ5,subQ4,subQ3,subQ2,subQ1,subQ0])],"isStart":false})]})])]});}
            var sketch = newSketch(context, id + "F21", { "sketchPlane" : qUnion([Q0])});
            skLineSegment(sketch, "E239.bottom", {"start": v(-276.74, 3) * mm, "end": v(-267.12, 3) * mm});
            skLineSegment(sketch, "E239.top", {"start": v(-276.74, 5.86) * mm, "end": v(-267.12, 5.86) * mm});
            skLineSegment(sketch, "E239.left", {"start": v(-276.74, 3) * mm, "end": v(-276.74, 5.86) * mm});
            skLineSegment(sketch, "E239.right", {"start": v(-267.12, 3) * mm, "end": v(-267.12, 5.86) * mm});
            skSolve(sketch);
        }
        {
            var Q0;
            Q0=makeQuery(id+"F21.imprint","IMPRINT",FACE,{"disambiguationData":[TD([[makeQuery(id+"F21.imprint","IMPRINT",EDGE,{"derivedFrom":sQuery(id+"F21.wireOp",EDGE,"E239.bottom")}),1.0]])]});
            extrude(context, id + "F22", {"entities" : qUnion([Q0]), "operationType" : NewBodyOperationType.ADD, "depth" : 5 * mm});
        }
        {
            var Q0;
            Q0=makeQuery(id+"F22.opExtrude","SWEPT_FACE",FACE,{"disambiguationData":[OSD([sQuery(id+"F21.wireOp",EDGE,"E239.bottom")])]});
            var sketch = newSketch(context, id + "F23", { "sketchPlane" : qUnion([Q0])});
            skLineSegment(sketch, "E240.bottom", {"start": v(-993.62, 267.12) * mm, "end": v(-996.12, 267.12) * mm});
            skLineSegment(sketch, "E240.top", {"start": v(-993.62, 276.74) * mm, "end": v(-996.12, 276.74) * mm});
            skLineSegment(sketch, "E240.left", {"start": v(-993.62, 267.12) * mm, "end": v(-993.62, 276.74) * mm});
            skLineSegment(sketch, "E240.right", {"start": v(-996.12, 267.12) * mm, "end": v(-996.12, 276.74) * mm});
            skSolve(sketch);
        }
        {
            var Q0;
            Q0=makeQuery(id+"F23.imprint","IMPRINT",FACE,{"disambiguationData":[TD([[makeQuery(id+"F23.imprint","IMPRINT",EDGE,{"derivedFrom":sQuery(id+"F23.wireOp",EDGE,"E240.bottom")}),-1.0]])]});
            extrude(context, id + "F24", {"entities" : qUnion([Q0]), "operationType" : NewBodyOperationType.ADD, "depth" : 19.05 * mm});
        }
        {
            var Q0;
            Q0=makeQuery(id+"F24.opExtrude","SWEPT_FACE",FACE,{"disambiguationData":[OSD([sQuery(id+"F23.wireOp",EDGE,"E240.right")])]});
            var sketch = newSketch(context, id + "F25", { "sketchPlane" : qUnion([Q0])});
            skLineSegment(sketch, "E241.bottom", {"start": v(267.12, -16.05) * mm, "end": v(276.74, -16.05) * mm});
            skLineSegment(sketch, "E241.top", {"start": v(267.12, -14) * mm, "end": v(276.74, -14) * mm});
            skLineSegment(sketch, "E241.left", {"start": v(267.12, -16.05) * mm, "end": v(267.12, -14) * mm});
            skLineSegment(sketch, "E241.right", {"start": v(276.74, -16.05) * mm, "end": v(276.74, -14) * mm});
            skSolve(sketch);
        }
        {
            var Q0;
            Q0=makeQuery(id+"F25.imprint","IMPRINT",FACE,{"disambiguationData":[TD([[makeQuery(id+"F25.imprint","IMPRINT",EDGE,{"derivedFrom":sQuery(id+"F25.wireOp",EDGE,"E241.bottom")}),1.0]])]});
            extrude(context, id + "F26", {"entities" : qUnion([Q0]), "operationType" : NewBodyOperationType.ADD, "depth" : 10 * mm});
        }
    });
